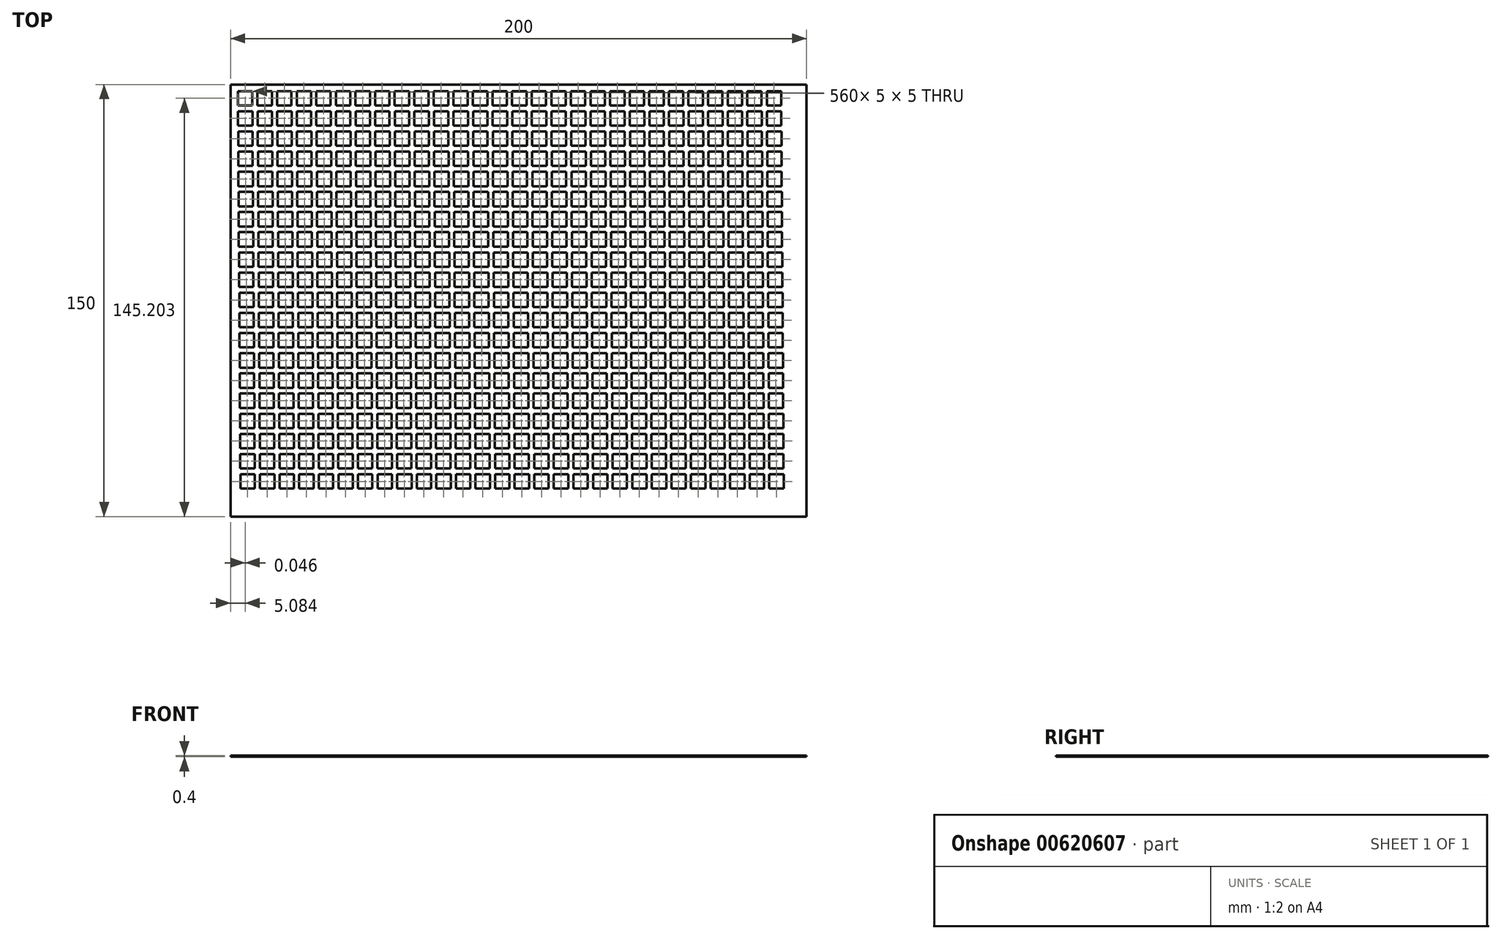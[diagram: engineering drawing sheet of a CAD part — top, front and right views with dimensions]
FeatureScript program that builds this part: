
annotation { "Feature Type Name" : "Feature", "Feature Type Description" : "" }
export const myFeature = defineFeature(function(context is Context, id is Id, definition is map)
    precondition{}
    {
        {
            var Q0;
            Q0=qCreatedBy(makeId("Top.planeOp"),FACE);
            var sketch = newSketch(context, id + "F0", { "sketchPlane" : qUnion([Q0])});
            skLineSegment(sketch, "E0.bottom", {"start": v(0, 0) * mm, "end": v(200, 0) * mm});
            skLineSegment(sketch, "E0.top", {"start": v(0, -150) * mm, "end": v(200, -150) * mm});
            skLineSegment(sketch, "E0.left", {"start": v(0, 0) * mm, "end": v(0, -150) * mm});
            skLineSegment(sketch, "E0.right", {"start": v(200, 0) * mm, "end": v(200, -150) * mm});
            skSolve(sketch);
        }
        {
            var Q0;
            Q0 = qSketchRegion(id + "F0", true);
            extrude(context, id + "F1", {"entities" : qUnion([Q0]), "depth" : 0.4 * mm, "offsetDistance" : 25 * mm});
        }
        {
            var Q0;
            Q0=makeQuery(id+"F1.opExtrude","CAP_FACE",FACE,{"disambiguationData":[OSD([sQuery(id+"F0.wireOp",EDGE,"E0.bottom"),sQuery(id+"F0.wireOp",EDGE,"E0.top"),sQuery(id+"F0.wireOp",EDGE,"E0.left"),sQuery(id+"F0.wireOp",EDGE,"E0.right")])],"isStart":false});
            var sketch = newSketch(context, id + "F2", { "sketchPlane" : qUnion([Q0])});
            skLineSegment(sketch, "E1.bottom", {"start": v(2.58, -2.3) * mm, "end": v(7.58, -2.3) * mm});
            skLineSegment(sketch, "E1.top", {"start": v(2.58, -7.3) * mm, "end": v(7.58, -7.3) * mm});
            skLineSegment(sketch, "E1.left", {"start": v(2.58, -2.3) * mm, "end": v(2.58, -7.3) * mm});
            skLineSegment(sketch, "E1.right", {"start": v(7.58, -2.3) * mm, "end": v(7.58, -7.3) * mm});
            skLineSegment(sketch, "E2.1.0.0", {"start": v(9.38, -2.3) * mm, "end": v(9.38, -7.3) * mm});
            skLineSegment(sketch, "E2.1.0.1", {"start": v(9.38, -2.3) * mm, "end": v(14.38, -2.3) * mm});
            skLineSegment(sketch, "E2.1.0.2", {"start": v(9.38, -7.3) * mm, "end": v(14.38, -7.3) * mm});
            skLineSegment(sketch, "E2.1.0.3", {"start": v(14.38, -2.3) * mm, "end": v(14.38, -7.3) * mm});
            skLineSegment(sketch, "E2.2.0.0", {"start": v(16.18, -2.3) * mm, "end": v(16.18, -7.3) * mm});
            skLineSegment(sketch, "E2.2.0.1", {"start": v(16.18, -2.3) * mm, "end": v(21.18, -2.3) * mm});
            skLineSegment(sketch, "E2.2.0.2", {"start": v(16.18, -7.3) * mm, "end": v(21.18, -7.3) * mm});
            skLineSegment(sketch, "E2.2.0.3", {"start": v(21.18, -2.3) * mm, "end": v(21.18, -7.3) * mm});
            skLineSegment(sketch, "E2.3.0.0", {"start": v(22.98, -2.3) * mm, "end": v(22.98, -7.3) * mm});
            skLineSegment(sketch, "E2.3.0.1", {"start": v(22.98, -2.3) * mm, "end": v(27.98, -2.3) * mm});
            skLineSegment(sketch, "E2.3.0.2", {"start": v(22.98, -7.3) * mm, "end": v(27.98, -7.3) * mm});
            skLineSegment(sketch, "E2.3.0.3", {"start": v(27.98, -2.3) * mm, "end": v(27.98, -7.3) * mm});
            skLineSegment(sketch, "E2.4.0.0", {"start": v(29.78, -2.3) * mm, "end": v(29.78, -7.3) * mm});
            skLineSegment(sketch, "E2.4.0.1", {"start": v(29.78, -2.3) * mm, "end": v(34.78, -2.3) * mm});
            skLineSegment(sketch, "E2.4.0.2", {"start": v(29.78, -7.3) * mm, "end": v(34.78, -7.3) * mm});
            skLineSegment(sketch, "E2.4.0.3", {"start": v(34.78, -2.3) * mm, "end": v(34.78, -7.3) * mm});
            skLineSegment(sketch, "E2.5.0.0", {"start": v(36.58, -2.3) * mm, "end": v(36.58, -7.3) * mm});
            skLineSegment(sketch, "E2.5.0.1", {"start": v(36.58, -2.3) * mm, "end": v(41.58, -2.3) * mm});
            skLineSegment(sketch, "E2.5.0.2", {"start": v(36.58, -7.3) * mm, "end": v(41.58, -7.3) * mm});
            skLineSegment(sketch, "E2.5.0.3", {"start": v(41.58, -2.3) * mm, "end": v(41.58, -7.3) * mm});
            skLineSegment(sketch, "E2.6.0.0", {"start": v(43.38, -2.3) * mm, "end": v(43.38, -7.3) * mm});
            skLineSegment(sketch, "E2.6.0.1", {"start": v(43.38, -2.3) * mm, "end": v(48.38, -2.3) * mm});
            skLineSegment(sketch, "E2.6.0.2", {"start": v(43.38, -7.3) * mm, "end": v(48.38, -7.3) * mm});
            skLineSegment(sketch, "E2.6.0.3", {"start": v(48.38, -2.3) * mm, "end": v(48.38, -7.3) * mm});
            skLineSegment(sketch, "E2.7.0.0", {"start": v(50.18, -2.3) * mm, "end": v(50.18, -7.3) * mm});
            skLineSegment(sketch, "E2.7.0.1", {"start": v(50.18, -2.3) * mm, "end": v(55.18, -2.3) * mm});
            skLineSegment(sketch, "E2.7.0.2", {"start": v(50.18, -7.3) * mm, "end": v(55.18, -7.3) * mm});
            skLineSegment(sketch, "E2.7.0.3", {"start": v(55.18, -2.3) * mm, "end": v(55.18, -7.3) * mm});
            skLineSegment(sketch, "E2.8.0.0", {"start": v(56.98, -2.3) * mm, "end": v(56.98, -7.3) * mm});
            skLineSegment(sketch, "E2.8.0.1", {"start": v(56.98, -2.3) * mm, "end": v(61.98, -2.3) * mm});
            skLineSegment(sketch, "E2.8.0.2", {"start": v(56.98, -7.3) * mm, "end": v(61.98, -7.3) * mm});
            skLineSegment(sketch, "E2.8.0.3", {"start": v(61.98, -2.3) * mm, "end": v(61.98, -7.3) * mm});
            skLineSegment(sketch, "E2.9.0.0", {"start": v(63.78, -2.3) * mm, "end": v(63.78, -7.3) * mm});
            skLineSegment(sketch, "E2.9.0.1", {"start": v(63.78, -2.3) * mm, "end": v(68.78, -2.3) * mm});
            skLineSegment(sketch, "E2.9.0.2", {"start": v(63.78, -7.3) * mm, "end": v(68.78, -7.3) * mm});
            skLineSegment(sketch, "E2.9.0.3", {"start": v(68.78, -2.3) * mm, "end": v(68.78, -7.3) * mm});
            skLineSegment(sketch, "E2.10.0.0", {"start": v(70.58, -2.3) * mm, "end": v(70.58, -7.3) * mm});
            skLineSegment(sketch, "E2.10.0.1", {"start": v(70.58, -2.3) * mm, "end": v(75.58, -2.3) * mm});
            skLineSegment(sketch, "E2.10.0.2", {"start": v(70.58, -7.3) * mm, "end": v(75.58, -7.3) * mm});
            skLineSegment(sketch, "E2.10.0.3", {"start": v(75.58, -2.3) * mm, "end": v(75.58, -7.3) * mm});
            skLineSegment(sketch, "E2.11.0.0", {"start": v(77.38, -2.3) * mm, "end": v(77.38, -7.3) * mm});
            skLineSegment(sketch, "E2.11.0.1", {"start": v(77.38, -2.3) * mm, "end": v(82.38, -2.3) * mm});
            skLineSegment(sketch, "E2.11.0.2", {"start": v(77.38, -7.3) * mm, "end": v(82.38, -7.3) * mm});
            skLineSegment(sketch, "E2.11.0.3", {"start": v(82.38, -2.3) * mm, "end": v(82.38, -7.3) * mm});
            skLineSegment(sketch, "E2.12.0.0", {"start": v(84.18, -2.3) * mm, "end": v(84.18, -7.3) * mm});
            skLineSegment(sketch, "E2.12.0.1", {"start": v(84.18, -2.3) * mm, "end": v(89.18, -2.3) * mm});
            skLineSegment(sketch, "E2.12.0.2", {"start": v(84.18, -7.3) * mm, "end": v(89.18, -7.3) * mm});
            skLineSegment(sketch, "E2.12.0.3", {"start": v(89.18, -2.3) * mm, "end": v(89.18, -7.3) * mm});
            skLineSegment(sketch, "E2.13.0.0", {"start": v(90.98, -2.3) * mm, "end": v(90.98, -7.3) * mm});
            skLineSegment(sketch, "E2.13.0.1", {"start": v(90.98, -2.3) * mm, "end": v(95.98, -2.3) * mm});
            skLineSegment(sketch, "E2.13.0.2", {"start": v(90.98, -7.3) * mm, "end": v(95.98, -7.3) * mm});
            skLineSegment(sketch, "E2.13.0.3", {"start": v(95.98, -2.3) * mm, "end": v(95.98, -7.3) * mm});
            skLineSegment(sketch, "E2.14.0.0", {"start": v(97.78, -2.3) * mm, "end": v(97.78, -7.3) * mm});
            skLineSegment(sketch, "E2.14.0.1", {"start": v(97.78, -2.3) * mm, "end": v(102.78, -2.3) * mm});
            skLineSegment(sketch, "E2.14.0.2", {"start": v(97.78, -7.3) * mm, "end": v(102.78, -7.3) * mm});
            skLineSegment(sketch, "E2.14.0.3", {"start": v(102.78, -2.3) * mm, "end": v(102.78, -7.3) * mm});
            skLineSegment(sketch, "E2.15.0.0", {"start": v(104.58, -2.3) * mm, "end": v(104.58, -7.3) * mm});
            skLineSegment(sketch, "E2.15.0.1", {"start": v(104.58, -2.3) * mm, "end": v(109.58, -2.3) * mm});
            skLineSegment(sketch, "E2.15.0.2", {"start": v(104.58, -7.3) * mm, "end": v(109.58, -7.3) * mm});
            skLineSegment(sketch, "E2.15.0.3", {"start": v(109.58, -2.3) * mm, "end": v(109.58, -7.3) * mm});
            skLineSegment(sketch, "E2.16.0.0", {"start": v(111.38, -2.3) * mm, "end": v(111.38, -7.3) * mm});
            skLineSegment(sketch, "E2.16.0.1", {"start": v(111.38, -2.3) * mm, "end": v(116.38, -2.3) * mm});
            skLineSegment(sketch, "E2.16.0.2", {"start": v(111.38, -7.3) * mm, "end": v(116.38, -7.3) * mm});
            skLineSegment(sketch, "E2.16.0.3", {"start": v(116.38, -2.3) * mm, "end": v(116.38, -7.3) * mm});
            skLineSegment(sketch, "E2.17.0.0", {"start": v(118.18, -2.3) * mm, "end": v(118.18, -7.3) * mm});
            skLineSegment(sketch, "E2.17.0.1", {"start": v(118.18, -2.3) * mm, "end": v(123.18, -2.3) * mm});
            skLineSegment(sketch, "E2.17.0.2", {"start": v(118.18, -7.3) * mm, "end": v(123.18, -7.3) * mm});
            skLineSegment(sketch, "E2.17.0.3", {"start": v(123.18, -2.3) * mm, "end": v(123.18, -7.3) * mm});
            skLineSegment(sketch, "E2.18.0.0", {"start": v(124.98, -2.3) * mm, "end": v(124.98, -7.3) * mm});
            skLineSegment(sketch, "E2.18.0.1", {"start": v(124.98, -2.3) * mm, "end": v(129.98, -2.3) * mm});
            skLineSegment(sketch, "E2.18.0.2", {"start": v(124.98, -7.3) * mm, "end": v(129.98, -7.3) * mm});
            skLineSegment(sketch, "E2.18.0.3", {"start": v(129.98, -2.3) * mm, "end": v(129.98, -7.3) * mm});
            skLineSegment(sketch, "E2.19.0.0", {"start": v(131.78, -2.3) * mm, "end": v(131.78, -7.3) * mm});
            skLineSegment(sketch, "E2.19.0.1", {"start": v(131.78, -2.3) * mm, "end": v(136.78, -2.3) * mm});
            skLineSegment(sketch, "E2.19.0.2", {"start": v(131.78, -7.3) * mm, "end": v(136.78, -7.3) * mm});
            skLineSegment(sketch, "E2.19.0.3", {"start": v(136.78, -2.3) * mm, "end": v(136.78, -7.3) * mm});
            skLineSegment(sketch, "E2.20.0.0", {"start": v(138.58, -2.3) * mm, "end": v(138.58, -7.3) * mm});
            skLineSegment(sketch, "E2.20.0.1", {"start": v(138.58, -2.3) * mm, "end": v(143.58, -2.3) * mm});
            skLineSegment(sketch, "E2.20.0.2", {"start": v(138.58, -7.3) * mm, "end": v(143.58, -7.3) * mm});
            skLineSegment(sketch, "E2.20.0.3", {"start": v(143.58, -2.3) * mm, "end": v(143.58, -7.3) * mm});
            skLineSegment(sketch, "E2.21.0.0", {"start": v(145.38, -2.3) * mm, "end": v(145.38, -7.3) * mm});
            skLineSegment(sketch, "E2.21.0.1", {"start": v(145.38, -2.3) * mm, "end": v(150.38, -2.3) * mm});
            skLineSegment(sketch, "E2.21.0.2", {"start": v(145.38, -7.3) * mm, "end": v(150.38, -7.3) * mm});
            skLineSegment(sketch, "E2.21.0.3", {"start": v(150.38, -2.3) * mm, "end": v(150.38, -7.3) * mm});
            skLineSegment(sketch, "E2.22.0.0", {"start": v(152.18, -2.3) * mm, "end": v(152.18, -7.3) * mm});
            skLineSegment(sketch, "E2.22.0.1", {"start": v(152.18, -2.3) * mm, "end": v(157.18, -2.3) * mm});
            skLineSegment(sketch, "E2.22.0.2", {"start": v(152.18, -7.3) * mm, "end": v(157.18, -7.3) * mm});
            skLineSegment(sketch, "E2.22.0.3", {"start": v(157.18, -2.3) * mm, "end": v(157.18, -7.3) * mm});
            skLineSegment(sketch, "E2.23.0.0", {"start": v(158.98, -2.3) * mm, "end": v(158.98, -7.3) * mm});
            skLineSegment(sketch, "E2.23.0.1", {"start": v(158.98, -2.3) * mm, "end": v(163.98, -2.3) * mm});
            skLineSegment(sketch, "E2.23.0.2", {"start": v(158.98, -7.3) * mm, "end": v(163.98, -7.3) * mm});
            skLineSegment(sketch, "E2.23.0.3", {"start": v(163.98, -2.3) * mm, "end": v(163.98, -7.3) * mm});
            skLineSegment(sketch, "E2.24.0.0", {"start": v(165.78, -2.3) * mm, "end": v(165.78, -7.3) * mm});
            skLineSegment(sketch, "E2.24.0.1", {"start": v(165.78, -2.3) * mm, "end": v(170.78, -2.3) * mm});
            skLineSegment(sketch, "E2.24.0.2", {"start": v(165.78, -7.3) * mm, "end": v(170.78, -7.3) * mm});
            skLineSegment(sketch, "E2.24.0.3", {"start": v(170.78, -2.3) * mm, "end": v(170.78, -7.3) * mm});
            skLineSegment(sketch, "E2.25.0.0", {"start": v(172.58, -2.3) * mm, "end": v(172.58, -7.3) * mm});
            skLineSegment(sketch, "E2.25.0.1", {"start": v(172.58, -2.3) * mm, "end": v(177.58, -2.3) * mm});
            skLineSegment(sketch, "E2.25.0.2", {"start": v(172.58, -7.3) * mm, "end": v(177.58, -7.3) * mm});
            skLineSegment(sketch, "E2.25.0.3", {"start": v(177.58, -2.3) * mm, "end": v(177.58, -7.3) * mm});
            skLineSegment(sketch, "E2.direction1", {"start": v(2.58, -7.3) * mm, "end": v(9.38, -7.3) * mm, "construction": true});
            skLineSegment(sketch, "E3.0.26.0", {"start": v(179.38, -2.3) * mm, "end": v(179.38, -7.3) * mm});
            skLineSegment(sketch, "E3.3.26.0", {"start": v(179.38, -2.3) * mm, "end": v(184.38, -2.3) * mm});
            skLineSegment(sketch, "E3.6.26.0", {"start": v(179.38, -7.3) * mm, "end": v(184.38, -7.3) * mm});
            skLineSegment(sketch, "E3.9.26.0", {"start": v(184.38, -2.3) * mm, "end": v(184.38, -7.3) * mm});
            skLineSegment(sketch, "E3.0.27.0", {"start": v(186.18, -2.3) * mm, "end": v(186.18, -7.3) * mm});
            skLineSegment(sketch, "E3.3.27.0", {"start": v(186.18, -2.3) * mm, "end": v(191.18, -2.3) * mm});
            skLineSegment(sketch, "E3.6.27.0", {"start": v(186.18, -7.3) * mm, "end": v(191.18, -7.3) * mm});
            skLineSegment(sketch, "E3.9.27.0", {"start": v(191.18, -2.3) * mm, "end": v(191.18, -7.3) * mm});
            skLineSegment(sketch, "E4.1.0.0", {"start": v(111.43, -9.3) * mm, "end": v(116.43, -9.3) * mm});
            skLineSegment(sketch, "E4.1.0.1", {"start": v(116.43, -9.3) * mm, "end": v(116.43, -14.3) * mm});
            skLineSegment(sketch, "E4.1.0.2", {"start": v(125.03, -9.3) * mm, "end": v(130.03, -9.3) * mm});
            skLineSegment(sketch, "E4.1.0.3", {"start": v(28.03, -9.3) * mm, "end": v(28.03, -14.3) * mm});
            skLineSegment(sketch, "E4.1.0.4", {"start": v(70.63, -9.3) * mm, "end": v(75.63, -9.3) * mm});
            skLineSegment(sketch, "E4.1.0.5", {"start": v(172.63, -9.3) * mm, "end": v(172.63, -14.3) * mm});
            skLineSegment(sketch, "E4.1.0.6", {"start": v(48.43, -9.3) * mm, "end": v(48.43, -14.3) * mm});
            skLineSegment(sketch, "E4.1.0.7", {"start": v(84.23, -9.3) * mm, "end": v(84.23, -14.3) * mm});
            skLineSegment(sketch, "E4.1.0.8", {"start": v(14.43, -9.3) * mm, "end": v(14.43, -14.3) * mm});
            skLineSegment(sketch, "E4.1.0.9", {"start": v(97.83, -9.3) * mm, "end": v(102.83, -9.3) * mm});
            skLineSegment(sketch, "E4.1.0.10", {"start": v(165.83, -9.3) * mm, "end": v(165.83, -14.3) * mm});
            skLineSegment(sketch, "E4.1.0.11", {"start": v(91.03, -9.3) * mm, "end": v(96.03, -9.3) * mm});
            skLineSegment(sketch, "E4.1.0.12", {"start": v(70.63, -14.3) * mm, "end": v(75.63, -14.3) * mm});
            skLineSegment(sketch, "E4.1.0.13", {"start": v(131.83, -14.3) * mm, "end": v(136.83, -14.3) * mm});
            skLineSegment(sketch, "E4.1.0.14", {"start": v(145.43, -9.3) * mm, "end": v(145.43, -14.3) * mm});
            skLineSegment(sketch, "E4.1.0.15", {"start": v(104.63, -14.3) * mm, "end": v(109.63, -14.3) * mm});
            skLineSegment(sketch, "E4.1.0.16", {"start": v(191.23, -9.3) * mm, "end": v(191.23, -14.3) * mm});
            skLineSegment(sketch, "E4.1.0.17", {"start": v(159.03, -14.3) * mm, "end": v(164.03, -14.3) * mm});
            skLineSegment(sketch, "E4.1.0.18", {"start": v(75.63, -9.3) * mm, "end": v(75.63, -14.3) * mm});
            skLineSegment(sketch, "E4.1.0.19", {"start": v(23.03, -9.3) * mm, "end": v(23.03, -14.3) * mm});
            skLineSegment(sketch, "E4.1.0.20", {"start": v(145.43, -9.3) * mm, "end": v(150.43, -9.3) * mm});
            skLineSegment(sketch, "E4.1.0.21", {"start": v(138.63, -14.3) * mm, "end": v(143.63, -14.3) * mm});
            skLineSegment(sketch, "E4.1.0.22", {"start": v(184.43, -9.3) * mm, "end": v(184.43, -14.3) * mm});
            skLineSegment(sketch, "E4.1.0.23", {"start": v(55.23, -9.3) * mm, "end": v(55.23, -14.3) * mm});
            skLineSegment(sketch, "E4.1.0.24", {"start": v(170.83, -9.3) * mm, "end": v(170.83, -14.3) * mm});
            skLineSegment(sketch, "E4.1.0.25", {"start": v(62.03, -9.3) * mm, "end": v(62.03, -14.3) * mm});
            skLineSegment(sketch, "E4.1.0.26", {"start": v(68.83, -9.3) * mm, "end": v(68.83, -14.3) * mm});
            skLineSegment(sketch, "E4.1.0.27", {"start": v(131.83, -9.3) * mm, "end": v(136.83, -9.3) * mm});
            skLineSegment(sketch, "E4.1.0.28", {"start": v(63.83, -9.3) * mm, "end": v(63.83, -14.3) * mm});
            skLineSegment(sketch, "E4.1.0.29", {"start": v(152.23, -14.3) * mm, "end": v(157.23, -14.3) * mm});
            skLineSegment(sketch, "E4.1.0.30", {"start": v(179.43, -14.3) * mm, "end": v(184.43, -14.3) * mm});
            skLineSegment(sketch, "E4.1.0.31", {"start": v(36.63, -9.3) * mm, "end": v(36.63, -14.3) * mm});
            skLineSegment(sketch, "E4.1.0.32", {"start": v(172.63, -14.3) * mm, "end": v(177.63, -14.3) * mm});
            skLineSegment(sketch, "E4.1.0.33", {"start": v(91.03, -9.3) * mm, "end": v(91.03, -14.3) * mm});
            skLineSegment(sketch, "E4.1.0.34", {"start": v(77.43, -9.3) * mm, "end": v(82.43, -9.3) * mm});
            skLineSegment(sketch, "E4.1.0.35", {"start": v(70.63, -9.3) * mm, "end": v(70.63, -14.3) * mm});
            skLineSegment(sketch, "E4.1.0.36", {"start": v(57.03, -14.3) * mm, "end": v(62.03, -14.3) * mm});
            skLineSegment(sketch, "E4.1.0.37", {"start": v(111.43, -9.3) * mm, "end": v(111.43, -14.3) * mm});
            skLineSegment(sketch, "E4.1.0.38", {"start": v(150.43, -9.3) * mm, "end": v(150.43, -14.3) * mm});
            skLineSegment(sketch, "E4.1.0.39", {"start": v(177.63, -9.3) * mm, "end": v(177.63, -14.3) * mm});
            skLineSegment(sketch, "E4.1.0.40", {"start": v(179.43, -9.3) * mm, "end": v(179.43, -14.3) * mm});
            skLineSegment(sketch, "E4.1.0.41", {"start": v(97.83, -9.3) * mm, "end": v(97.83, -14.3) * mm});
            skLineSegment(sketch, "E4.1.0.42", {"start": v(36.63, -9.3) * mm, "end": v(41.63, -9.3) * mm});
            skLineSegment(sketch, "E4.1.0.43", {"start": v(118.23, -14.3) * mm, "end": v(123.23, -14.3) * mm});
            skLineSegment(sketch, "E4.1.0.44", {"start": v(7.63, -9.3) * mm, "end": v(7.63, -14.3) * mm});
            skLineSegment(sketch, "E4.1.0.45", {"start": v(43.43, -9.3) * mm, "end": v(43.43, -14.3) * mm});
            skLineSegment(sketch, "E4.1.0.46", {"start": v(77.43, -14.3) * mm, "end": v(82.43, -14.3) * mm});
            skLineSegment(sketch, "E4.1.0.47", {"start": v(138.63, -9.3) * mm, "end": v(143.63, -9.3) * mm});
            skLineSegment(sketch, "E4.1.0.48", {"start": v(23.03, -9.3) * mm, "end": v(28.03, -9.3) * mm});
            skLineSegment(sketch, "E4.1.0.49", {"start": v(152.23, -9.3) * mm, "end": v(152.23, -14.3) * mm});
            skLineSegment(sketch, "E4.1.0.50", {"start": v(57.03, -9.3) * mm, "end": v(62.03, -9.3) * mm});
            skLineSegment(sketch, "E4.1.0.51", {"start": v(43.43, -9.3) * mm, "end": v(48.43, -9.3) * mm});
            skLineSegment(sketch, "E4.1.0.52", {"start": v(41.63, -9.3) * mm, "end": v(41.63, -14.3) * mm});
            skLineSegment(sketch, "E4.1.0.53", {"start": v(125.03, -14.3) * mm, "end": v(130.03, -14.3) * mm});
            skLineSegment(sketch, "E4.1.0.54", {"start": v(186.23, -14.3) * mm, "end": v(191.23, -14.3) * mm});
            skLineSegment(sketch, "E4.1.0.55", {"start": v(125.03, -9.3) * mm, "end": v(125.03, -14.3) * mm});
            skLineSegment(sketch, "E4.1.0.56", {"start": v(63.83, -9.3) * mm, "end": v(68.83, -9.3) * mm});
            skLineSegment(sketch, "E4.1.0.57", {"start": v(63.83, -14.3) * mm, "end": v(68.83, -14.3) * mm});
            skLineSegment(sketch, "E4.1.0.58", {"start": v(164.03, -9.3) * mm, "end": v(164.03, -14.3) * mm});
            skLineSegment(sketch, "E4.1.0.59", {"start": v(186.23, -9.3) * mm, "end": v(186.23, -14.3) * mm});
            skLineSegment(sketch, "E4.1.0.60", {"start": v(9.43, -9.3) * mm, "end": v(9.43, -14.3) * mm});
            skLineSegment(sketch, "E4.1.0.61", {"start": v(84.23, -9.3) * mm, "end": v(89.23, -9.3) * mm});
            skLineSegment(sketch, "E4.1.0.62", {"start": v(9.43, -9.3) * mm, "end": v(14.43, -9.3) * mm});
            skLineSegment(sketch, "E4.1.0.63", {"start": v(50.23, -9.3) * mm, "end": v(55.23, -9.3) * mm});
            skLineSegment(sketch, "E4.1.0.64", {"start": v(109.63, -9.3) * mm, "end": v(109.63, -14.3) * mm});
            skLineSegment(sketch, "E4.1.0.65", {"start": v(91.03, -14.3) * mm, "end": v(96.03, -14.3) * mm});
            skLineSegment(sketch, "E4.1.0.66", {"start": v(102.83, -9.3) * mm, "end": v(102.83, -14.3) * mm});
            skLineSegment(sketch, "E4.1.0.67", {"start": v(2.63, -9.3) * mm, "end": v(7.63, -9.3) * mm});
            skLineSegment(sketch, "E4.1.0.68", {"start": v(97.83, -14.3) * mm, "end": v(102.83, -14.3) * mm});
            skLineSegment(sketch, "E4.1.0.69", {"start": v(123.23, -9.3) * mm, "end": v(123.23, -14.3) * mm});
            skLineSegment(sketch, "E4.1.0.70", {"start": v(84.23, -14.3) * mm, "end": v(89.23, -14.3) * mm});
            skLineSegment(sketch, "E4.1.0.71", {"start": v(16.23, -9.3) * mm, "end": v(21.23, -9.3) * mm});
            skLineSegment(sketch, "E4.1.0.72", {"start": v(29.83, -9.3) * mm, "end": v(34.83, -9.3) * mm});
            skLineSegment(sketch, "E4.1.0.73", {"start": v(77.43, -9.3) * mm, "end": v(77.43, -14.3) * mm});
            skLineSegment(sketch, "E4.1.0.74", {"start": v(2.63, -9.3) * mm, "end": v(2.63, -14.3) * mm});
            skLineSegment(sketch, "E4.1.0.75", {"start": v(29.83, -9.3) * mm, "end": v(29.83, -14.3) * mm});
            skLineSegment(sketch, "E4.1.0.76", {"start": v(159.03, -9.3) * mm, "end": v(159.03, -14.3) * mm});
            skLineSegment(sketch, "E4.1.0.77", {"start": v(104.63, -9.3) * mm, "end": v(109.63, -9.3) * mm});
            skLineSegment(sketch, "E4.1.0.78", {"start": v(82.43, -9.3) * mm, "end": v(82.43, -14.3) * mm});
            skLineSegment(sketch, "E4.1.0.79", {"start": v(34.83, -9.3) * mm, "end": v(34.83, -14.3) * mm});
            skLineSegment(sketch, "E4.1.0.80", {"start": v(157.23, -9.3) * mm, "end": v(157.23, -14.3) * mm});
            skLineSegment(sketch, "E4.1.0.81", {"start": v(21.23, -9.3) * mm, "end": v(21.23, -14.3) * mm});
            skLineSegment(sketch, "E4.1.0.82", {"start": v(143.63, -9.3) * mm, "end": v(143.63, -14.3) * mm});
            skLineSegment(sketch, "E4.1.0.83", {"start": v(138.63, -9.3) * mm, "end": v(138.63, -14.3) * mm});
            skLineSegment(sketch, "E4.1.0.84", {"start": v(130.03, -9.3) * mm, "end": v(130.03, -14.3) * mm});
            skLineSegment(sketch, "E4.1.0.85", {"start": v(57.03, -9.3) * mm, "end": v(57.03, -14.3) * mm});
            skLineSegment(sketch, "E4.1.0.86", {"start": v(136.83, -9.3) * mm, "end": v(136.83, -14.3) * mm});
            skLineSegment(sketch, "E4.1.0.87", {"start": v(118.23, -9.3) * mm, "end": v(118.23, -14.3) * mm});
            skLineSegment(sketch, "E4.1.0.88", {"start": v(96.03, -9.3) * mm, "end": v(96.03, -14.3) * mm});
            skLineSegment(sketch, "E4.1.0.89", {"start": v(145.43, -14.3) * mm, "end": v(150.43, -14.3) * mm});
            skLineSegment(sketch, "E4.1.0.90", {"start": v(165.83, -14.3) * mm, "end": v(170.83, -14.3) * mm});
            skLineSegment(sketch, "E4.1.0.91", {"start": v(50.23, -9.3) * mm, "end": v(50.23, -14.3) * mm});
            skLineSegment(sketch, "E4.1.0.92", {"start": v(118.23, -9.3) * mm, "end": v(123.23, -9.3) * mm});
            skLineSegment(sketch, "E4.1.0.93", {"start": v(131.83, -9.3) * mm, "end": v(131.83, -14.3) * mm});
            skLineSegment(sketch, "E4.1.0.94", {"start": v(16.23, -9.3) * mm, "end": v(16.23, -14.3) * mm});
            skLineSegment(sketch, "E4.1.0.95", {"start": v(104.63, -9.3) * mm, "end": v(104.63, -14.3) * mm});
            skLineSegment(sketch, "E4.1.0.96", {"start": v(111.43, -14.3) * mm, "end": v(116.43, -14.3) * mm});
            skLineSegment(sketch, "E4.1.0.97", {"start": v(89.23, -9.3) * mm, "end": v(89.23, -14.3) * mm});
            skLineSegment(sketch, "E4.1.0.98", {"start": v(152.23, -9.3) * mm, "end": v(157.23, -9.3) * mm});
            skLineSegment(sketch, "E4.1.0.99", {"start": v(186.23, -9.3) * mm, "end": v(191.23, -9.3) * mm});
            skLineSegment(sketch, "E4.1.0.100", {"start": v(36.63, -14.3) * mm, "end": v(41.63, -14.3) * mm});
            skLineSegment(sketch, "E4.1.0.101", {"start": v(43.43, -14.3) * mm, "end": v(48.43, -14.3) * mm});
            skLineSegment(sketch, "E4.1.0.102", {"start": v(2.63, -14.3) * mm, "end": v(9.43, -14.3) * mm, "construction": true});
            skLineSegment(sketch, "E4.1.0.103", {"start": v(159.03, -9.3) * mm, "end": v(164.03, -9.3) * mm});
            skLineSegment(sketch, "E4.1.0.104", {"start": v(165.83, -9.3) * mm, "end": v(170.83, -9.3) * mm});
            skLineSegment(sketch, "E4.1.0.105", {"start": v(172.63, -9.3) * mm, "end": v(177.63, -9.3) * mm});
            skLineSegment(sketch, "E4.1.0.106", {"start": v(16.23, -14.3) * mm, "end": v(21.23, -14.3) * mm});
            skLineSegment(sketch, "E4.1.0.107", {"start": v(29.83, -14.3) * mm, "end": v(34.83, -14.3) * mm});
            skLineSegment(sketch, "E4.1.0.108", {"start": v(23.03, -14.3) * mm, "end": v(28.03, -14.3) * mm});
            skLineSegment(sketch, "E4.1.0.109", {"start": v(9.43, -14.3) * mm, "end": v(14.43, -14.3) * mm});
            skLineSegment(sketch, "E4.1.0.110", {"start": v(50.23, -14.3) * mm, "end": v(55.23, -14.3) * mm});
            skLineSegment(sketch, "E4.1.0.111", {"start": v(179.43, -9.3) * mm, "end": v(184.43, -9.3) * mm});
            skLineSegment(sketch, "E4.1.0.112", {"start": v(2.63, -14.3) * mm, "end": v(7.63, -14.3) * mm});
            skLineSegment(sketch, "E4.2.0.0", {"start": v(111.48, -16.3) * mm, "end": v(116.48, -16.3) * mm});
            skLineSegment(sketch, "E4.2.0.1", {"start": v(116.48, -16.3) * mm, "end": v(116.48, -21.3) * mm});
            skLineSegment(sketch, "E4.2.0.2", {"start": v(125.08, -16.3) * mm, "end": v(130.08, -16.3) * mm});
            skLineSegment(sketch, "E4.2.0.3", {"start": v(28.08, -16.3) * mm, "end": v(28.08, -21.3) * mm});
            skLineSegment(sketch, "E4.2.0.4", {"start": v(70.68, -16.3) * mm, "end": v(75.68, -16.3) * mm});
            skLineSegment(sketch, "E4.2.0.5", {"start": v(172.68, -16.3) * mm, "end": v(172.68, -21.3) * mm});
            skLineSegment(sketch, "E4.2.0.6", {"start": v(48.48, -16.3) * mm, "end": v(48.48, -21.3) * mm});
            skLineSegment(sketch, "E4.2.0.7", {"start": v(84.28, -16.3) * mm, "end": v(84.28, -21.3) * mm});
            skLineSegment(sketch, "E4.2.0.8", {"start": v(14.48, -16.3) * mm, "end": v(14.48, -21.3) * mm});
            skLineSegment(sketch, "E4.2.0.9", {"start": v(97.88, -16.3) * mm, "end": v(102.88, -16.3) * mm});
            skLineSegment(sketch, "E4.2.0.10", {"start": v(165.88, -16.3) * mm, "end": v(165.88, -21.3) * mm});
            skLineSegment(sketch, "E4.2.0.11", {"start": v(91.08, -16.3) * mm, "end": v(96.08, -16.3) * mm});
            skLineSegment(sketch, "E4.2.0.12", {"start": v(70.68, -21.3) * mm, "end": v(75.68, -21.3) * mm});
            skLineSegment(sketch, "E4.2.0.13", {"start": v(131.88, -21.3) * mm, "end": v(136.88, -21.3) * mm});
            skLineSegment(sketch, "E4.2.0.14", {"start": v(145.48, -16.3) * mm, "end": v(145.48, -21.3) * mm});
            skLineSegment(sketch, "E4.2.0.15", {"start": v(104.68, -21.3) * mm, "end": v(109.68, -21.3) * mm});
            skLineSegment(sketch, "E4.2.0.16", {"start": v(191.28, -16.3) * mm, "end": v(191.28, -21.3) * mm});
            skLineSegment(sketch, "E4.2.0.17", {"start": v(159.08, -21.3) * mm, "end": v(164.08, -21.3) * mm});
            skLineSegment(sketch, "E4.2.0.18", {"start": v(75.68, -16.3) * mm, "end": v(75.68, -21.3) * mm});
            skLineSegment(sketch, "E4.2.0.19", {"start": v(23.08, -16.3) * mm, "end": v(23.08, -21.3) * mm});
            skLineSegment(sketch, "E4.2.0.20", {"start": v(145.48, -16.3) * mm, "end": v(150.48, -16.3) * mm});
            skLineSegment(sketch, "E4.2.0.21", {"start": v(138.68, -21.3) * mm, "end": v(143.68, -21.3) * mm});
            skLineSegment(sketch, "E4.2.0.22", {"start": v(184.48, -16.3) * mm, "end": v(184.48, -21.3) * mm});
            skLineSegment(sketch, "E4.2.0.23", {"start": v(55.28, -16.3) * mm, "end": v(55.28, -21.3) * mm});
            skLineSegment(sketch, "E4.2.0.24", {"start": v(170.88, -16.3) * mm, "end": v(170.88, -21.3) * mm});
            skLineSegment(sketch, "E4.2.0.25", {"start": v(62.08, -16.3) * mm, "end": v(62.08, -21.3) * mm});
            skLineSegment(sketch, "E4.2.0.26", {"start": v(68.88, -16.3) * mm, "end": v(68.88, -21.3) * mm});
            skLineSegment(sketch, "E4.2.0.27", {"start": v(131.88, -16.3) * mm, "end": v(136.88, -16.3) * mm});
            skLineSegment(sketch, "E4.2.0.28", {"start": v(63.88, -16.3) * mm, "end": v(63.88, -21.3) * mm});
            skLineSegment(sketch, "E4.2.0.29", {"start": v(152.28, -21.3) * mm, "end": v(157.28, -21.3) * mm});
            skLineSegment(sketch, "E4.2.0.30", {"start": v(179.48, -21.3) * mm, "end": v(184.48, -21.3) * mm});
            skLineSegment(sketch, "E4.2.0.31", {"start": v(36.68, -16.3) * mm, "end": v(36.68, -21.3) * mm});
            skLineSegment(sketch, "E4.2.0.32", {"start": v(172.68, -21.3) * mm, "end": v(177.68, -21.3) * mm});
            skLineSegment(sketch, "E4.2.0.33", {"start": v(91.08, -16.3) * mm, "end": v(91.08, -21.3) * mm});
            skLineSegment(sketch, "E4.2.0.34", {"start": v(77.48, -16.3) * mm, "end": v(82.48, -16.3) * mm});
            skLineSegment(sketch, "E4.2.0.35", {"start": v(70.68, -16.3) * mm, "end": v(70.68, -21.3) * mm});
            skLineSegment(sketch, "E4.2.0.36", {"start": v(57.08, -21.3) * mm, "end": v(62.08, -21.3) * mm});
            skLineSegment(sketch, "E4.2.0.37", {"start": v(111.48, -16.3) * mm, "end": v(111.48, -21.3) * mm});
            skLineSegment(sketch, "E4.2.0.38", {"start": v(150.48, -16.3) * mm, "end": v(150.48, -21.3) * mm});
            skLineSegment(sketch, "E4.2.0.39", {"start": v(177.68, -16.3) * mm, "end": v(177.68, -21.3) * mm});
            skLineSegment(sketch, "E4.2.0.40", {"start": v(179.48, -16.3) * mm, "end": v(179.48, -21.3) * mm});
            skLineSegment(sketch, "E4.2.0.41", {"start": v(97.88, -16.3) * mm, "end": v(97.88, -21.3) * mm});
            skLineSegment(sketch, "E4.2.0.42", {"start": v(36.68, -16.3) * mm, "end": v(41.68, -16.3) * mm});
            skLineSegment(sketch, "E4.2.0.43", {"start": v(118.28, -21.3) * mm, "end": v(123.28, -21.3) * mm});
            skLineSegment(sketch, "E4.2.0.44", {"start": v(7.68, -16.3) * mm, "end": v(7.68, -21.3) * mm});
            skLineSegment(sketch, "E4.2.0.45", {"start": v(43.48, -16.3) * mm, "end": v(43.48, -21.3) * mm});
            skLineSegment(sketch, "E4.2.0.46", {"start": v(77.48, -21.3) * mm, "end": v(82.48, -21.3) * mm});
            skLineSegment(sketch, "E4.2.0.47", {"start": v(138.68, -16.3) * mm, "end": v(143.68, -16.3) * mm});
            skLineSegment(sketch, "E4.2.0.48", {"start": v(23.08, -16.3) * mm, "end": v(28.08, -16.3) * mm});
            skLineSegment(sketch, "E4.2.0.49", {"start": v(152.28, -16.3) * mm, "end": v(152.28, -21.3) * mm});
            skLineSegment(sketch, "E4.2.0.50", {"start": v(57.08, -16.3) * mm, "end": v(62.08, -16.3) * mm});
            skLineSegment(sketch, "E4.2.0.51", {"start": v(43.48, -16.3) * mm, "end": v(48.48, -16.3) * mm});
            skLineSegment(sketch, "E4.2.0.52", {"start": v(41.68, -16.3) * mm, "end": v(41.68, -21.3) * mm});
            skLineSegment(sketch, "E4.2.0.53", {"start": v(125.08, -21.3) * mm, "end": v(130.08, -21.3) * mm});
            skLineSegment(sketch, "E4.2.0.54", {"start": v(186.28, -21.3) * mm, "end": v(191.28, -21.3) * mm});
            skLineSegment(sketch, "E4.2.0.55", {"start": v(125.08, -16.3) * mm, "end": v(125.08, -21.3) * mm});
            skLineSegment(sketch, "E4.2.0.56", {"start": v(63.88, -16.3) * mm, "end": v(68.88, -16.3) * mm});
            skLineSegment(sketch, "E4.2.0.57", {"start": v(63.88, -21.3) * mm, "end": v(68.88, -21.3) * mm});
            skLineSegment(sketch, "E4.2.0.58", {"start": v(164.08, -16.3) * mm, "end": v(164.08, -21.3) * mm});
            skLineSegment(sketch, "E4.2.0.59", {"start": v(186.28, -16.3) * mm, "end": v(186.28, -21.3) * mm});
            skLineSegment(sketch, "E4.2.0.60", {"start": v(9.48, -16.3) * mm, "end": v(9.48, -21.3) * mm});
            skLineSegment(sketch, "E4.2.0.61", {"start": v(84.28, -16.3) * mm, "end": v(89.28, -16.3) * mm});
            skLineSegment(sketch, "E4.2.0.62", {"start": v(9.48, -16.3) * mm, "end": v(14.48, -16.3) * mm});
            skLineSegment(sketch, "E4.2.0.63", {"start": v(50.28, -16.3) * mm, "end": v(55.28, -16.3) * mm});
            skLineSegment(sketch, "E4.2.0.64", {"start": v(109.68, -16.3) * mm, "end": v(109.68, -21.3) * mm});
            skLineSegment(sketch, "E4.2.0.65", {"start": v(91.08, -21.3) * mm, "end": v(96.08, -21.3) * mm});
            skLineSegment(sketch, "E4.2.0.66", {"start": v(102.88, -16.3) * mm, "end": v(102.88, -21.3) * mm});
            skLineSegment(sketch, "E4.2.0.67", {"start": v(2.68, -16.3) * mm, "end": v(7.68, -16.3) * mm});
            skLineSegment(sketch, "E4.2.0.68", {"start": v(97.88, -21.3) * mm, "end": v(102.88, -21.3) * mm});
            skLineSegment(sketch, "E4.2.0.69", {"start": v(123.28, -16.3) * mm, "end": v(123.28, -21.3) * mm});
            skLineSegment(sketch, "E4.2.0.70", {"start": v(84.28, -21.3) * mm, "end": v(89.28, -21.3) * mm});
            skLineSegment(sketch, "E4.2.0.71", {"start": v(16.28, -16.3) * mm, "end": v(21.28, -16.3) * mm});
            skLineSegment(sketch, "E4.2.0.72", {"start": v(29.88, -16.3) * mm, "end": v(34.88, -16.3) * mm});
            skLineSegment(sketch, "E4.2.0.73", {"start": v(77.48, -16.3) * mm, "end": v(77.48, -21.3) * mm});
            skLineSegment(sketch, "E4.2.0.74", {"start": v(2.68, -16.3) * mm, "end": v(2.68, -21.3) * mm});
            skLineSegment(sketch, "E4.2.0.75", {"start": v(29.88, -16.3) * mm, "end": v(29.88, -21.3) * mm});
            skLineSegment(sketch, "E4.2.0.76", {"start": v(159.08, -16.3) * mm, "end": v(159.08, -21.3) * mm});
            skLineSegment(sketch, "E4.2.0.77", {"start": v(104.68, -16.3) * mm, "end": v(109.68, -16.3) * mm});
            skLineSegment(sketch, "E4.2.0.78", {"start": v(82.48, -16.3) * mm, "end": v(82.48, -21.3) * mm});
            skLineSegment(sketch, "E4.2.0.79", {"start": v(34.88, -16.3) * mm, "end": v(34.88, -21.3) * mm});
            skLineSegment(sketch, "E4.2.0.80", {"start": v(157.28, -16.3) * mm, "end": v(157.28, -21.3) * mm});
            skLineSegment(sketch, "E4.2.0.81", {"start": v(21.28, -16.3) * mm, "end": v(21.28, -21.3) * mm});
            skLineSegment(sketch, "E4.2.0.82", {"start": v(143.68, -16.3) * mm, "end": v(143.68, -21.3) * mm});
            skLineSegment(sketch, "E4.2.0.83", {"start": v(138.68, -16.3) * mm, "end": v(138.68, -21.3) * mm});
            skLineSegment(sketch, "E4.2.0.84", {"start": v(130.08, -16.3) * mm, "end": v(130.08, -21.3) * mm});
            skLineSegment(sketch, "E4.2.0.85", {"start": v(57.08, -16.3) * mm, "end": v(57.08, -21.3) * mm});
            skLineSegment(sketch, "E4.2.0.86", {"start": v(136.88, -16.3) * mm, "end": v(136.88, -21.3) * mm});
            skLineSegment(sketch, "E4.2.0.87", {"start": v(118.28, -16.3) * mm, "end": v(118.28, -21.3) * mm});
            skLineSegment(sketch, "E4.2.0.88", {"start": v(96.08, -16.3) * mm, "end": v(96.08, -21.3) * mm});
            skLineSegment(sketch, "E4.2.0.89", {"start": v(145.48, -21.3) * mm, "end": v(150.48, -21.3) * mm});
            skLineSegment(sketch, "E4.2.0.90", {"start": v(165.88, -21.3) * mm, "end": v(170.88, -21.3) * mm});
            skLineSegment(sketch, "E4.2.0.91", {"start": v(50.28, -16.3) * mm, "end": v(50.28, -21.3) * mm});
            skLineSegment(sketch, "E4.2.0.92", {"start": v(118.28, -16.3) * mm, "end": v(123.28, -16.3) * mm});
            skLineSegment(sketch, "E4.2.0.93", {"start": v(131.88, -16.3) * mm, "end": v(131.88, -21.3) * mm});
            skLineSegment(sketch, "E4.2.0.94", {"start": v(16.28, -16.3) * mm, "end": v(16.28, -21.3) * mm});
            skLineSegment(sketch, "E4.2.0.95", {"start": v(104.68, -16.3) * mm, "end": v(104.68, -21.3) * mm});
            skLineSegment(sketch, "E4.2.0.96", {"start": v(111.48, -21.3) * mm, "end": v(116.48, -21.3) * mm});
            skLineSegment(sketch, "E4.2.0.97", {"start": v(89.28, -16.3) * mm, "end": v(89.28, -21.3) * mm});
            skLineSegment(sketch, "E4.2.0.98", {"start": v(152.28, -16.3) * mm, "end": v(157.28, -16.3) * mm});
            skLineSegment(sketch, "E4.2.0.99", {"start": v(186.28, -16.3) * mm, "end": v(191.28, -16.3) * mm});
            skLineSegment(sketch, "E4.2.0.100", {"start": v(36.68, -21.3) * mm, "end": v(41.68, -21.3) * mm});
            skLineSegment(sketch, "E4.2.0.101", {"start": v(43.48, -21.3) * mm, "end": v(48.48, -21.3) * mm});
            skLineSegment(sketch, "E4.2.0.102", {"start": v(2.68, -21.3) * mm, "end": v(9.48, -21.3) * mm, "construction": true});
            skLineSegment(sketch, "E4.2.0.103", {"start": v(159.08, -16.3) * mm, "end": v(164.08, -16.3) * mm});
            skLineSegment(sketch, "E4.2.0.104", {"start": v(165.88, -16.3) * mm, "end": v(170.88, -16.3) * mm});
            skLineSegment(sketch, "E4.2.0.105", {"start": v(172.68, -16.3) * mm, "end": v(177.68, -16.3) * mm});
            skLineSegment(sketch, "E4.2.0.106", {"start": v(16.28, -21.3) * mm, "end": v(21.28, -21.3) * mm});
            skLineSegment(sketch, "E4.2.0.107", {"start": v(29.88, -21.3) * mm, "end": v(34.88, -21.3) * mm});
            skLineSegment(sketch, "E4.2.0.108", {"start": v(23.08, -21.3) * mm, "end": v(28.08, -21.3) * mm});
            skLineSegment(sketch, "E4.2.0.109", {"start": v(9.48, -21.3) * mm, "end": v(14.48, -21.3) * mm});
            skLineSegment(sketch, "E4.2.0.110", {"start": v(50.28, -21.3) * mm, "end": v(55.28, -21.3) * mm});
            skLineSegment(sketch, "E4.2.0.111", {"start": v(179.48, -16.3) * mm, "end": v(184.48, -16.3) * mm});
            skLineSegment(sketch, "E4.2.0.112", {"start": v(2.68, -21.3) * mm, "end": v(7.68, -21.3) * mm});
            skLineSegment(sketch, "E4.3.0.0", {"start": v(111.52, -23.3) * mm, "end": v(116.52, -23.3) * mm});
            skLineSegment(sketch, "E4.3.0.1", {"start": v(116.52, -23.3) * mm, "end": v(116.52, -28.3) * mm});
            skLineSegment(sketch, "E4.3.0.2", {"start": v(125.12, -23.3) * mm, "end": v(130.12, -23.3) * mm});
            skLineSegment(sketch, "E4.3.0.3", {"start": v(28.12, -23.3) * mm, "end": v(28.12, -28.3) * mm});
            skLineSegment(sketch, "E4.3.0.4", {"start": v(70.72, -23.3) * mm, "end": v(75.72, -23.3) * mm});
            skLineSegment(sketch, "E4.3.0.5", {"start": v(172.72, -23.3) * mm, "end": v(172.72, -28.3) * mm});
            skLineSegment(sketch, "E4.3.0.6", {"start": v(48.52, -23.3) * mm, "end": v(48.52, -28.3) * mm});
            skLineSegment(sketch, "E4.3.0.7", {"start": v(84.32, -23.3) * mm, "end": v(84.32, -28.3) * mm});
            skLineSegment(sketch, "E4.3.0.8", {"start": v(14.52, -23.3) * mm, "end": v(14.52, -28.3) * mm});
            skLineSegment(sketch, "E4.3.0.9", {"start": v(97.92, -23.3) * mm, "end": v(102.92, -23.3) * mm});
            skLineSegment(sketch, "E4.3.0.10", {"start": v(165.92, -23.3) * mm, "end": v(165.92, -28.3) * mm});
            skLineSegment(sketch, "E4.3.0.11", {"start": v(91.12, -23.3) * mm, "end": v(96.12, -23.3) * mm});
            skLineSegment(sketch, "E4.3.0.12", {"start": v(70.72, -28.3) * mm, "end": v(75.72, -28.3) * mm});
            skLineSegment(sketch, "E4.3.0.13", {"start": v(131.92, -28.3) * mm, "end": v(136.92, -28.3) * mm});
            skLineSegment(sketch, "E4.3.0.14", {"start": v(145.52, -23.3) * mm, "end": v(145.52, -28.3) * mm});
            skLineSegment(sketch, "E4.3.0.15", {"start": v(104.72, -28.3) * mm, "end": v(109.72, -28.3) * mm});
            skLineSegment(sketch, "E4.3.0.16", {"start": v(191.32, -23.3) * mm, "end": v(191.32, -28.3) * mm});
            skLineSegment(sketch, "E4.3.0.17", {"start": v(159.12, -28.3) * mm, "end": v(164.12, -28.3) * mm});
            skLineSegment(sketch, "E4.3.0.18", {"start": v(75.72, -23.3) * mm, "end": v(75.72, -28.3) * mm});
            skLineSegment(sketch, "E4.3.0.19", {"start": v(23.12, -23.3) * mm, "end": v(23.12, -28.3) * mm});
            skLineSegment(sketch, "E4.3.0.20", {"start": v(145.52, -23.3) * mm, "end": v(150.52, -23.3) * mm});
            skLineSegment(sketch, "E4.3.0.21", {"start": v(138.72, -28.3) * mm, "end": v(143.72, -28.3) * mm});
            skLineSegment(sketch, "E4.3.0.22", {"start": v(184.52, -23.3) * mm, "end": v(184.52, -28.3) * mm});
            skLineSegment(sketch, "E4.3.0.23", {"start": v(55.32, -23.3) * mm, "end": v(55.32, -28.3) * mm});
            skLineSegment(sketch, "E4.3.0.24", {"start": v(170.92, -23.3) * mm, "end": v(170.92, -28.3) * mm});
            skLineSegment(sketch, "E4.3.0.25", {"start": v(62.12, -23.3) * mm, "end": v(62.12, -28.3) * mm});
            skLineSegment(sketch, "E4.3.0.26", {"start": v(68.92, -23.3) * mm, "end": v(68.92, -28.3) * mm});
            skLineSegment(sketch, "E4.3.0.27", {"start": v(131.92, -23.3) * mm, "end": v(136.92, -23.3) * mm});
            skLineSegment(sketch, "E4.3.0.28", {"start": v(63.92, -23.3) * mm, "end": v(63.92, -28.3) * mm});
            skLineSegment(sketch, "E4.3.0.29", {"start": v(152.32, -28.3) * mm, "end": v(157.32, -28.3) * mm});
            skLineSegment(sketch, "E4.3.0.30", {"start": v(179.52, -28.3) * mm, "end": v(184.52, -28.3) * mm});
            skLineSegment(sketch, "E4.3.0.31", {"start": v(36.72, -23.3) * mm, "end": v(36.72, -28.3) * mm});
            skLineSegment(sketch, "E4.3.0.32", {"start": v(172.72, -28.3) * mm, "end": v(177.72, -28.3) * mm});
            skLineSegment(sketch, "E4.3.0.33", {"start": v(91.12, -23.3) * mm, "end": v(91.12, -28.3) * mm});
            skLineSegment(sketch, "E4.3.0.34", {"start": v(77.52, -23.3) * mm, "end": v(82.52, -23.3) * mm});
            skLineSegment(sketch, "E4.3.0.35", {"start": v(70.72, -23.3) * mm, "end": v(70.72, -28.3) * mm});
            skLineSegment(sketch, "E4.3.0.36", {"start": v(57.12, -28.3) * mm, "end": v(62.12, -28.3) * mm});
            skLineSegment(sketch, "E4.3.0.37", {"start": v(111.52, -23.3) * mm, "end": v(111.52, -28.3) * mm});
            skLineSegment(sketch, "E4.3.0.38", {"start": v(150.52, -23.3) * mm, "end": v(150.52, -28.3) * mm});
            skLineSegment(sketch, "E4.3.0.39", {"start": v(177.72, -23.3) * mm, "end": v(177.72, -28.3) * mm});
            skLineSegment(sketch, "E4.3.0.40", {"start": v(179.52, -23.3) * mm, "end": v(179.52, -28.3) * mm});
            skLineSegment(sketch, "E4.3.0.41", {"start": v(97.92, -23.3) * mm, "end": v(97.92, -28.3) * mm});
            skLineSegment(sketch, "E4.3.0.42", {"start": v(36.72, -23.3) * mm, "end": v(41.72, -23.3) * mm});
            skLineSegment(sketch, "E4.3.0.43", {"start": v(118.32, -28.3) * mm, "end": v(123.32, -28.3) * mm});
            skLineSegment(sketch, "E4.3.0.44", {"start": v(7.72, -23.3) * mm, "end": v(7.72, -28.3) * mm});
            skLineSegment(sketch, "E4.3.0.45", {"start": v(43.52, -23.3) * mm, "end": v(43.52, -28.3) * mm});
            skLineSegment(sketch, "E4.3.0.46", {"start": v(77.52, -28.3) * mm, "end": v(82.52, -28.3) * mm});
            skLineSegment(sketch, "E4.3.0.47", {"start": v(138.72, -23.3) * mm, "end": v(143.72, -23.3) * mm});
            skLineSegment(sketch, "E4.3.0.48", {"start": v(23.12, -23.3) * mm, "end": v(28.12, -23.3) * mm});
            skLineSegment(sketch, "E4.3.0.49", {"start": v(152.32, -23.3) * mm, "end": v(152.32, -28.3) * mm});
            skLineSegment(sketch, "E4.3.0.50", {"start": v(57.12, -23.3) * mm, "end": v(62.12, -23.3) * mm});
            skLineSegment(sketch, "E4.3.0.51", {"start": v(43.52, -23.3) * mm, "end": v(48.52, -23.3) * mm});
            skLineSegment(sketch, "E4.3.0.52", {"start": v(41.72, -23.3) * mm, "end": v(41.72, -28.3) * mm});
            skLineSegment(sketch, "E4.3.0.53", {"start": v(125.12, -28.3) * mm, "end": v(130.12, -28.3) * mm});
            skLineSegment(sketch, "E4.3.0.54", {"start": v(186.32, -28.3) * mm, "end": v(191.32, -28.3) * mm});
            skLineSegment(sketch, "E4.3.0.55", {"start": v(125.12, -23.3) * mm, "end": v(125.12, -28.3) * mm});
            skLineSegment(sketch, "E4.3.0.56", {"start": v(63.92, -23.3) * mm, "end": v(68.92, -23.3) * mm});
            skLineSegment(sketch, "E4.3.0.57", {"start": v(63.92, -28.3) * mm, "end": v(68.92, -28.3) * mm});
            skLineSegment(sketch, "E4.3.0.58", {"start": v(164.12, -23.3) * mm, "end": v(164.12, -28.3) * mm});
            skLineSegment(sketch, "E4.3.0.59", {"start": v(186.32, -23.3) * mm, "end": v(186.32, -28.3) * mm});
            skLineSegment(sketch, "E4.3.0.60", {"start": v(9.52, -23.3) * mm, "end": v(9.52, -28.3) * mm});
            skLineSegment(sketch, "E4.3.0.61", {"start": v(84.32, -23.3) * mm, "end": v(89.32, -23.3) * mm});
            skLineSegment(sketch, "E4.3.0.62", {"start": v(9.52, -23.3) * mm, "end": v(14.52, -23.3) * mm});
            skLineSegment(sketch, "E4.3.0.63", {"start": v(50.32, -23.3) * mm, "end": v(55.32, -23.3) * mm});
            skLineSegment(sketch, "E4.3.0.64", {"start": v(109.72, -23.3) * mm, "end": v(109.72, -28.3) * mm});
            skLineSegment(sketch, "E4.3.0.65", {"start": v(91.12, -28.3) * mm, "end": v(96.12, -28.3) * mm});
            skLineSegment(sketch, "E4.3.0.66", {"start": v(102.92, -23.3) * mm, "end": v(102.92, -28.3) * mm});
            skLineSegment(sketch, "E4.3.0.67", {"start": v(2.72, -23.3) * mm, "end": v(7.72, -23.3) * mm});
            skLineSegment(sketch, "E4.3.0.68", {"start": v(97.92, -28.3) * mm, "end": v(102.92, -28.3) * mm});
            skLineSegment(sketch, "E4.3.0.69", {"start": v(123.32, -23.3) * mm, "end": v(123.32, -28.3) * mm});
            skLineSegment(sketch, "E4.3.0.70", {"start": v(84.32, -28.3) * mm, "end": v(89.32, -28.3) * mm});
            skLineSegment(sketch, "E4.3.0.71", {"start": v(16.32, -23.3) * mm, "end": v(21.32, -23.3) * mm});
            skLineSegment(sketch, "E4.3.0.72", {"start": v(29.92, -23.3) * mm, "end": v(34.92, -23.3) * mm});
            skLineSegment(sketch, "E4.3.0.73", {"start": v(77.52, -23.3) * mm, "end": v(77.52, -28.3) * mm});
            skLineSegment(sketch, "E4.3.0.74", {"start": v(2.72, -23.3) * mm, "end": v(2.72, -28.3) * mm});
            skLineSegment(sketch, "E4.3.0.75", {"start": v(29.92, -23.3) * mm, "end": v(29.92, -28.3) * mm});
            skLineSegment(sketch, "E4.3.0.76", {"start": v(159.12, -23.3) * mm, "end": v(159.12, -28.3) * mm});
            skLineSegment(sketch, "E4.3.0.77", {"start": v(104.72, -23.3) * mm, "end": v(109.72, -23.3) * mm});
            skLineSegment(sketch, "E4.3.0.78", {"start": v(82.52, -23.3) * mm, "end": v(82.52, -28.3) * mm});
            skLineSegment(sketch, "E4.3.0.79", {"start": v(34.92, -23.3) * mm, "end": v(34.92, -28.3) * mm});
            skLineSegment(sketch, "E4.3.0.80", {"start": v(157.32, -23.3) * mm, "end": v(157.32, -28.3) * mm});
            skLineSegment(sketch, "E4.3.0.81", {"start": v(21.32, -23.3) * mm, "end": v(21.32, -28.3) * mm});
            skLineSegment(sketch, "E4.3.0.82", {"start": v(143.72, -23.3) * mm, "end": v(143.72, -28.3) * mm});
            skLineSegment(sketch, "E4.3.0.83", {"start": v(138.72, -23.3) * mm, "end": v(138.72, -28.3) * mm});
            skLineSegment(sketch, "E4.3.0.84", {"start": v(130.12, -23.3) * mm, "end": v(130.12, -28.3) * mm});
            skLineSegment(sketch, "E4.3.0.85", {"start": v(57.12, -23.3) * mm, "end": v(57.12, -28.3) * mm});
            skLineSegment(sketch, "E4.3.0.86", {"start": v(136.92, -23.3) * mm, "end": v(136.92, -28.3) * mm});
            skLineSegment(sketch, "E4.3.0.87", {"start": v(118.32, -23.3) * mm, "end": v(118.32, -28.3) * mm});
            skLineSegment(sketch, "E4.3.0.88", {"start": v(96.12, -23.3) * mm, "end": v(96.12, -28.3) * mm});
            skLineSegment(sketch, "E4.3.0.89", {"start": v(145.52, -28.3) * mm, "end": v(150.52, -28.3) * mm});
            skLineSegment(sketch, "E4.3.0.90", {"start": v(165.92, -28.3) * mm, "end": v(170.92, -28.3) * mm});
            skLineSegment(sketch, "E4.3.0.91", {"start": v(50.32, -23.3) * mm, "end": v(50.32, -28.3) * mm});
            skLineSegment(sketch, "E4.3.0.92", {"start": v(118.32, -23.3) * mm, "end": v(123.32, -23.3) * mm});
            skLineSegment(sketch, "E4.3.0.93", {"start": v(131.92, -23.3) * mm, "end": v(131.92, -28.3) * mm});
            skLineSegment(sketch, "E4.3.0.94", {"start": v(16.32, -23.3) * mm, "end": v(16.32, -28.3) * mm});
            skLineSegment(sketch, "E4.3.0.95", {"start": v(104.72, -23.3) * mm, "end": v(104.72, -28.3) * mm});
            skLineSegment(sketch, "E4.3.0.96", {"start": v(111.52, -28.3) * mm, "end": v(116.52, -28.3) * mm});
            skLineSegment(sketch, "E4.3.0.97", {"start": v(89.32, -23.3) * mm, "end": v(89.32, -28.3) * mm});
            skLineSegment(sketch, "E4.3.0.98", {"start": v(152.32, -23.3) * mm, "end": v(157.32, -23.3) * mm});
            skLineSegment(sketch, "E4.3.0.99", {"start": v(186.32, -23.3) * mm, "end": v(191.32, -23.3) * mm});
            skLineSegment(sketch, "E4.3.0.100", {"start": v(36.72, -28.3) * mm, "end": v(41.72, -28.3) * mm});
            skLineSegment(sketch, "E4.3.0.101", {"start": v(43.52, -28.3) * mm, "end": v(48.52, -28.3) * mm});
            skLineSegment(sketch, "E4.3.0.102", {"start": v(2.72, -28.3) * mm, "end": v(9.52, -28.3) * mm, "construction": true});
            skLineSegment(sketch, "E4.3.0.103", {"start": v(159.12, -23.3) * mm, "end": v(164.12, -23.3) * mm});
            skLineSegment(sketch, "E4.3.0.104", {"start": v(165.92, -23.3) * mm, "end": v(170.92, -23.3) * mm});
            skLineSegment(sketch, "E4.3.0.105", {"start": v(172.72, -23.3) * mm, "end": v(177.72, -23.3) * mm});
            skLineSegment(sketch, "E4.3.0.106", {"start": v(16.32, -28.3) * mm, "end": v(21.32, -28.3) * mm});
            skLineSegment(sketch, "E4.3.0.107", {"start": v(29.92, -28.3) * mm, "end": v(34.92, -28.3) * mm});
            skLineSegment(sketch, "E4.3.0.108", {"start": v(23.12, -28.3) * mm, "end": v(28.12, -28.3) * mm});
            skLineSegment(sketch, "E4.3.0.109", {"start": v(9.52, -28.3) * mm, "end": v(14.52, -28.3) * mm});
            skLineSegment(sketch, "E4.3.0.110", {"start": v(50.32, -28.3) * mm, "end": v(55.32, -28.3) * mm});
            skLineSegment(sketch, "E4.3.0.111", {"start": v(179.52, -23.3) * mm, "end": v(184.52, -23.3) * mm});
            skLineSegment(sketch, "E4.3.0.112", {"start": v(2.72, -28.3) * mm, "end": v(7.72, -28.3) * mm});
            skLineSegment(sketch, "E4.4.0.0", {"start": v(111.57, -30.3) * mm, "end": v(116.57, -30.3) * mm});
            skLineSegment(sketch, "E4.4.0.1", {"start": v(116.57, -30.3) * mm, "end": v(116.57, -35.3) * mm});
            skLineSegment(sketch, "E4.4.0.2", {"start": v(125.17, -30.3) * mm, "end": v(130.17, -30.3) * mm});
            skLineSegment(sketch, "E4.4.0.3", {"start": v(28.17, -30.3) * mm, "end": v(28.17, -35.3) * mm});
            skLineSegment(sketch, "E4.4.0.4", {"start": v(70.77, -30.3) * mm, "end": v(75.77, -30.3) * mm});
            skLineSegment(sketch, "E4.4.0.5", {"start": v(172.77, -30.3) * mm, "end": v(172.77, -35.3) * mm});
            skLineSegment(sketch, "E4.4.0.6", {"start": v(48.57, -30.3) * mm, "end": v(48.57, -35.3) * mm});
            skLineSegment(sketch, "E4.4.0.7", {"start": v(84.37, -30.3) * mm, "end": v(84.37, -35.3) * mm});
            skLineSegment(sketch, "E4.4.0.8", {"start": v(14.57, -30.3) * mm, "end": v(14.57, -35.3) * mm});
            skLineSegment(sketch, "E4.4.0.9", {"start": v(97.97, -30.3) * mm, "end": v(102.97, -30.3) * mm});
            skLineSegment(sketch, "E4.4.0.10", {"start": v(165.97, -30.3) * mm, "end": v(165.97, -35.3) * mm});
            skLineSegment(sketch, "E4.4.0.11", {"start": v(91.17, -30.3) * mm, "end": v(96.17, -30.3) * mm});
            skLineSegment(sketch, "E4.4.0.12", {"start": v(70.77, -35.3) * mm, "end": v(75.77, -35.3) * mm});
            skLineSegment(sketch, "E4.4.0.13", {"start": v(131.97, -35.3) * mm, "end": v(136.97, -35.3) * mm});
            skLineSegment(sketch, "E4.4.0.14", {"start": v(145.57, -30.3) * mm, "end": v(145.57, -35.3) * mm});
            skLineSegment(sketch, "E4.4.0.15", {"start": v(104.77, -35.3) * mm, "end": v(109.77, -35.3) * mm});
            skLineSegment(sketch, "E4.4.0.16", {"start": v(191.37, -30.3) * mm, "end": v(191.37, -35.3) * mm});
            skLineSegment(sketch, "E4.4.0.17", {"start": v(159.17, -35.3) * mm, "end": v(164.17, -35.3) * mm});
            skLineSegment(sketch, "E4.4.0.18", {"start": v(75.77, -30.3) * mm, "end": v(75.77, -35.3) * mm});
            skLineSegment(sketch, "E4.4.0.19", {"start": v(23.17, -30.3) * mm, "end": v(23.17, -35.3) * mm});
            skLineSegment(sketch, "E4.4.0.20", {"start": v(145.57, -30.3) * mm, "end": v(150.57, -30.3) * mm});
            skLineSegment(sketch, "E4.4.0.21", {"start": v(138.77, -35.3) * mm, "end": v(143.77, -35.3) * mm});
            skLineSegment(sketch, "E4.4.0.22", {"start": v(184.57, -30.3) * mm, "end": v(184.57, -35.3) * mm});
            skLineSegment(sketch, "E4.4.0.23", {"start": v(55.37, -30.3) * mm, "end": v(55.37, -35.3) * mm});
            skLineSegment(sketch, "E4.4.0.24", {"start": v(170.97, -30.3) * mm, "end": v(170.97, -35.3) * mm});
            skLineSegment(sketch, "E4.4.0.25", {"start": v(62.17, -30.3) * mm, "end": v(62.17, -35.3) * mm});
            skLineSegment(sketch, "E4.4.0.26", {"start": v(68.97, -30.3) * mm, "end": v(68.97, -35.3) * mm});
            skLineSegment(sketch, "E4.4.0.27", {"start": v(131.97, -30.3) * mm, "end": v(136.97, -30.3) * mm});
            skLineSegment(sketch, "E4.4.0.28", {"start": v(63.97, -30.3) * mm, "end": v(63.97, -35.3) * mm});
            skLineSegment(sketch, "E4.4.0.29", {"start": v(152.37, -35.3) * mm, "end": v(157.37, -35.3) * mm});
            skLineSegment(sketch, "E4.4.0.30", {"start": v(179.57, -35.3) * mm, "end": v(184.57, -35.3) * mm});
            skLineSegment(sketch, "E4.4.0.31", {"start": v(36.77, -30.3) * mm, "end": v(36.77, -35.3) * mm});
            skLineSegment(sketch, "E4.4.0.32", {"start": v(172.77, -35.3) * mm, "end": v(177.77, -35.3) * mm});
            skLineSegment(sketch, "E4.4.0.33", {"start": v(91.17, -30.3) * mm, "end": v(91.17, -35.3) * mm});
            skLineSegment(sketch, "E4.4.0.34", {"start": v(77.57, -30.3) * mm, "end": v(82.57, -30.3) * mm});
            skLineSegment(sketch, "E4.4.0.35", {"start": v(70.77, -30.3) * mm, "end": v(70.77, -35.3) * mm});
            skLineSegment(sketch, "E4.4.0.36", {"start": v(57.17, -35.3) * mm, "end": v(62.17, -35.3) * mm});
            skLineSegment(sketch, "E4.4.0.37", {"start": v(111.57, -30.3) * mm, "end": v(111.57, -35.3) * mm});
            skLineSegment(sketch, "E4.4.0.38", {"start": v(150.57, -30.3) * mm, "end": v(150.57, -35.3) * mm});
            skLineSegment(sketch, "E4.4.0.39", {"start": v(177.77, -30.3) * mm, "end": v(177.77, -35.3) * mm});
            skLineSegment(sketch, "E4.4.0.40", {"start": v(179.57, -30.3) * mm, "end": v(179.57, -35.3) * mm});
            skLineSegment(sketch, "E4.4.0.41", {"start": v(97.97, -30.3) * mm, "end": v(97.97, -35.3) * mm});
            skLineSegment(sketch, "E4.4.0.42", {"start": v(36.77, -30.3) * mm, "end": v(41.77, -30.3) * mm});
            skLineSegment(sketch, "E4.4.0.43", {"start": v(118.37, -35.3) * mm, "end": v(123.37, -35.3) * mm});
            skLineSegment(sketch, "E4.4.0.44", {"start": v(7.77, -30.3) * mm, "end": v(7.77, -35.3) * mm});
            skLineSegment(sketch, "E4.4.0.45", {"start": v(43.57, -30.3) * mm, "end": v(43.57, -35.3) * mm});
            skLineSegment(sketch, "E4.4.0.46", {"start": v(77.57, -35.3) * mm, "end": v(82.57, -35.3) * mm});
            skLineSegment(sketch, "E4.4.0.47", {"start": v(138.77, -30.3) * mm, "end": v(143.77, -30.3) * mm});
            skLineSegment(sketch, "E4.4.0.48", {"start": v(23.17, -30.3) * mm, "end": v(28.17, -30.3) * mm});
            skLineSegment(sketch, "E4.4.0.49", {"start": v(152.37, -30.3) * mm, "end": v(152.37, -35.3) * mm});
            skLineSegment(sketch, "E4.4.0.50", {"start": v(57.17, -30.3) * mm, "end": v(62.17, -30.3) * mm});
            skLineSegment(sketch, "E4.4.0.51", {"start": v(43.57, -30.3) * mm, "end": v(48.57, -30.3) * mm});
            skLineSegment(sketch, "E4.4.0.52", {"start": v(41.77, -30.3) * mm, "end": v(41.77, -35.3) * mm});
            skLineSegment(sketch, "E4.4.0.53", {"start": v(125.17, -35.3) * mm, "end": v(130.17, -35.3) * mm});
            skLineSegment(sketch, "E4.4.0.54", {"start": v(186.37, -35.3) * mm, "end": v(191.37, -35.3) * mm});
            skLineSegment(sketch, "E4.4.0.55", {"start": v(125.17, -30.3) * mm, "end": v(125.17, -35.3) * mm});
            skLineSegment(sketch, "E4.4.0.56", {"start": v(63.97, -30.3) * mm, "end": v(68.97, -30.3) * mm});
            skLineSegment(sketch, "E4.4.0.57", {"start": v(63.97, -35.3) * mm, "end": v(68.97, -35.3) * mm});
            skLineSegment(sketch, "E4.4.0.58", {"start": v(164.17, -30.3) * mm, "end": v(164.17, -35.3) * mm});
            skLineSegment(sketch, "E4.4.0.59", {"start": v(186.37, -30.3) * mm, "end": v(186.37, -35.3) * mm});
            skLineSegment(sketch, "E4.4.0.60", {"start": v(9.57, -30.3) * mm, "end": v(9.57, -35.3) * mm});
            skLineSegment(sketch, "E4.4.0.61", {"start": v(84.37, -30.3) * mm, "end": v(89.37, -30.3) * mm});
            skLineSegment(sketch, "E4.4.0.62", {"start": v(9.57, -30.3) * mm, "end": v(14.57, -30.3) * mm});
            skLineSegment(sketch, "E4.4.0.63", {"start": v(50.37, -30.3) * mm, "end": v(55.37, -30.3) * mm});
            skLineSegment(sketch, "E4.4.0.64", {"start": v(109.77, -30.3) * mm, "end": v(109.77, -35.3) * mm});
            skLineSegment(sketch, "E4.4.0.65", {"start": v(91.17, -35.3) * mm, "end": v(96.17, -35.3) * mm});
            skLineSegment(sketch, "E4.4.0.66", {"start": v(102.97, -30.3) * mm, "end": v(102.97, -35.3) * mm});
            skLineSegment(sketch, "E4.4.0.67", {"start": v(2.77, -30.3) * mm, "end": v(7.77, -30.3) * mm});
            skLineSegment(sketch, "E4.4.0.68", {"start": v(97.97, -35.3) * mm, "end": v(102.97, -35.3) * mm});
            skLineSegment(sketch, "E4.4.0.69", {"start": v(123.37, -30.3) * mm, "end": v(123.37, -35.3) * mm});
            skLineSegment(sketch, "E4.4.0.70", {"start": v(84.37, -35.3) * mm, "end": v(89.37, -35.3) * mm});
            skLineSegment(sketch, "E4.4.0.71", {"start": v(16.37, -30.3) * mm, "end": v(21.37, -30.3) * mm});
            skLineSegment(sketch, "E4.4.0.72", {"start": v(29.97, -30.3) * mm, "end": v(34.97, -30.3) * mm});
            skLineSegment(sketch, "E4.4.0.73", {"start": v(77.57, -30.3) * mm, "end": v(77.57, -35.3) * mm});
            skLineSegment(sketch, "E4.4.0.74", {"start": v(2.77, -30.3) * mm, "end": v(2.77, -35.3) * mm});
            skLineSegment(sketch, "E4.4.0.75", {"start": v(29.97, -30.3) * mm, "end": v(29.97, -35.3) * mm});
            skLineSegment(sketch, "E4.4.0.76", {"start": v(159.17, -30.3) * mm, "end": v(159.17, -35.3) * mm});
            skLineSegment(sketch, "E4.4.0.77", {"start": v(104.77, -30.3) * mm, "end": v(109.77, -30.3) * mm});
            skLineSegment(sketch, "E4.4.0.78", {"start": v(82.57, -30.3) * mm, "end": v(82.57, -35.3) * mm});
            skLineSegment(sketch, "E4.4.0.79", {"start": v(34.97, -30.3) * mm, "end": v(34.97, -35.3) * mm});
            skLineSegment(sketch, "E4.4.0.80", {"start": v(157.37, -30.3) * mm, "end": v(157.37, -35.3) * mm});
            skLineSegment(sketch, "E4.4.0.81", {"start": v(21.37, -30.3) * mm, "end": v(21.37, -35.3) * mm});
            skLineSegment(sketch, "E4.4.0.82", {"start": v(143.77, -30.3) * mm, "end": v(143.77, -35.3) * mm});
            skLineSegment(sketch, "E4.4.0.83", {"start": v(138.77, -30.3) * mm, "end": v(138.77, -35.3) * mm});
            skLineSegment(sketch, "E4.4.0.84", {"start": v(130.17, -30.3) * mm, "end": v(130.17, -35.3) * mm});
            skLineSegment(sketch, "E4.4.0.85", {"start": v(57.17, -30.3) * mm, "end": v(57.17, -35.3) * mm});
            skLineSegment(sketch, "E4.4.0.86", {"start": v(136.97, -30.3) * mm, "end": v(136.97, -35.3) * mm});
            skLineSegment(sketch, "E4.4.0.87", {"start": v(118.37, -30.3) * mm, "end": v(118.37, -35.3) * mm});
            skLineSegment(sketch, "E4.4.0.88", {"start": v(96.17, -30.3) * mm, "end": v(96.17, -35.3) * mm});
            skLineSegment(sketch, "E4.4.0.89", {"start": v(145.57, -35.3) * mm, "end": v(150.57, -35.3) * mm});
            skLineSegment(sketch, "E4.4.0.90", {"start": v(165.97, -35.3) * mm, "end": v(170.97, -35.3) * mm});
            skLineSegment(sketch, "E4.4.0.91", {"start": v(50.37, -30.3) * mm, "end": v(50.37, -35.3) * mm});
            skLineSegment(sketch, "E4.4.0.92", {"start": v(118.37, -30.3) * mm, "end": v(123.37, -30.3) * mm});
            skLineSegment(sketch, "E4.4.0.93", {"start": v(131.97, -30.3) * mm, "end": v(131.97, -35.3) * mm});
            skLineSegment(sketch, "E4.4.0.94", {"start": v(16.37, -30.3) * mm, "end": v(16.37, -35.3) * mm});
            skLineSegment(sketch, "E4.4.0.95", {"start": v(104.77, -30.3) * mm, "end": v(104.77, -35.3) * mm});
            skLineSegment(sketch, "E4.4.0.96", {"start": v(111.57, -35.3) * mm, "end": v(116.57, -35.3) * mm});
            skLineSegment(sketch, "E4.4.0.97", {"start": v(89.37, -30.3) * mm, "end": v(89.37, -35.3) * mm});
            skLineSegment(sketch, "E4.4.0.98", {"start": v(152.37, -30.3) * mm, "end": v(157.37, -30.3) * mm});
            skLineSegment(sketch, "E4.4.0.99", {"start": v(186.37, -30.3) * mm, "end": v(191.37, -30.3) * mm});
            skLineSegment(sketch, "E4.4.0.100", {"start": v(36.77, -35.3) * mm, "end": v(41.77, -35.3) * mm});
            skLineSegment(sketch, "E4.4.0.101", {"start": v(43.57, -35.3) * mm, "end": v(48.57, -35.3) * mm});
            skLineSegment(sketch, "E4.4.0.102", {"start": v(2.77, -35.3) * mm, "end": v(9.57, -35.3) * mm, "construction": true});
            skLineSegment(sketch, "E4.4.0.103", {"start": v(159.17, -30.3) * mm, "end": v(164.17, -30.3) * mm});
            skLineSegment(sketch, "E4.4.0.104", {"start": v(165.97, -30.3) * mm, "end": v(170.97, -30.3) * mm});
            skLineSegment(sketch, "E4.4.0.105", {"start": v(172.77, -30.3) * mm, "end": v(177.77, -30.3) * mm});
            skLineSegment(sketch, "E4.4.0.106", {"start": v(16.37, -35.3) * mm, "end": v(21.37, -35.3) * mm});
            skLineSegment(sketch, "E4.4.0.107", {"start": v(29.97, -35.3) * mm, "end": v(34.97, -35.3) * mm});
            skLineSegment(sketch, "E4.4.0.108", {"start": v(23.17, -35.3) * mm, "end": v(28.17, -35.3) * mm});
            skLineSegment(sketch, "E4.4.0.109", {"start": v(9.57, -35.3) * mm, "end": v(14.57, -35.3) * mm});
            skLineSegment(sketch, "E4.4.0.110", {"start": v(50.37, -35.3) * mm, "end": v(55.37, -35.3) * mm});
            skLineSegment(sketch, "E4.4.0.111", {"start": v(179.57, -30.3) * mm, "end": v(184.57, -30.3) * mm});
            skLineSegment(sketch, "E4.4.0.112", {"start": v(2.77, -35.3) * mm, "end": v(7.77, -35.3) * mm});
            skLineSegment(sketch, "E4.5.0.0", {"start": v(111.61, -37.3) * mm, "end": v(116.61, -37.3) * mm});
            skLineSegment(sketch, "E4.5.0.1", {"start": v(116.61, -37.3) * mm, "end": v(116.61, -42.3) * mm});
            skLineSegment(sketch, "E4.5.0.2", {"start": v(125.21, -37.3) * mm, "end": v(130.21, -37.3) * mm});
            skLineSegment(sketch, "E4.5.0.3", {"start": v(28.21, -37.3) * mm, "end": v(28.21, -42.3) * mm});
            skLineSegment(sketch, "E4.5.0.4", {"start": v(70.81, -37.3) * mm, "end": v(75.81, -37.3) * mm});
            skLineSegment(sketch, "E4.5.0.5", {"start": v(172.81, -37.3) * mm, "end": v(172.81, -42.3) * mm});
            skLineSegment(sketch, "E4.5.0.6", {"start": v(48.61, -37.3) * mm, "end": v(48.61, -42.3) * mm});
            skLineSegment(sketch, "E4.5.0.7", {"start": v(84.41, -37.3) * mm, "end": v(84.41, -42.3) * mm});
            skLineSegment(sketch, "E4.5.0.8", {"start": v(14.61, -37.3) * mm, "end": v(14.61, -42.3) * mm});
            skLineSegment(sketch, "E4.5.0.9", {"start": v(98.01, -37.3) * mm, "end": v(103.01, -37.3) * mm});
            skLineSegment(sketch, "E4.5.0.10", {"start": v(166.01, -37.3) * mm, "end": v(166.01, -42.3) * mm});
            skLineSegment(sketch, "E4.5.0.11", {"start": v(91.21, -37.3) * mm, "end": v(96.21, -37.3) * mm});
            skLineSegment(sketch, "E4.5.0.12", {"start": v(70.81, -42.3) * mm, "end": v(75.81, -42.3) * mm});
            skLineSegment(sketch, "E4.5.0.13", {"start": v(132.01, -42.3) * mm, "end": v(137.01, -42.3) * mm});
            skLineSegment(sketch, "E4.5.0.14", {"start": v(145.61, -37.3) * mm, "end": v(145.61, -42.3) * mm});
            skLineSegment(sketch, "E4.5.0.15", {"start": v(104.81, -42.3) * mm, "end": v(109.81, -42.3) * mm});
            skLineSegment(sketch, "E4.5.0.16", {"start": v(191.41, -37.3) * mm, "end": v(191.41, -42.3) * mm});
            skLineSegment(sketch, "E4.5.0.17", {"start": v(159.21, -42.3) * mm, "end": v(164.21, -42.3) * mm});
            skLineSegment(sketch, "E4.5.0.18", {"start": v(75.81, -37.3) * mm, "end": v(75.81, -42.3) * mm});
            skLineSegment(sketch, "E4.5.0.19", {"start": v(23.21, -37.3) * mm, "end": v(23.21, -42.3) * mm});
            skLineSegment(sketch, "E4.5.0.20", {"start": v(145.61, -37.3) * mm, "end": v(150.61, -37.3) * mm});
            skLineSegment(sketch, "E4.5.0.21", {"start": v(138.81, -42.3) * mm, "end": v(143.81, -42.3) * mm});
            skLineSegment(sketch, "E4.5.0.22", {"start": v(184.61, -37.3) * mm, "end": v(184.61, -42.3) * mm});
            skLineSegment(sketch, "E4.5.0.23", {"start": v(55.41, -37.3) * mm, "end": v(55.41, -42.3) * mm});
            skLineSegment(sketch, "E4.5.0.24", {"start": v(171.01, -37.3) * mm, "end": v(171.01, -42.3) * mm});
            skLineSegment(sketch, "E4.5.0.25", {"start": v(62.21, -37.3) * mm, "end": v(62.21, -42.3) * mm});
            skLineSegment(sketch, "E4.5.0.26", {"start": v(69.01, -37.3) * mm, "end": v(69.01, -42.3) * mm});
            skLineSegment(sketch, "E4.5.0.27", {"start": v(132.01, -37.3) * mm, "end": v(137.01, -37.3) * mm});
            skLineSegment(sketch, "E4.5.0.28", {"start": v(64.01, -37.3) * mm, "end": v(64.01, -42.3) * mm});
            skLineSegment(sketch, "E4.5.0.29", {"start": v(152.41, -42.3) * mm, "end": v(157.41, -42.3) * mm});
            skLineSegment(sketch, "E4.5.0.30", {"start": v(179.61, -42.3) * mm, "end": v(184.61, -42.3) * mm});
            skLineSegment(sketch, "E4.5.0.31", {"start": v(36.81, -37.3) * mm, "end": v(36.81, -42.3) * mm});
            skLineSegment(sketch, "E4.5.0.32", {"start": v(172.81, -42.3) * mm, "end": v(177.81, -42.3) * mm});
            skLineSegment(sketch, "E4.5.0.33", {"start": v(91.21, -37.3) * mm, "end": v(91.21, -42.3) * mm});
            skLineSegment(sketch, "E4.5.0.34", {"start": v(77.61, -37.3) * mm, "end": v(82.61, -37.3) * mm});
            skLineSegment(sketch, "E4.5.0.35", {"start": v(70.81, -37.3) * mm, "end": v(70.81, -42.3) * mm});
            skLineSegment(sketch, "E4.5.0.36", {"start": v(57.21, -42.3) * mm, "end": v(62.21, -42.3) * mm});
            skLineSegment(sketch, "E4.5.0.37", {"start": v(111.61, -37.3) * mm, "end": v(111.61, -42.3) * mm});
            skLineSegment(sketch, "E4.5.0.38", {"start": v(150.61, -37.3) * mm, "end": v(150.61, -42.3) * mm});
            skLineSegment(sketch, "E4.5.0.39", {"start": v(177.81, -37.3) * mm, "end": v(177.81, -42.3) * mm});
            skLineSegment(sketch, "E4.5.0.40", {"start": v(179.61, -37.3) * mm, "end": v(179.61, -42.3) * mm});
            skLineSegment(sketch, "E4.5.0.41", {"start": v(98.01, -37.3) * mm, "end": v(98.01, -42.3) * mm});
            skLineSegment(sketch, "E4.5.0.42", {"start": v(36.81, -37.3) * mm, "end": v(41.81, -37.3) * mm});
            skLineSegment(sketch, "E4.5.0.43", {"start": v(118.41, -42.3) * mm, "end": v(123.41, -42.3) * mm});
            skLineSegment(sketch, "E4.5.0.44", {"start": v(7.81, -37.3) * mm, "end": v(7.81, -42.3) * mm});
            skLineSegment(sketch, "E4.5.0.45", {"start": v(43.61, -37.3) * mm, "end": v(43.61, -42.3) * mm});
            skLineSegment(sketch, "E4.5.0.46", {"start": v(77.61, -42.3) * mm, "end": v(82.61, -42.3) * mm});
            skLineSegment(sketch, "E4.5.0.47", {"start": v(138.81, -37.3) * mm, "end": v(143.81, -37.3) * mm});
            skLineSegment(sketch, "E4.5.0.48", {"start": v(23.21, -37.3) * mm, "end": v(28.21, -37.3) * mm});
            skLineSegment(sketch, "E4.5.0.49", {"start": v(152.41, -37.3) * mm, "end": v(152.41, -42.3) * mm});
            skLineSegment(sketch, "E4.5.0.50", {"start": v(57.21, -37.3) * mm, "end": v(62.21, -37.3) * mm});
            skLineSegment(sketch, "E4.5.0.51", {"start": v(43.61, -37.3) * mm, "end": v(48.61, -37.3) * mm});
            skLineSegment(sketch, "E4.5.0.52", {"start": v(41.81, -37.3) * mm, "end": v(41.81, -42.3) * mm});
            skLineSegment(sketch, "E4.5.0.53", {"start": v(125.21, -42.3) * mm, "end": v(130.21, -42.3) * mm});
            skLineSegment(sketch, "E4.5.0.54", {"start": v(186.41, -42.3) * mm, "end": v(191.41, -42.3) * mm});
            skLineSegment(sketch, "E4.5.0.55", {"start": v(125.21, -37.3) * mm, "end": v(125.21, -42.3) * mm});
            skLineSegment(sketch, "E4.5.0.56", {"start": v(64.01, -37.3) * mm, "end": v(69.01, -37.3) * mm});
            skLineSegment(sketch, "E4.5.0.57", {"start": v(64.01, -42.3) * mm, "end": v(69.01, -42.3) * mm});
            skLineSegment(sketch, "E4.5.0.58", {"start": v(164.21, -37.3) * mm, "end": v(164.21, -42.3) * mm});
            skLineSegment(sketch, "E4.5.0.59", {"start": v(186.41, -37.3) * mm, "end": v(186.41, -42.3) * mm});
            skLineSegment(sketch, "E4.5.0.60", {"start": v(9.61, -37.3) * mm, "end": v(9.61, -42.3) * mm});
            skLineSegment(sketch, "E4.5.0.61", {"start": v(84.41, -37.3) * mm, "end": v(89.41, -37.3) * mm});
            skLineSegment(sketch, "E4.5.0.62", {"start": v(9.61, -37.3) * mm, "end": v(14.61, -37.3) * mm});
            skLineSegment(sketch, "E4.5.0.63", {"start": v(50.41, -37.3) * mm, "end": v(55.41, -37.3) * mm});
            skLineSegment(sketch, "E4.5.0.64", {"start": v(109.81, -37.3) * mm, "end": v(109.81, -42.3) * mm});
            skLineSegment(sketch, "E4.5.0.65", {"start": v(91.21, -42.3) * mm, "end": v(96.21, -42.3) * mm});
            skLineSegment(sketch, "E4.5.0.66", {"start": v(103.01, -37.3) * mm, "end": v(103.01, -42.3) * mm});
            skLineSegment(sketch, "E4.5.0.67", {"start": v(2.81, -37.3) * mm, "end": v(7.81, -37.3) * mm});
            skLineSegment(sketch, "E4.5.0.68", {"start": v(98.01, -42.3) * mm, "end": v(103.01, -42.3) * mm});
            skLineSegment(sketch, "E4.5.0.69", {"start": v(123.41, -37.3) * mm, "end": v(123.41, -42.3) * mm});
            skLineSegment(sketch, "E4.5.0.70", {"start": v(84.41, -42.3) * mm, "end": v(89.41, -42.3) * mm});
            skLineSegment(sketch, "E4.5.0.71", {"start": v(16.41, -37.3) * mm, "end": v(21.41, -37.3) * mm});
            skLineSegment(sketch, "E4.5.0.72", {"start": v(30.01, -37.3) * mm, "end": v(35.01, -37.3) * mm});
            skLineSegment(sketch, "E4.5.0.73", {"start": v(77.61, -37.3) * mm, "end": v(77.61, -42.3) * mm});
            skLineSegment(sketch, "E4.5.0.74", {"start": v(2.81, -37.3) * mm, "end": v(2.81, -42.3) * mm});
            skLineSegment(sketch, "E4.5.0.75", {"start": v(30.01, -37.3) * mm, "end": v(30.01, -42.3) * mm});
            skLineSegment(sketch, "E4.5.0.76", {"start": v(159.21, -37.3) * mm, "end": v(159.21, -42.3) * mm});
            skLineSegment(sketch, "E4.5.0.77", {"start": v(104.81, -37.3) * mm, "end": v(109.81, -37.3) * mm});
            skLineSegment(sketch, "E4.5.0.78", {"start": v(82.61, -37.3) * mm, "end": v(82.61, -42.3) * mm});
            skLineSegment(sketch, "E4.5.0.79", {"start": v(35.01, -37.3) * mm, "end": v(35.01, -42.3) * mm});
            skLineSegment(sketch, "E4.5.0.80", {"start": v(157.41, -37.3) * mm, "end": v(157.41, -42.3) * mm});
            skLineSegment(sketch, "E4.5.0.81", {"start": v(21.41, -37.3) * mm, "end": v(21.41, -42.3) * mm});
            skLineSegment(sketch, "E4.5.0.82", {"start": v(143.81, -37.3) * mm, "end": v(143.81, -42.3) * mm});
            skLineSegment(sketch, "E4.5.0.83", {"start": v(138.81, -37.3) * mm, "end": v(138.81, -42.3) * mm});
            skLineSegment(sketch, "E4.5.0.84", {"start": v(130.21, -37.3) * mm, "end": v(130.21, -42.3) * mm});
            skLineSegment(sketch, "E4.5.0.85", {"start": v(57.21, -37.3) * mm, "end": v(57.21, -42.3) * mm});
            skLineSegment(sketch, "E4.5.0.86", {"start": v(137.01, -37.3) * mm, "end": v(137.01, -42.3) * mm});
            skLineSegment(sketch, "E4.5.0.87", {"start": v(118.41, -37.3) * mm, "end": v(118.41, -42.3) * mm});
            skLineSegment(sketch, "E4.5.0.88", {"start": v(96.21, -37.3) * mm, "end": v(96.21, -42.3) * mm});
            skLineSegment(sketch, "E4.5.0.89", {"start": v(145.61, -42.3) * mm, "end": v(150.61, -42.3) * mm});
            skLineSegment(sketch, "E4.5.0.90", {"start": v(166.01, -42.3) * mm, "end": v(171.01, -42.3) * mm});
            skLineSegment(sketch, "E4.5.0.91", {"start": v(50.41, -37.3) * mm, "end": v(50.41, -42.3) * mm});
            skLineSegment(sketch, "E4.5.0.92", {"start": v(118.41, -37.3) * mm, "end": v(123.41, -37.3) * mm});
            skLineSegment(sketch, "E4.5.0.93", {"start": v(132.01, -37.3) * mm, "end": v(132.01, -42.3) * mm});
            skLineSegment(sketch, "E4.5.0.94", {"start": v(16.41, -37.3) * mm, "end": v(16.41, -42.3) * mm});
            skLineSegment(sketch, "E4.5.0.95", {"start": v(104.81, -37.3) * mm, "end": v(104.81, -42.3) * mm});
            skLineSegment(sketch, "E4.5.0.96", {"start": v(111.61, -42.3) * mm, "end": v(116.61, -42.3) * mm});
            skLineSegment(sketch, "E4.5.0.97", {"start": v(89.41, -37.3) * mm, "end": v(89.41, -42.3) * mm});
            skLineSegment(sketch, "E4.5.0.98", {"start": v(152.41, -37.3) * mm, "end": v(157.41, -37.3) * mm});
            skLineSegment(sketch, "E4.5.0.99", {"start": v(186.41, -37.3) * mm, "end": v(191.41, -37.3) * mm});
            skLineSegment(sketch, "E4.5.0.100", {"start": v(36.81, -42.3) * mm, "end": v(41.81, -42.3) * mm});
            skLineSegment(sketch, "E4.5.0.101", {"start": v(43.61, -42.3) * mm, "end": v(48.61, -42.3) * mm});
            skLineSegment(sketch, "E4.5.0.102", {"start": v(2.81, -42.3) * mm, "end": v(9.61, -42.3) * mm, "construction": true});
            skLineSegment(sketch, "E4.5.0.103", {"start": v(159.21, -37.3) * mm, "end": v(164.21, -37.3) * mm});
            skLineSegment(sketch, "E4.5.0.104", {"start": v(166.01, -37.3) * mm, "end": v(171.01, -37.3) * mm});
            skLineSegment(sketch, "E4.5.0.105", {"start": v(172.81, -37.3) * mm, "end": v(177.81, -37.3) * mm});
            skLineSegment(sketch, "E4.5.0.106", {"start": v(16.41, -42.3) * mm, "end": v(21.41, -42.3) * mm});
            skLineSegment(sketch, "E4.5.0.107", {"start": v(30.01, -42.3) * mm, "end": v(35.01, -42.3) * mm});
            skLineSegment(sketch, "E4.5.0.108", {"start": v(23.21, -42.3) * mm, "end": v(28.21, -42.3) * mm});
            skLineSegment(sketch, "E4.5.0.109", {"start": v(9.61, -42.3) * mm, "end": v(14.61, -42.3) * mm});
            skLineSegment(sketch, "E4.5.0.110", {"start": v(50.41, -42.3) * mm, "end": v(55.41, -42.3) * mm});
            skLineSegment(sketch, "E4.5.0.111", {"start": v(179.61, -37.3) * mm, "end": v(184.61, -37.3) * mm});
            skLineSegment(sketch, "E4.5.0.112", {"start": v(2.81, -42.3) * mm, "end": v(7.81, -42.3) * mm});
            skLineSegment(sketch, "E4.6.0.0", {"start": v(111.66, -44.3) * mm, "end": v(116.66, -44.3) * mm});
            skLineSegment(sketch, "E4.6.0.1", {"start": v(116.66, -44.3) * mm, "end": v(116.66, -49.3) * mm});
            skLineSegment(sketch, "E4.6.0.2", {"start": v(125.26, -44.3) * mm, "end": v(130.26, -44.3) * mm});
            skLineSegment(sketch, "E4.6.0.3", {"start": v(28.26, -44.3) * mm, "end": v(28.26, -49.3) * mm});
            skLineSegment(sketch, "E4.6.0.4", {"start": v(70.86, -44.3) * mm, "end": v(75.86, -44.3) * mm});
            skLineSegment(sketch, "E4.6.0.5", {"start": v(172.86, -44.3) * mm, "end": v(172.86, -49.3) * mm});
            skLineSegment(sketch, "E4.6.0.6", {"start": v(48.66, -44.3) * mm, "end": v(48.66, -49.3) * mm});
            skLineSegment(sketch, "E4.6.0.7", {"start": v(84.46, -44.3) * mm, "end": v(84.46, -49.3) * mm});
            skLineSegment(sketch, "E4.6.0.8", {"start": v(14.66, -44.3) * mm, "end": v(14.66, -49.3) * mm});
            skLineSegment(sketch, "E4.6.0.9", {"start": v(98.06, -44.3) * mm, "end": v(103.06, -44.3) * mm});
            skLineSegment(sketch, "E4.6.0.10", {"start": v(166.06, -44.3) * mm, "end": v(166.06, -49.3) * mm});
            skLineSegment(sketch, "E4.6.0.11", {"start": v(91.26, -44.3) * mm, "end": v(96.26, -44.3) * mm});
            skLineSegment(sketch, "E4.6.0.12", {"start": v(70.86, -49.3) * mm, "end": v(75.86, -49.3) * mm});
            skLineSegment(sketch, "E4.6.0.13", {"start": v(132.06, -49.3) * mm, "end": v(137.06, -49.3) * mm});
            skLineSegment(sketch, "E4.6.0.14", {"start": v(145.66, -44.3) * mm, "end": v(145.66, -49.3) * mm});
            skLineSegment(sketch, "E4.6.0.15", {"start": v(104.86, -49.3) * mm, "end": v(109.86, -49.3) * mm});
            skLineSegment(sketch, "E4.6.0.16", {"start": v(191.46, -44.3) * mm, "end": v(191.46, -49.3) * mm});
            skLineSegment(sketch, "E4.6.0.17", {"start": v(159.26, -49.3) * mm, "end": v(164.26, -49.3) * mm});
            skLineSegment(sketch, "E4.6.0.18", {"start": v(75.86, -44.3) * mm, "end": v(75.86, -49.3) * mm});
            skLineSegment(sketch, "E4.6.0.19", {"start": v(23.26, -44.3) * mm, "end": v(23.26, -49.3) * mm});
            skLineSegment(sketch, "E4.6.0.20", {"start": v(145.66, -44.3) * mm, "end": v(150.66, -44.3) * mm});
            skLineSegment(sketch, "E4.6.0.21", {"start": v(138.86, -49.3) * mm, "end": v(143.86, -49.3) * mm});
            skLineSegment(sketch, "E4.6.0.22", {"start": v(184.66, -44.3) * mm, "end": v(184.66, -49.3) * mm});
            skLineSegment(sketch, "E4.6.0.23", {"start": v(55.46, -44.3) * mm, "end": v(55.46, -49.3) * mm});
            skLineSegment(sketch, "E4.6.0.24", {"start": v(171.06, -44.3) * mm, "end": v(171.06, -49.3) * mm});
            skLineSegment(sketch, "E4.6.0.25", {"start": v(62.26, -44.3) * mm, "end": v(62.26, -49.3) * mm});
            skLineSegment(sketch, "E4.6.0.26", {"start": v(69.06, -44.3) * mm, "end": v(69.06, -49.3) * mm});
            skLineSegment(sketch, "E4.6.0.27", {"start": v(132.06, -44.3) * mm, "end": v(137.06, -44.3) * mm});
            skLineSegment(sketch, "E4.6.0.28", {"start": v(64.06, -44.3) * mm, "end": v(64.06, -49.3) * mm});
            skLineSegment(sketch, "E4.6.0.29", {"start": v(152.46, -49.3) * mm, "end": v(157.46, -49.3) * mm});
            skLineSegment(sketch, "E4.6.0.30", {"start": v(179.66, -49.3) * mm, "end": v(184.66, -49.3) * mm});
            skLineSegment(sketch, "E4.6.0.31", {"start": v(36.86, -44.3) * mm, "end": v(36.86, -49.3) * mm});
            skLineSegment(sketch, "E4.6.0.32", {"start": v(172.86, -49.3) * mm, "end": v(177.86, -49.3) * mm});
            skLineSegment(sketch, "E4.6.0.33", {"start": v(91.26, -44.3) * mm, "end": v(91.26, -49.3) * mm});
            skLineSegment(sketch, "E4.6.0.34", {"start": v(77.66, -44.3) * mm, "end": v(82.66, -44.3) * mm});
            skLineSegment(sketch, "E4.6.0.35", {"start": v(70.86, -44.3) * mm, "end": v(70.86, -49.3) * mm});
            skLineSegment(sketch, "E4.6.0.36", {"start": v(57.26, -49.3) * mm, "end": v(62.26, -49.3) * mm});
            skLineSegment(sketch, "E4.6.0.37", {"start": v(111.66, -44.3) * mm, "end": v(111.66, -49.3) * mm});
            skLineSegment(sketch, "E4.6.0.38", {"start": v(150.66, -44.3) * mm, "end": v(150.66, -49.3) * mm});
            skLineSegment(sketch, "E4.6.0.39", {"start": v(177.86, -44.3) * mm, "end": v(177.86, -49.3) * mm});
            skLineSegment(sketch, "E4.6.0.40", {"start": v(179.66, -44.3) * mm, "end": v(179.66, -49.3) * mm});
            skLineSegment(sketch, "E4.6.0.41", {"start": v(98.06, -44.3) * mm, "end": v(98.06, -49.3) * mm});
            skLineSegment(sketch, "E4.6.0.42", {"start": v(36.86, -44.3) * mm, "end": v(41.86, -44.3) * mm});
            skLineSegment(sketch, "E4.6.0.43", {"start": v(118.46, -49.3) * mm, "end": v(123.46, -49.3) * mm});
            skLineSegment(sketch, "E4.6.0.44", {"start": v(7.86, -44.3) * mm, "end": v(7.86, -49.3) * mm});
            skLineSegment(sketch, "E4.6.0.45", {"start": v(43.66, -44.3) * mm, "end": v(43.66, -49.3) * mm});
            skLineSegment(sketch, "E4.6.0.46", {"start": v(77.66, -49.3) * mm, "end": v(82.66, -49.3) * mm});
            skLineSegment(sketch, "E4.6.0.47", {"start": v(138.86, -44.3) * mm, "end": v(143.86, -44.3) * mm});
            skLineSegment(sketch, "E4.6.0.48", {"start": v(23.26, -44.3) * mm, "end": v(28.26, -44.3) * mm});
            skLineSegment(sketch, "E4.6.0.49", {"start": v(152.46, -44.3) * mm, "end": v(152.46, -49.3) * mm});
            skLineSegment(sketch, "E4.6.0.50", {"start": v(57.26, -44.3) * mm, "end": v(62.26, -44.3) * mm});
            skLineSegment(sketch, "E4.6.0.51", {"start": v(43.66, -44.3) * mm, "end": v(48.66, -44.3) * mm});
            skLineSegment(sketch, "E4.6.0.52", {"start": v(41.86, -44.3) * mm, "end": v(41.86, -49.3) * mm});
            skLineSegment(sketch, "E4.6.0.53", {"start": v(125.26, -49.3) * mm, "end": v(130.26, -49.3) * mm});
            skLineSegment(sketch, "E4.6.0.54", {"start": v(186.46, -49.3) * mm, "end": v(191.46, -49.3) * mm});
            skLineSegment(sketch, "E4.6.0.55", {"start": v(125.26, -44.3) * mm, "end": v(125.26, -49.3) * mm});
            skLineSegment(sketch, "E4.6.0.56", {"start": v(64.06, -44.3) * mm, "end": v(69.06, -44.3) * mm});
            skLineSegment(sketch, "E4.6.0.57", {"start": v(64.06, -49.3) * mm, "end": v(69.06, -49.3) * mm});
            skLineSegment(sketch, "E4.6.0.58", {"start": v(164.26, -44.3) * mm, "end": v(164.26, -49.3) * mm});
            skLineSegment(sketch, "E4.6.0.59", {"start": v(186.46, -44.3) * mm, "end": v(186.46, -49.3) * mm});
            skLineSegment(sketch, "E4.6.0.60", {"start": v(9.66, -44.3) * mm, "end": v(9.66, -49.3) * mm});
            skLineSegment(sketch, "E4.6.0.61", {"start": v(84.46, -44.3) * mm, "end": v(89.46, -44.3) * mm});
            skLineSegment(sketch, "E4.6.0.62", {"start": v(9.66, -44.3) * mm, "end": v(14.66, -44.3) * mm});
            skLineSegment(sketch, "E4.6.0.63", {"start": v(50.46, -44.3) * mm, "end": v(55.46, -44.3) * mm});
            skLineSegment(sketch, "E4.6.0.64", {"start": v(109.86, -44.3) * mm, "end": v(109.86, -49.3) * mm});
            skLineSegment(sketch, "E4.6.0.65", {"start": v(91.26, -49.3) * mm, "end": v(96.26, -49.3) * mm});
            skLineSegment(sketch, "E4.6.0.66", {"start": v(103.06, -44.3) * mm, "end": v(103.06, -49.3) * mm});
            skLineSegment(sketch, "E4.6.0.67", {"start": v(2.86, -44.3) * mm, "end": v(7.86, -44.3) * mm});
            skLineSegment(sketch, "E4.6.0.68", {"start": v(98.06, -49.3) * mm, "end": v(103.06, -49.3) * mm});
            skLineSegment(sketch, "E4.6.0.69", {"start": v(123.46, -44.3) * mm, "end": v(123.46, -49.3) * mm});
            skLineSegment(sketch, "E4.6.0.70", {"start": v(84.46, -49.3) * mm, "end": v(89.46, -49.3) * mm});
            skLineSegment(sketch, "E4.6.0.71", {"start": v(16.46, -44.3) * mm, "end": v(21.46, -44.3) * mm});
            skLineSegment(sketch, "E4.6.0.72", {"start": v(30.06, -44.3) * mm, "end": v(35.06, -44.3) * mm});
            skLineSegment(sketch, "E4.6.0.73", {"start": v(77.66, -44.3) * mm, "end": v(77.66, -49.3) * mm});
            skLineSegment(sketch, "E4.6.0.74", {"start": v(2.86, -44.3) * mm, "end": v(2.86, -49.3) * mm});
            skLineSegment(sketch, "E4.6.0.75", {"start": v(30.06, -44.3) * mm, "end": v(30.06, -49.3) * mm});
            skLineSegment(sketch, "E4.6.0.76", {"start": v(159.26, -44.3) * mm, "end": v(159.26, -49.3) * mm});
            skLineSegment(sketch, "E4.6.0.77", {"start": v(104.86, -44.3) * mm, "end": v(109.86, -44.3) * mm});
            skLineSegment(sketch, "E4.6.0.78", {"start": v(82.66, -44.3) * mm, "end": v(82.66, -49.3) * mm});
            skLineSegment(sketch, "E4.6.0.79", {"start": v(35.06, -44.3) * mm, "end": v(35.06, -49.3) * mm});
            skLineSegment(sketch, "E4.6.0.80", {"start": v(157.46, -44.3) * mm, "end": v(157.46, -49.3) * mm});
            skLineSegment(sketch, "E4.6.0.81", {"start": v(21.46, -44.3) * mm, "end": v(21.46, -49.3) * mm});
            skLineSegment(sketch, "E4.6.0.82", {"start": v(143.86, -44.3) * mm, "end": v(143.86, -49.3) * mm});
            skLineSegment(sketch, "E4.6.0.83", {"start": v(138.86, -44.3) * mm, "end": v(138.86, -49.3) * mm});
            skLineSegment(sketch, "E4.6.0.84", {"start": v(130.26, -44.3) * mm, "end": v(130.26, -49.3) * mm});
            skLineSegment(sketch, "E4.6.0.85", {"start": v(57.26, -44.3) * mm, "end": v(57.26, -49.3) * mm});
            skLineSegment(sketch, "E4.6.0.86", {"start": v(137.06, -44.3) * mm, "end": v(137.06, -49.3) * mm});
            skLineSegment(sketch, "E4.6.0.87", {"start": v(118.46, -44.3) * mm, "end": v(118.46, -49.3) * mm});
            skLineSegment(sketch, "E4.6.0.88", {"start": v(96.26, -44.3) * mm, "end": v(96.26, -49.3) * mm});
            skLineSegment(sketch, "E4.6.0.89", {"start": v(145.66, -49.3) * mm, "end": v(150.66, -49.3) * mm});
            skLineSegment(sketch, "E4.6.0.90", {"start": v(166.06, -49.3) * mm, "end": v(171.06, -49.3) * mm});
            skLineSegment(sketch, "E4.6.0.91", {"start": v(50.46, -44.3) * mm, "end": v(50.46, -49.3) * mm});
            skLineSegment(sketch, "E4.6.0.92", {"start": v(118.46, -44.3) * mm, "end": v(123.46, -44.3) * mm});
            skLineSegment(sketch, "E4.6.0.93", {"start": v(132.06, -44.3) * mm, "end": v(132.06, -49.3) * mm});
            skLineSegment(sketch, "E4.6.0.94", {"start": v(16.46, -44.3) * mm, "end": v(16.46, -49.3) * mm});
            skLineSegment(sketch, "E4.6.0.95", {"start": v(104.86, -44.3) * mm, "end": v(104.86, -49.3) * mm});
            skLineSegment(sketch, "E4.6.0.96", {"start": v(111.66, -49.3) * mm, "end": v(116.66, -49.3) * mm});
            skLineSegment(sketch, "E4.6.0.97", {"start": v(89.46, -44.3) * mm, "end": v(89.46, -49.3) * mm});
            skLineSegment(sketch, "E4.6.0.98", {"start": v(152.46, -44.3) * mm, "end": v(157.46, -44.3) * mm});
            skLineSegment(sketch, "E4.6.0.99", {"start": v(186.46, -44.3) * mm, "end": v(191.46, -44.3) * mm});
            skLineSegment(sketch, "E4.6.0.100", {"start": v(36.86, -49.3) * mm, "end": v(41.86, -49.3) * mm});
            skLineSegment(sketch, "E4.6.0.101", {"start": v(43.66, -49.3) * mm, "end": v(48.66, -49.3) * mm});
            skLineSegment(sketch, "E4.6.0.102", {"start": v(2.86, -49.3) * mm, "end": v(9.66, -49.3) * mm, "construction": true});
            skLineSegment(sketch, "E4.6.0.103", {"start": v(159.26, -44.3) * mm, "end": v(164.26, -44.3) * mm});
            skLineSegment(sketch, "E4.6.0.104", {"start": v(166.06, -44.3) * mm, "end": v(171.06, -44.3) * mm});
            skLineSegment(sketch, "E4.6.0.105", {"start": v(172.86, -44.3) * mm, "end": v(177.86, -44.3) * mm});
            skLineSegment(sketch, "E4.6.0.106", {"start": v(16.46, -49.3) * mm, "end": v(21.46, -49.3) * mm});
            skLineSegment(sketch, "E4.6.0.107", {"start": v(30.06, -49.3) * mm, "end": v(35.06, -49.3) * mm});
            skLineSegment(sketch, "E4.6.0.108", {"start": v(23.26, -49.3) * mm, "end": v(28.26, -49.3) * mm});
            skLineSegment(sketch, "E4.6.0.109", {"start": v(9.66, -49.3) * mm, "end": v(14.66, -49.3) * mm});
            skLineSegment(sketch, "E4.6.0.110", {"start": v(50.46, -49.3) * mm, "end": v(55.46, -49.3) * mm});
            skLineSegment(sketch, "E4.6.0.111", {"start": v(179.66, -44.3) * mm, "end": v(184.66, -44.3) * mm});
            skLineSegment(sketch, "E4.6.0.112", {"start": v(2.86, -49.3) * mm, "end": v(7.86, -49.3) * mm});
            skLineSegment(sketch, "E4.7.0.0", {"start": v(111.7, -51.3) * mm, "end": v(116.7, -51.3) * mm});
            skLineSegment(sketch, "E4.7.0.1", {"start": v(116.7, -51.3) * mm, "end": v(116.7, -56.3) * mm});
            skLineSegment(sketch, "E4.7.0.2", {"start": v(125.3, -51.3) * mm, "end": v(130.3, -51.3) * mm});
            skLineSegment(sketch, "E4.7.0.3", {"start": v(28.3, -51.3) * mm, "end": v(28.3, -56.3) * mm});
            skLineSegment(sketch, "E4.7.0.4", {"start": v(70.9, -51.3) * mm, "end": v(75.9, -51.3) * mm});
            skLineSegment(sketch, "E4.7.0.5", {"start": v(172.9, -51.3) * mm, "end": v(172.9, -56.3) * mm});
            skLineSegment(sketch, "E4.7.0.6", {"start": v(48.7, -51.3) * mm, "end": v(48.7, -56.3) * mm});
            skLineSegment(sketch, "E4.7.0.7", {"start": v(84.5, -51.3) * mm, "end": v(84.5, -56.3) * mm});
            skLineSegment(sketch, "E4.7.0.8", {"start": v(14.7, -51.3) * mm, "end": v(14.7, -56.3) * mm});
            skLineSegment(sketch, "E4.7.0.9", {"start": v(98.1, -51.3) * mm, "end": v(103.1, -51.3) * mm});
            skLineSegment(sketch, "E4.7.0.10", {"start": v(166.1, -51.3) * mm, "end": v(166.1, -56.3) * mm});
            skLineSegment(sketch, "E4.7.0.11", {"start": v(91.3, -51.3) * mm, "end": v(96.3, -51.3) * mm});
            skLineSegment(sketch, "E4.7.0.12", {"start": v(70.9, -56.3) * mm, "end": v(75.9, -56.3) * mm});
            skLineSegment(sketch, "E4.7.0.13", {"start": v(132.1, -56.3) * mm, "end": v(137.1, -56.3) * mm});
            skLineSegment(sketch, "E4.7.0.14", {"start": v(145.7, -51.3) * mm, "end": v(145.7, -56.3) * mm});
            skLineSegment(sketch, "E4.7.0.15", {"start": v(104.9, -56.3) * mm, "end": v(109.9, -56.3) * mm});
            skLineSegment(sketch, "E4.7.0.16", {"start": v(191.5, -51.3) * mm, "end": v(191.5, -56.3) * mm});
            skLineSegment(sketch, "E4.7.0.17", {"start": v(159.3, -56.3) * mm, "end": v(164.3, -56.3) * mm});
            skLineSegment(sketch, "E4.7.0.18", {"start": v(75.9, -51.3) * mm, "end": v(75.9, -56.3) * mm});
            skLineSegment(sketch, "E4.7.0.19", {"start": v(23.3, -51.3) * mm, "end": v(23.3, -56.3) * mm});
            skLineSegment(sketch, "E4.7.0.20", {"start": v(145.7, -51.3) * mm, "end": v(150.7, -51.3) * mm});
            skLineSegment(sketch, "E4.7.0.21", {"start": v(138.9, -56.3) * mm, "end": v(143.9, -56.3) * mm});
            skLineSegment(sketch, "E4.7.0.22", {"start": v(184.7, -51.3) * mm, "end": v(184.7, -56.3) * mm});
            skLineSegment(sketch, "E4.7.0.23", {"start": v(55.5, -51.3) * mm, "end": v(55.5, -56.3) * mm});
            skLineSegment(sketch, "E4.7.0.24", {"start": v(171.1, -51.3) * mm, "end": v(171.1, -56.3) * mm});
            skLineSegment(sketch, "E4.7.0.25", {"start": v(62.3, -51.3) * mm, "end": v(62.3, -56.3) * mm});
            skLineSegment(sketch, "E4.7.0.26", {"start": v(69.1, -51.3) * mm, "end": v(69.1, -56.3) * mm});
            skLineSegment(sketch, "E4.7.0.27", {"start": v(132.1, -51.3) * mm, "end": v(137.1, -51.3) * mm});
            skLineSegment(sketch, "E4.7.0.28", {"start": v(64.1, -51.3) * mm, "end": v(64.1, -56.3) * mm});
            skLineSegment(sketch, "E4.7.0.29", {"start": v(152.5, -56.3) * mm, "end": v(157.5, -56.3) * mm});
            skLineSegment(sketch, "E4.7.0.30", {"start": v(179.7, -56.3) * mm, "end": v(184.7, -56.3) * mm});
            skLineSegment(sketch, "E4.7.0.31", {"start": v(36.9, -51.3) * mm, "end": v(36.9, -56.3) * mm});
            skLineSegment(sketch, "E4.7.0.32", {"start": v(172.9, -56.3) * mm, "end": v(177.9, -56.3) * mm});
            skLineSegment(sketch, "E4.7.0.33", {"start": v(91.3, -51.3) * mm, "end": v(91.3, -56.3) * mm});
            skLineSegment(sketch, "E4.7.0.34", {"start": v(77.7, -51.3) * mm, "end": v(82.7, -51.3) * mm});
            skLineSegment(sketch, "E4.7.0.35", {"start": v(70.9, -51.3) * mm, "end": v(70.9, -56.3) * mm});
            skLineSegment(sketch, "E4.7.0.36", {"start": v(57.3, -56.3) * mm, "end": v(62.3, -56.3) * mm});
            skLineSegment(sketch, "E4.7.0.37", {"start": v(111.7, -51.3) * mm, "end": v(111.7, -56.3) * mm});
            skLineSegment(sketch, "E4.7.0.38", {"start": v(150.7, -51.3) * mm, "end": v(150.7, -56.3) * mm});
            skLineSegment(sketch, "E4.7.0.39", {"start": v(177.9, -51.3) * mm, "end": v(177.9, -56.3) * mm});
            skLineSegment(sketch, "E4.7.0.40", {"start": v(179.7, -51.3) * mm, "end": v(179.7, -56.3) * mm});
            skLineSegment(sketch, "E4.7.0.41", {"start": v(98.1, -51.3) * mm, "end": v(98.1, -56.3) * mm});
            skLineSegment(sketch, "E4.7.0.42", {"start": v(36.9, -51.3) * mm, "end": v(41.9, -51.3) * mm});
            skLineSegment(sketch, "E4.7.0.43", {"start": v(118.5, -56.3) * mm, "end": v(123.5, -56.3) * mm});
            skLineSegment(sketch, "E4.7.0.44", {"start": v(7.9, -51.3) * mm, "end": v(7.9, -56.3) * mm});
            skLineSegment(sketch, "E4.7.0.45", {"start": v(43.7, -51.3) * mm, "end": v(43.7, -56.3) * mm});
            skLineSegment(sketch, "E4.7.0.46", {"start": v(77.7, -56.3) * mm, "end": v(82.7, -56.3) * mm});
            skLineSegment(sketch, "E4.7.0.47", {"start": v(138.9, -51.3) * mm, "end": v(143.9, -51.3) * mm});
            skLineSegment(sketch, "E4.7.0.48", {"start": v(23.3, -51.3) * mm, "end": v(28.3, -51.3) * mm});
            skLineSegment(sketch, "E4.7.0.49", {"start": v(152.5, -51.3) * mm, "end": v(152.5, -56.3) * mm});
            skLineSegment(sketch, "E4.7.0.50", {"start": v(57.3, -51.3) * mm, "end": v(62.3, -51.3) * mm});
            skLineSegment(sketch, "E4.7.0.51", {"start": v(43.7, -51.3) * mm, "end": v(48.7, -51.3) * mm});
            skLineSegment(sketch, "E4.7.0.52", {"start": v(41.9, -51.3) * mm, "end": v(41.9, -56.3) * mm});
            skLineSegment(sketch, "E4.7.0.53", {"start": v(125.3, -56.3) * mm, "end": v(130.3, -56.3) * mm});
            skLineSegment(sketch, "E4.7.0.54", {"start": v(186.5, -56.3) * mm, "end": v(191.5, -56.3) * mm});
            skLineSegment(sketch, "E4.7.0.55", {"start": v(125.3, -51.3) * mm, "end": v(125.3, -56.3) * mm});
            skLineSegment(sketch, "E4.7.0.56", {"start": v(64.1, -51.3) * mm, "end": v(69.1, -51.3) * mm});
            skLineSegment(sketch, "E4.7.0.57", {"start": v(64.1, -56.3) * mm, "end": v(69.1, -56.3) * mm});
            skLineSegment(sketch, "E4.7.0.58", {"start": v(164.3, -51.3) * mm, "end": v(164.3, -56.3) * mm});
            skLineSegment(sketch, "E4.7.0.59", {"start": v(186.5, -51.3) * mm, "end": v(186.5, -56.3) * mm});
            skLineSegment(sketch, "E4.7.0.60", {"start": v(9.7, -51.3) * mm, "end": v(9.7, -56.3) * mm});
            skLineSegment(sketch, "E4.7.0.61", {"start": v(84.5, -51.3) * mm, "end": v(89.5, -51.3) * mm});
            skLineSegment(sketch, "E4.7.0.62", {"start": v(9.7, -51.3) * mm, "end": v(14.7, -51.3) * mm});
            skLineSegment(sketch, "E4.7.0.63", {"start": v(50.5, -51.3) * mm, "end": v(55.5, -51.3) * mm});
            skLineSegment(sketch, "E4.7.0.64", {"start": v(109.9, -51.3) * mm, "end": v(109.9, -56.3) * mm});
            skLineSegment(sketch, "E4.7.0.65", {"start": v(91.3, -56.3) * mm, "end": v(96.3, -56.3) * mm});
            skLineSegment(sketch, "E4.7.0.66", {"start": v(103.1, -51.3) * mm, "end": v(103.1, -56.3) * mm});
            skLineSegment(sketch, "E4.7.0.67", {"start": v(2.9, -51.3) * mm, "end": v(7.9, -51.3) * mm});
            skLineSegment(sketch, "E4.7.0.68", {"start": v(98.1, -56.3) * mm, "end": v(103.1, -56.3) * mm});
            skLineSegment(sketch, "E4.7.0.69", {"start": v(123.5, -51.3) * mm, "end": v(123.5, -56.3) * mm});
            skLineSegment(sketch, "E4.7.0.70", {"start": v(84.5, -56.3) * mm, "end": v(89.5, -56.3) * mm});
            skLineSegment(sketch, "E4.7.0.71", {"start": v(16.5, -51.3) * mm, "end": v(21.5, -51.3) * mm});
            skLineSegment(sketch, "E4.7.0.72", {"start": v(30.1, -51.3) * mm, "end": v(35.1, -51.3) * mm});
            skLineSegment(sketch, "E4.7.0.73", {"start": v(77.7, -51.3) * mm, "end": v(77.7, -56.3) * mm});
            skLineSegment(sketch, "E4.7.0.74", {"start": v(2.9, -51.3) * mm, "end": v(2.9, -56.3) * mm});
            skLineSegment(sketch, "E4.7.0.75", {"start": v(30.1, -51.3) * mm, "end": v(30.1, -56.3) * mm});
            skLineSegment(sketch, "E4.7.0.76", {"start": v(159.3, -51.3) * mm, "end": v(159.3, -56.3) * mm});
            skLineSegment(sketch, "E4.7.0.77", {"start": v(104.9, -51.3) * mm, "end": v(109.9, -51.3) * mm});
            skLineSegment(sketch, "E4.7.0.78", {"start": v(82.7, -51.3) * mm, "end": v(82.7, -56.3) * mm});
            skLineSegment(sketch, "E4.7.0.79", {"start": v(35.1, -51.3) * mm, "end": v(35.1, -56.3) * mm});
            skLineSegment(sketch, "E4.7.0.80", {"start": v(157.5, -51.3) * mm, "end": v(157.5, -56.3) * mm});
            skLineSegment(sketch, "E4.7.0.81", {"start": v(21.5, -51.3) * mm, "end": v(21.5, -56.3) * mm});
            skLineSegment(sketch, "E4.7.0.82", {"start": v(143.9, -51.3) * mm, "end": v(143.9, -56.3) * mm});
            skLineSegment(sketch, "E4.7.0.83", {"start": v(138.9, -51.3) * mm, "end": v(138.9, -56.3) * mm});
            skLineSegment(sketch, "E4.7.0.84", {"start": v(130.3, -51.3) * mm, "end": v(130.3, -56.3) * mm});
            skLineSegment(sketch, "E4.7.0.85", {"start": v(57.3, -51.3) * mm, "end": v(57.3, -56.3) * mm});
            skLineSegment(sketch, "E4.7.0.86", {"start": v(137.1, -51.3) * mm, "end": v(137.1, -56.3) * mm});
            skLineSegment(sketch, "E4.7.0.87", {"start": v(118.5, -51.3) * mm, "end": v(118.5, -56.3) * mm});
            skLineSegment(sketch, "E4.7.0.88", {"start": v(96.3, -51.3) * mm, "end": v(96.3, -56.3) * mm});
            skLineSegment(sketch, "E4.7.0.89", {"start": v(145.7, -56.3) * mm, "end": v(150.7, -56.3) * mm});
            skLineSegment(sketch, "E4.7.0.90", {"start": v(166.1, -56.3) * mm, "end": v(171.1, -56.3) * mm});
            skLineSegment(sketch, "E4.7.0.91", {"start": v(50.5, -51.3) * mm, "end": v(50.5, -56.3) * mm});
            skLineSegment(sketch, "E4.7.0.92", {"start": v(118.5, -51.3) * mm, "end": v(123.5, -51.3) * mm});
            skLineSegment(sketch, "E4.7.0.93", {"start": v(132.1, -51.3) * mm, "end": v(132.1, -56.3) * mm});
            skLineSegment(sketch, "E4.7.0.94", {"start": v(16.5, -51.3) * mm, "end": v(16.5, -56.3) * mm});
            skLineSegment(sketch, "E4.7.0.95", {"start": v(104.9, -51.3) * mm, "end": v(104.9, -56.3) * mm});
            skLineSegment(sketch, "E4.7.0.96", {"start": v(111.7, -56.3) * mm, "end": v(116.7, -56.3) * mm});
            skLineSegment(sketch, "E4.7.0.97", {"start": v(89.5, -51.3) * mm, "end": v(89.5, -56.3) * mm});
            skLineSegment(sketch, "E4.7.0.98", {"start": v(152.5, -51.3) * mm, "end": v(157.5, -51.3) * mm});
            skLineSegment(sketch, "E4.7.0.99", {"start": v(186.5, -51.3) * mm, "end": v(191.5, -51.3) * mm});
            skLineSegment(sketch, "E4.7.0.100", {"start": v(36.9, -56.3) * mm, "end": v(41.9, -56.3) * mm});
            skLineSegment(sketch, "E4.7.0.101", {"start": v(43.7, -56.3) * mm, "end": v(48.7, -56.3) * mm});
            skLineSegment(sketch, "E4.7.0.102", {"start": v(2.9, -56.3) * mm, "end": v(9.7, -56.3) * mm, "construction": true});
            skLineSegment(sketch, "E4.7.0.103", {"start": v(159.3, -51.3) * mm, "end": v(164.3, -51.3) * mm});
            skLineSegment(sketch, "E4.7.0.104", {"start": v(166.1, -51.3) * mm, "end": v(171.1, -51.3) * mm});
            skLineSegment(sketch, "E4.7.0.105", {"start": v(172.9, -51.3) * mm, "end": v(177.9, -51.3) * mm});
            skLineSegment(sketch, "E4.7.0.106", {"start": v(16.5, -56.3) * mm, "end": v(21.5, -56.3) * mm});
            skLineSegment(sketch, "E4.7.0.107", {"start": v(30.1, -56.3) * mm, "end": v(35.1, -56.3) * mm});
            skLineSegment(sketch, "E4.7.0.108", {"start": v(23.3, -56.3) * mm, "end": v(28.3, -56.3) * mm});
            skLineSegment(sketch, "E4.7.0.109", {"start": v(9.7, -56.3) * mm, "end": v(14.7, -56.3) * mm});
            skLineSegment(sketch, "E4.7.0.110", {"start": v(50.5, -56.3) * mm, "end": v(55.5, -56.3) * mm});
            skLineSegment(sketch, "E4.7.0.111", {"start": v(179.7, -51.3) * mm, "end": v(184.7, -51.3) * mm});
            skLineSegment(sketch, "E4.7.0.112", {"start": v(2.9, -56.3) * mm, "end": v(7.9, -56.3) * mm});
            skLineSegment(sketch, "E4.8.0.0", {"start": v(111.75, -58.3) * mm, "end": v(116.75, -58.3) * mm});
            skLineSegment(sketch, "E4.8.0.1", {"start": v(116.75, -58.3) * mm, "end": v(116.75, -63.3) * mm});
            skLineSegment(sketch, "E4.8.0.2", {"start": v(125.35, -58.3) * mm, "end": v(130.35, -58.3) * mm});
            skLineSegment(sketch, "E4.8.0.3", {"start": v(28.35, -58.3) * mm, "end": v(28.35, -63.3) * mm});
            skLineSegment(sketch, "E4.8.0.4", {"start": v(70.95, -58.3) * mm, "end": v(75.95, -58.3) * mm});
            skLineSegment(sketch, "E4.8.0.5", {"start": v(172.95, -58.3) * mm, "end": v(172.95, -63.3) * mm});
            skLineSegment(sketch, "E4.8.0.6", {"start": v(48.75, -58.3) * mm, "end": v(48.75, -63.3) * mm});
            skLineSegment(sketch, "E4.8.0.7", {"start": v(84.55, -58.3) * mm, "end": v(84.55, -63.3) * mm});
            skLineSegment(sketch, "E4.8.0.8", {"start": v(14.75, -58.3) * mm, "end": v(14.75, -63.3) * mm});
            skLineSegment(sketch, "E4.8.0.9", {"start": v(98.15, -58.3) * mm, "end": v(103.15, -58.3) * mm});
            skLineSegment(sketch, "E4.8.0.10", {"start": v(166.15, -58.3) * mm, "end": v(166.15, -63.3) * mm});
            skLineSegment(sketch, "E4.8.0.11", {"start": v(91.35, -58.3) * mm, "end": v(96.35, -58.3) * mm});
            skLineSegment(sketch, "E4.8.0.12", {"start": v(70.95, -63.3) * mm, "end": v(75.95, -63.3) * mm});
            skLineSegment(sketch, "E4.8.0.13", {"start": v(132.15, -63.3) * mm, "end": v(137.15, -63.3) * mm});
            skLineSegment(sketch, "E4.8.0.14", {"start": v(145.75, -58.3) * mm, "end": v(145.75, -63.3) * mm});
            skLineSegment(sketch, "E4.8.0.15", {"start": v(104.95, -63.3) * mm, "end": v(109.95, -63.3) * mm});
            skLineSegment(sketch, "E4.8.0.16", {"start": v(191.55, -58.3) * mm, "end": v(191.55, -63.3) * mm});
            skLineSegment(sketch, "E4.8.0.17", {"start": v(159.35, -63.3) * mm, "end": v(164.35, -63.3) * mm});
            skLineSegment(sketch, "E4.8.0.18", {"start": v(75.95, -58.3) * mm, "end": v(75.95, -63.3) * mm});
            skLineSegment(sketch, "E4.8.0.19", {"start": v(23.35, -58.3) * mm, "end": v(23.35, -63.3) * mm});
            skLineSegment(sketch, "E4.8.0.20", {"start": v(145.75, -58.3) * mm, "end": v(150.75, -58.3) * mm});
            skLineSegment(sketch, "E4.8.0.21", {"start": v(138.95, -63.3) * mm, "end": v(143.95, -63.3) * mm});
            skLineSegment(sketch, "E4.8.0.22", {"start": v(184.75, -58.3) * mm, "end": v(184.75, -63.3) * mm});
            skLineSegment(sketch, "E4.8.0.23", {"start": v(55.55, -58.3) * mm, "end": v(55.55, -63.3) * mm});
            skLineSegment(sketch, "E4.8.0.24", {"start": v(171.15, -58.3) * mm, "end": v(171.15, -63.3) * mm});
            skLineSegment(sketch, "E4.8.0.25", {"start": v(62.35, -58.3) * mm, "end": v(62.35, -63.3) * mm});
            skLineSegment(sketch, "E4.8.0.26", {"start": v(69.15, -58.3) * mm, "end": v(69.15, -63.3) * mm});
            skLineSegment(sketch, "E4.8.0.27", {"start": v(132.15, -58.3) * mm, "end": v(137.15, -58.3) * mm});
            skLineSegment(sketch, "E4.8.0.28", {"start": v(64.15, -58.3) * mm, "end": v(64.15, -63.3) * mm});
            skLineSegment(sketch, "E4.8.0.29", {"start": v(152.55, -63.3) * mm, "end": v(157.55, -63.3) * mm});
            skLineSegment(sketch, "E4.8.0.30", {"start": v(179.75, -63.3) * mm, "end": v(184.75, -63.3) * mm});
            skLineSegment(sketch, "E4.8.0.31", {"start": v(36.95, -58.3) * mm, "end": v(36.95, -63.3) * mm});
            skLineSegment(sketch, "E4.8.0.32", {"start": v(172.95, -63.3) * mm, "end": v(177.95, -63.3) * mm});
            skLineSegment(sketch, "E4.8.0.33", {"start": v(91.35, -58.3) * mm, "end": v(91.35, -63.3) * mm});
            skLineSegment(sketch, "E4.8.0.34", {"start": v(77.75, -58.3) * mm, "end": v(82.75, -58.3) * mm});
            skLineSegment(sketch, "E4.8.0.35", {"start": v(70.95, -58.3) * mm, "end": v(70.95, -63.3) * mm});
            skLineSegment(sketch, "E4.8.0.36", {"start": v(57.35, -63.3) * mm, "end": v(62.35, -63.3) * mm});
            skLineSegment(sketch, "E4.8.0.37", {"start": v(111.75, -58.3) * mm, "end": v(111.75, -63.3) * mm});
            skLineSegment(sketch, "E4.8.0.38", {"start": v(150.75, -58.3) * mm, "end": v(150.75, -63.3) * mm});
            skLineSegment(sketch, "E4.8.0.39", {"start": v(177.95, -58.3) * mm, "end": v(177.95, -63.3) * mm});
            skLineSegment(sketch, "E4.8.0.40", {"start": v(179.75, -58.3) * mm, "end": v(179.75, -63.3) * mm});
            skLineSegment(sketch, "E4.8.0.41", {"start": v(98.15, -58.3) * mm, "end": v(98.15, -63.3) * mm});
            skLineSegment(sketch, "E4.8.0.42", {"start": v(36.95, -58.3) * mm, "end": v(41.95, -58.3) * mm});
            skLineSegment(sketch, "E4.8.0.43", {"start": v(118.55, -63.3) * mm, "end": v(123.55, -63.3) * mm});
            skLineSegment(sketch, "E4.8.0.44", {"start": v(7.95, -58.3) * mm, "end": v(7.95, -63.3) * mm});
            skLineSegment(sketch, "E4.8.0.45", {"start": v(43.75, -58.3) * mm, "end": v(43.75, -63.3) * mm});
            skLineSegment(sketch, "E4.8.0.46", {"start": v(77.75, -63.3) * mm, "end": v(82.75, -63.3) * mm});
            skLineSegment(sketch, "E4.8.0.47", {"start": v(138.95, -58.3) * mm, "end": v(143.95, -58.3) * mm});
            skLineSegment(sketch, "E4.8.0.48", {"start": v(23.35, -58.3) * mm, "end": v(28.35, -58.3) * mm});
            skLineSegment(sketch, "E4.8.0.49", {"start": v(152.55, -58.3) * mm, "end": v(152.55, -63.3) * mm});
            skLineSegment(sketch, "E4.8.0.50", {"start": v(57.35, -58.3) * mm, "end": v(62.35, -58.3) * mm});
            skLineSegment(sketch, "E4.8.0.51", {"start": v(43.75, -58.3) * mm, "end": v(48.75, -58.3) * mm});
            skLineSegment(sketch, "E4.8.0.52", {"start": v(41.95, -58.3) * mm, "end": v(41.95, -63.3) * mm});
            skLineSegment(sketch, "E4.8.0.53", {"start": v(125.35, -63.3) * mm, "end": v(130.35, -63.3) * mm});
            skLineSegment(sketch, "E4.8.0.54", {"start": v(186.55, -63.3) * mm, "end": v(191.55, -63.3) * mm});
            skLineSegment(sketch, "E4.8.0.55", {"start": v(125.35, -58.3) * mm, "end": v(125.35, -63.3) * mm});
            skLineSegment(sketch, "E4.8.0.56", {"start": v(64.15, -58.3) * mm, "end": v(69.15, -58.3) * mm});
            skLineSegment(sketch, "E4.8.0.57", {"start": v(64.15, -63.3) * mm, "end": v(69.15, -63.3) * mm});
            skLineSegment(sketch, "E4.8.0.58", {"start": v(164.35, -58.3) * mm, "end": v(164.35, -63.3) * mm});
            skLineSegment(sketch, "E4.8.0.59", {"start": v(186.55, -58.3) * mm, "end": v(186.55, -63.3) * mm});
            skLineSegment(sketch, "E4.8.0.60", {"start": v(9.75, -58.3) * mm, "end": v(9.75, -63.3) * mm});
            skLineSegment(sketch, "E4.8.0.61", {"start": v(84.55, -58.3) * mm, "end": v(89.55, -58.3) * mm});
            skLineSegment(sketch, "E4.8.0.62", {"start": v(9.75, -58.3) * mm, "end": v(14.75, -58.3) * mm});
            skLineSegment(sketch, "E4.8.0.63", {"start": v(50.55, -58.3) * mm, "end": v(55.55, -58.3) * mm});
            skLineSegment(sketch, "E4.8.0.64", {"start": v(109.95, -58.3) * mm, "end": v(109.95, -63.3) * mm});
            skLineSegment(sketch, "E4.8.0.65", {"start": v(91.35, -63.3) * mm, "end": v(96.35, -63.3) * mm});
            skLineSegment(sketch, "E4.8.0.66", {"start": v(103.15, -58.3) * mm, "end": v(103.15, -63.3) * mm});
            skLineSegment(sketch, "E4.8.0.67", {"start": v(2.95, -58.3) * mm, "end": v(7.95, -58.3) * mm});
            skLineSegment(sketch, "E4.8.0.68", {"start": v(98.15, -63.3) * mm, "end": v(103.15, -63.3) * mm});
            skLineSegment(sketch, "E4.8.0.69", {"start": v(123.55, -58.3) * mm, "end": v(123.55, -63.3) * mm});
            skLineSegment(sketch, "E4.8.0.70", {"start": v(84.55, -63.3) * mm, "end": v(89.55, -63.3) * mm});
            skLineSegment(sketch, "E4.8.0.71", {"start": v(16.55, -58.3) * mm, "end": v(21.55, -58.3) * mm});
            skLineSegment(sketch, "E4.8.0.72", {"start": v(30.15, -58.3) * mm, "end": v(35.15, -58.3) * mm});
            skLineSegment(sketch, "E4.8.0.73", {"start": v(77.75, -58.3) * mm, "end": v(77.75, -63.3) * mm});
            skLineSegment(sketch, "E4.8.0.74", {"start": v(2.95, -58.3) * mm, "end": v(2.95, -63.3) * mm});
            skLineSegment(sketch, "E4.8.0.75", {"start": v(30.15, -58.3) * mm, "end": v(30.15, -63.3) * mm});
            skLineSegment(sketch, "E4.8.0.76", {"start": v(159.35, -58.3) * mm, "end": v(159.35, -63.3) * mm});
            skLineSegment(sketch, "E4.8.0.77", {"start": v(104.95, -58.3) * mm, "end": v(109.95, -58.3) * mm});
            skLineSegment(sketch, "E4.8.0.78", {"start": v(82.75, -58.3) * mm, "end": v(82.75, -63.3) * mm});
            skLineSegment(sketch, "E4.8.0.79", {"start": v(35.15, -58.3) * mm, "end": v(35.15, -63.3) * mm});
            skLineSegment(sketch, "E4.8.0.80", {"start": v(157.55, -58.3) * mm, "end": v(157.55, -63.3) * mm});
            skLineSegment(sketch, "E4.8.0.81", {"start": v(21.55, -58.3) * mm, "end": v(21.55, -63.3) * mm});
            skLineSegment(sketch, "E4.8.0.82", {"start": v(143.95, -58.3) * mm, "end": v(143.95, -63.3) * mm});
            skLineSegment(sketch, "E4.8.0.83", {"start": v(138.95, -58.3) * mm, "end": v(138.95, -63.3) * mm});
            skLineSegment(sketch, "E4.8.0.84", {"start": v(130.35, -58.3) * mm, "end": v(130.35, -63.3) * mm});
            skLineSegment(sketch, "E4.8.0.85", {"start": v(57.35, -58.3) * mm, "end": v(57.35, -63.3) * mm});
            skLineSegment(sketch, "E4.8.0.86", {"start": v(137.15, -58.3) * mm, "end": v(137.15, -63.3) * mm});
            skLineSegment(sketch, "E4.8.0.87", {"start": v(118.55, -58.3) * mm, "end": v(118.55, -63.3) * mm});
            skLineSegment(sketch, "E4.8.0.88", {"start": v(96.35, -58.3) * mm, "end": v(96.35, -63.3) * mm});
            skLineSegment(sketch, "E4.8.0.89", {"start": v(145.75, -63.3) * mm, "end": v(150.75, -63.3) * mm});
            skLineSegment(sketch, "E4.8.0.90", {"start": v(166.15, -63.3) * mm, "end": v(171.15, -63.3) * mm});
            skLineSegment(sketch, "E4.8.0.91", {"start": v(50.55, -58.3) * mm, "end": v(50.55, -63.3) * mm});
            skLineSegment(sketch, "E4.8.0.92", {"start": v(118.55, -58.3) * mm, "end": v(123.55, -58.3) * mm});
            skLineSegment(sketch, "E4.8.0.93", {"start": v(132.15, -58.3) * mm, "end": v(132.15, -63.3) * mm});
            skLineSegment(sketch, "E4.8.0.94", {"start": v(16.55, -58.3) * mm, "end": v(16.55, -63.3) * mm});
            skLineSegment(sketch, "E4.8.0.95", {"start": v(104.95, -58.3) * mm, "end": v(104.95, -63.3) * mm});
            skLineSegment(sketch, "E4.8.0.96", {"start": v(111.75, -63.3) * mm, "end": v(116.75, -63.3) * mm});
            skLineSegment(sketch, "E4.8.0.97", {"start": v(89.55, -58.3) * mm, "end": v(89.55, -63.3) * mm});
            skLineSegment(sketch, "E4.8.0.98", {"start": v(152.55, -58.3) * mm, "end": v(157.55, -58.3) * mm});
            skLineSegment(sketch, "E4.8.0.99", {"start": v(186.55, -58.3) * mm, "end": v(191.55, -58.3) * mm});
            skLineSegment(sketch, "E4.8.0.100", {"start": v(36.95, -63.3) * mm, "end": v(41.95, -63.3) * mm});
            skLineSegment(sketch, "E4.8.0.101", {"start": v(43.75, -63.3) * mm, "end": v(48.75, -63.3) * mm});
            skLineSegment(sketch, "E4.8.0.102", {"start": v(2.95, -63.3) * mm, "end": v(9.75, -63.3) * mm, "construction": true});
            skLineSegment(sketch, "E4.8.0.103", {"start": v(159.35, -58.3) * mm, "end": v(164.35, -58.3) * mm});
            skLineSegment(sketch, "E4.8.0.104", {"start": v(166.15, -58.3) * mm, "end": v(171.15, -58.3) * mm});
            skLineSegment(sketch, "E4.8.0.105", {"start": v(172.95, -58.3) * mm, "end": v(177.95, -58.3) * mm});
            skLineSegment(sketch, "E4.8.0.106", {"start": v(16.55, -63.3) * mm, "end": v(21.55, -63.3) * mm});
            skLineSegment(sketch, "E4.8.0.107", {"start": v(30.15, -63.3) * mm, "end": v(35.15, -63.3) * mm});
            skLineSegment(sketch, "E4.8.0.108", {"start": v(23.35, -63.3) * mm, "end": v(28.35, -63.3) * mm});
            skLineSegment(sketch, "E4.8.0.109", {"start": v(9.75, -63.3) * mm, "end": v(14.75, -63.3) * mm});
            skLineSegment(sketch, "E4.8.0.110", {"start": v(50.55, -63.3) * mm, "end": v(55.55, -63.3) * mm});
            skLineSegment(sketch, "E4.8.0.111", {"start": v(179.75, -58.3) * mm, "end": v(184.75, -58.3) * mm});
            skLineSegment(sketch, "E4.8.0.112", {"start": v(2.95, -63.3) * mm, "end": v(7.95, -63.3) * mm});
            skLineSegment(sketch, "E4.9.0.0", {"start": v(111.8, -65.3) * mm, "end": v(116.8, -65.3) * mm});
            skLineSegment(sketch, "E4.9.0.1", {"start": v(116.8, -65.3) * mm, "end": v(116.8, -70.3) * mm});
            skLineSegment(sketch, "E4.9.0.2", {"start": v(125.4, -65.3) * mm, "end": v(130.4, -65.3) * mm});
            skLineSegment(sketch, "E4.9.0.3", {"start": v(28.4, -65.3) * mm, "end": v(28.4, -70.3) * mm});
            skLineSegment(sketch, "E4.9.0.4", {"start": v(71, -65.3) * mm, "end": v(76, -65.3) * mm});
            skLineSegment(sketch, "E4.9.0.5", {"start": v(173, -65.3) * mm, "end": v(173, -70.3) * mm});
            skLineSegment(sketch, "E4.9.0.6", {"start": v(48.8, -65.3) * mm, "end": v(48.8, -70.3) * mm});
            skLineSegment(sketch, "E4.9.0.7", {"start": v(84.6, -65.3) * mm, "end": v(84.6, -70.3) * mm});
            skLineSegment(sketch, "E4.9.0.8", {"start": v(14.8, -65.3) * mm, "end": v(14.8, -70.3) * mm});
            skLineSegment(sketch, "E4.9.0.9", {"start": v(98.2, -65.3) * mm, "end": v(103.2, -65.3) * mm});
            skLineSegment(sketch, "E4.9.0.10", {"start": v(166.2, -65.3) * mm, "end": v(166.2, -70.3) * mm});
            skLineSegment(sketch, "E4.9.0.11", {"start": v(91.4, -65.3) * mm, "end": v(96.4, -65.3) * mm});
            skLineSegment(sketch, "E4.9.0.12", {"start": v(71, -70.3) * mm, "end": v(76, -70.3) * mm});
            skLineSegment(sketch, "E4.9.0.13", {"start": v(132.2, -70.3) * mm, "end": v(137.2, -70.3) * mm});
            skLineSegment(sketch, "E4.9.0.14", {"start": v(145.8, -65.3) * mm, "end": v(145.8, -70.3) * mm});
            skLineSegment(sketch, "E4.9.0.15", {"start": v(105, -70.3) * mm, "end": v(110, -70.3) * mm});
            skLineSegment(sketch, "E4.9.0.16", {"start": v(191.6, -65.3) * mm, "end": v(191.6, -70.3) * mm});
            skLineSegment(sketch, "E4.9.0.17", {"start": v(159.4, -70.3) * mm, "end": v(164.4, -70.3) * mm});
            skLineSegment(sketch, "E4.9.0.18", {"start": v(76, -65.3) * mm, "end": v(76, -70.3) * mm});
            skLineSegment(sketch, "E4.9.0.19", {"start": v(23.4, -65.3) * mm, "end": v(23.4, -70.3) * mm});
            skLineSegment(sketch, "E4.9.0.20", {"start": v(145.8, -65.3) * mm, "end": v(150.8, -65.3) * mm});
            skLineSegment(sketch, "E4.9.0.21", {"start": v(139, -70.3) * mm, "end": v(144, -70.3) * mm});
            skLineSegment(sketch, "E4.9.0.22", {"start": v(184.8, -65.3) * mm, "end": v(184.8, -70.3) * mm});
            skLineSegment(sketch, "E4.9.0.23", {"start": v(55.6, -65.3) * mm, "end": v(55.6, -70.3) * mm});
            skLineSegment(sketch, "E4.9.0.24", {"start": v(171.2, -65.3) * mm, "end": v(171.2, -70.3) * mm});
            skLineSegment(sketch, "E4.9.0.25", {"start": v(62.4, -65.3) * mm, "end": v(62.4, -70.3) * mm});
            skLineSegment(sketch, "E4.9.0.26", {"start": v(69.2, -65.3) * mm, "end": v(69.2, -70.3) * mm});
            skLineSegment(sketch, "E4.9.0.27", {"start": v(132.2, -65.3) * mm, "end": v(137.2, -65.3) * mm});
            skLineSegment(sketch, "E4.9.0.28", {"start": v(64.2, -65.3) * mm, "end": v(64.2, -70.3) * mm});
            skLineSegment(sketch, "E4.9.0.29", {"start": v(152.6, -70.3) * mm, "end": v(157.6, -70.3) * mm});
            skLineSegment(sketch, "E4.9.0.30", {"start": v(179.8, -70.3) * mm, "end": v(184.8, -70.3) * mm});
            skLineSegment(sketch, "E4.9.0.31", {"start": v(37, -65.3) * mm, "end": v(37, -70.3) * mm});
            skLineSegment(sketch, "E4.9.0.32", {"start": v(173, -70.3) * mm, "end": v(178, -70.3) * mm});
            skLineSegment(sketch, "E4.9.0.33", {"start": v(91.4, -65.3) * mm, "end": v(91.4, -70.3) * mm});
            skLineSegment(sketch, "E4.9.0.34", {"start": v(77.8, -65.3) * mm, "end": v(82.8, -65.3) * mm});
            skLineSegment(sketch, "E4.9.0.35", {"start": v(71, -65.3) * mm, "end": v(71, -70.3) * mm});
            skLineSegment(sketch, "E4.9.0.36", {"start": v(57.4, -70.3) * mm, "end": v(62.4, -70.3) * mm});
            skLineSegment(sketch, "E4.9.0.37", {"start": v(111.8, -65.3) * mm, "end": v(111.8, -70.3) * mm});
            skLineSegment(sketch, "E4.9.0.38", {"start": v(150.8, -65.3) * mm, "end": v(150.8, -70.3) * mm});
            skLineSegment(sketch, "E4.9.0.39", {"start": v(178, -65.3) * mm, "end": v(178, -70.3) * mm});
            skLineSegment(sketch, "E4.9.0.40", {"start": v(179.8, -65.3) * mm, "end": v(179.8, -70.3) * mm});
            skLineSegment(sketch, "E4.9.0.41", {"start": v(98.2, -65.3) * mm, "end": v(98.2, -70.3) * mm});
            skLineSegment(sketch, "E4.9.0.42", {"start": v(37, -65.3) * mm, "end": v(42, -65.3) * mm});
            skLineSegment(sketch, "E4.9.0.43", {"start": v(118.6, -70.3) * mm, "end": v(123.6, -70.3) * mm});
            skLineSegment(sketch, "E4.9.0.44", {"start": v(8, -65.3) * mm, "end": v(8, -70.3) * mm});
            skLineSegment(sketch, "E4.9.0.45", {"start": v(43.8, -65.3) * mm, "end": v(43.8, -70.3) * mm});
            skLineSegment(sketch, "E4.9.0.46", {"start": v(77.8, -70.3) * mm, "end": v(82.8, -70.3) * mm});
            skLineSegment(sketch, "E4.9.0.47", {"start": v(139, -65.3) * mm, "end": v(144, -65.3) * mm});
            skLineSegment(sketch, "E4.9.0.48", {"start": v(23.4, -65.3) * mm, "end": v(28.4, -65.3) * mm});
            skLineSegment(sketch, "E4.9.0.49", {"start": v(152.6, -65.3) * mm, "end": v(152.6, -70.3) * mm});
            skLineSegment(sketch, "E4.9.0.50", {"start": v(57.4, -65.3) * mm, "end": v(62.4, -65.3) * mm});
            skLineSegment(sketch, "E4.9.0.51", {"start": v(43.8, -65.3) * mm, "end": v(48.8, -65.3) * mm});
            skLineSegment(sketch, "E4.9.0.52", {"start": v(42, -65.3) * mm, "end": v(42, -70.3) * mm});
            skLineSegment(sketch, "E4.9.0.53", {"start": v(125.4, -70.3) * mm, "end": v(130.4, -70.3) * mm});
            skLineSegment(sketch, "E4.9.0.54", {"start": v(186.6, -70.3) * mm, "end": v(191.6, -70.3) * mm});
            skLineSegment(sketch, "E4.9.0.55", {"start": v(125.4, -65.3) * mm, "end": v(125.4, -70.3) * mm});
            skLineSegment(sketch, "E4.9.0.56", {"start": v(64.2, -65.3) * mm, "end": v(69.2, -65.3) * mm});
            skLineSegment(sketch, "E4.9.0.57", {"start": v(64.2, -70.3) * mm, "end": v(69.2, -70.3) * mm});
            skLineSegment(sketch, "E4.9.0.58", {"start": v(164.4, -65.3) * mm, "end": v(164.4, -70.3) * mm});
            skLineSegment(sketch, "E4.9.0.59", {"start": v(186.6, -65.3) * mm, "end": v(186.6, -70.3) * mm});
            skLineSegment(sketch, "E4.9.0.60", {"start": v(9.8, -65.3) * mm, "end": v(9.8, -70.3) * mm});
            skLineSegment(sketch, "E4.9.0.61", {"start": v(84.6, -65.3) * mm, "end": v(89.6, -65.3) * mm});
            skLineSegment(sketch, "E4.9.0.62", {"start": v(9.8, -65.3) * mm, "end": v(14.8, -65.3) * mm});
            skLineSegment(sketch, "E4.9.0.63", {"start": v(50.6, -65.3) * mm, "end": v(55.6, -65.3) * mm});
            skLineSegment(sketch, "E4.9.0.64", {"start": v(110, -65.3) * mm, "end": v(110, -70.3) * mm});
            skLineSegment(sketch, "E4.9.0.65", {"start": v(91.4, -70.3) * mm, "end": v(96.4, -70.3) * mm});
            skLineSegment(sketch, "E4.9.0.66", {"start": v(103.2, -65.3) * mm, "end": v(103.2, -70.3) * mm});
            skLineSegment(sketch, "E4.9.0.67", {"start": v(3, -65.3) * mm, "end": v(8, -65.3) * mm});
            skLineSegment(sketch, "E4.9.0.68", {"start": v(98.2, -70.3) * mm, "end": v(103.2, -70.3) * mm});
            skLineSegment(sketch, "E4.9.0.69", {"start": v(123.6, -65.3) * mm, "end": v(123.6, -70.3) * mm});
            skLineSegment(sketch, "E4.9.0.70", {"start": v(84.6, -70.3) * mm, "end": v(89.6, -70.3) * mm});
            skLineSegment(sketch, "E4.9.0.71", {"start": v(16.6, -65.3) * mm, "end": v(21.6, -65.3) * mm});
            skLineSegment(sketch, "E4.9.0.72", {"start": v(30.2, -65.3) * mm, "end": v(35.2, -65.3) * mm});
            skLineSegment(sketch, "E4.9.0.73", {"start": v(77.8, -65.3) * mm, "end": v(77.8, -70.3) * mm});
            skLineSegment(sketch, "E4.9.0.74", {"start": v(3, -65.3) * mm, "end": v(3, -70.3) * mm});
            skLineSegment(sketch, "E4.9.0.75", {"start": v(30.2, -65.3) * mm, "end": v(30.2, -70.3) * mm});
            skLineSegment(sketch, "E4.9.0.76", {"start": v(159.4, -65.3) * mm, "end": v(159.4, -70.3) * mm});
            skLineSegment(sketch, "E4.9.0.77", {"start": v(105, -65.3) * mm, "end": v(110, -65.3) * mm});
            skLineSegment(sketch, "E4.9.0.78", {"start": v(82.8, -65.3) * mm, "end": v(82.8, -70.3) * mm});
            skLineSegment(sketch, "E4.9.0.79", {"start": v(35.2, -65.3) * mm, "end": v(35.2, -70.3) * mm});
            skLineSegment(sketch, "E4.9.0.80", {"start": v(157.6, -65.3) * mm, "end": v(157.6, -70.3) * mm});
            skLineSegment(sketch, "E4.9.0.81", {"start": v(21.6, -65.3) * mm, "end": v(21.6, -70.3) * mm});
            skLineSegment(sketch, "E4.9.0.82", {"start": v(144, -65.3) * mm, "end": v(144, -70.3) * mm});
            skLineSegment(sketch, "E4.9.0.83", {"start": v(139, -65.3) * mm, "end": v(139, -70.3) * mm});
            skLineSegment(sketch, "E4.9.0.84", {"start": v(130.4, -65.3) * mm, "end": v(130.4, -70.3) * mm});
            skLineSegment(sketch, "E4.9.0.85", {"start": v(57.4, -65.3) * mm, "end": v(57.4, -70.3) * mm});
            skLineSegment(sketch, "E4.9.0.86", {"start": v(137.2, -65.3) * mm, "end": v(137.2, -70.3) * mm});
            skLineSegment(sketch, "E4.9.0.87", {"start": v(118.6, -65.3) * mm, "end": v(118.6, -70.3) * mm});
            skLineSegment(sketch, "E4.9.0.88", {"start": v(96.4, -65.3) * mm, "end": v(96.4, -70.3) * mm});
            skLineSegment(sketch, "E4.9.0.89", {"start": v(145.8, -70.3) * mm, "end": v(150.8, -70.3) * mm});
            skLineSegment(sketch, "E4.9.0.90", {"start": v(166.2, -70.3) * mm, "end": v(171.2, -70.3) * mm});
            skLineSegment(sketch, "E4.9.0.91", {"start": v(50.6, -65.3) * mm, "end": v(50.6, -70.3) * mm});
            skLineSegment(sketch, "E4.9.0.92", {"start": v(118.6, -65.3) * mm, "end": v(123.6, -65.3) * mm});
            skLineSegment(sketch, "E4.9.0.93", {"start": v(132.2, -65.3) * mm, "end": v(132.2, -70.3) * mm});
            skLineSegment(sketch, "E4.9.0.94", {"start": v(16.6, -65.3) * mm, "end": v(16.6, -70.3) * mm});
            skLineSegment(sketch, "E4.9.0.95", {"start": v(105, -65.3) * mm, "end": v(105, -70.3) * mm});
            skLineSegment(sketch, "E4.9.0.96", {"start": v(111.8, -70.3) * mm, "end": v(116.8, -70.3) * mm});
            skLineSegment(sketch, "E4.9.0.97", {"start": v(89.6, -65.3) * mm, "end": v(89.6, -70.3) * mm});
            skLineSegment(sketch, "E4.9.0.98", {"start": v(152.6, -65.3) * mm, "end": v(157.6, -65.3) * mm});
            skLineSegment(sketch, "E4.9.0.99", {"start": v(186.6, -65.3) * mm, "end": v(191.6, -65.3) * mm});
            skLineSegment(sketch, "E4.9.0.100", {"start": v(37, -70.3) * mm, "end": v(42, -70.3) * mm});
            skLineSegment(sketch, "E4.9.0.101", {"start": v(43.8, -70.3) * mm, "end": v(48.8, -70.3) * mm});
            skLineSegment(sketch, "E4.9.0.102", {"start": v(3, -70.3) * mm, "end": v(9.8, -70.3) * mm, "construction": true});
            skLineSegment(sketch, "E4.9.0.103", {"start": v(159.4, -65.3) * mm, "end": v(164.4, -65.3) * mm});
            skLineSegment(sketch, "E4.9.0.104", {"start": v(166.2, -65.3) * mm, "end": v(171.2, -65.3) * mm});
            skLineSegment(sketch, "E4.9.0.105", {"start": v(173, -65.3) * mm, "end": v(178, -65.3) * mm});
            skLineSegment(sketch, "E4.9.0.106", {"start": v(16.6, -70.3) * mm, "end": v(21.6, -70.3) * mm});
            skLineSegment(sketch, "E4.9.0.107", {"start": v(30.2, -70.3) * mm, "end": v(35.2, -70.3) * mm});
            skLineSegment(sketch, "E4.9.0.108", {"start": v(23.4, -70.3) * mm, "end": v(28.4, -70.3) * mm});
            skLineSegment(sketch, "E4.9.0.109", {"start": v(9.8, -70.3) * mm, "end": v(14.8, -70.3) * mm});
            skLineSegment(sketch, "E4.9.0.110", {"start": v(50.6, -70.3) * mm, "end": v(55.6, -70.3) * mm});
            skLineSegment(sketch, "E4.9.0.111", {"start": v(179.8, -65.3) * mm, "end": v(184.8, -65.3) * mm});
            skLineSegment(sketch, "E4.9.0.112", {"start": v(3, -70.3) * mm, "end": v(8, -70.3) * mm});
            skLineSegment(sketch, "E4.10.0.0", {"start": v(111.84, -72.3) * mm, "end": v(116.84, -72.3) * mm});
            skLineSegment(sketch, "E4.10.0.1", {"start": v(116.84, -72.3) * mm, "end": v(116.84, -77.3) * mm});
            skLineSegment(sketch, "E4.10.0.2", {"start": v(125.44, -72.3) * mm, "end": v(130.44, -72.3) * mm});
            skLineSegment(sketch, "E4.10.0.3", {"start": v(28.44, -72.3) * mm, "end": v(28.44, -77.3) * mm});
            skLineSegment(sketch, "E4.10.0.4", {"start": v(71.04, -72.3) * mm, "end": v(76.04, -72.3) * mm});
            skLineSegment(sketch, "E4.10.0.5", {"start": v(173.04, -72.3) * mm, "end": v(173.04, -77.3) * mm});
            skLineSegment(sketch, "E4.10.0.6", {"start": v(48.84, -72.3) * mm, "end": v(48.84, -77.3) * mm});
            skLineSegment(sketch, "E4.10.0.7", {"start": v(84.64, -72.3) * mm, "end": v(84.64, -77.3) * mm});
            skLineSegment(sketch, "E4.10.0.8", {"start": v(14.84, -72.3) * mm, "end": v(14.84, -77.3) * mm});
            skLineSegment(sketch, "E4.10.0.9", {"start": v(98.24, -72.3) * mm, "end": v(103.24, -72.3) * mm});
            skLineSegment(sketch, "E4.10.0.10", {"start": v(166.24, -72.3) * mm, "end": v(166.24, -77.3) * mm});
            skLineSegment(sketch, "E4.10.0.11", {"start": v(91.44, -72.3) * mm, "end": v(96.44, -72.3) * mm});
            skLineSegment(sketch, "E4.10.0.12", {"start": v(71.04, -77.3) * mm, "end": v(76.04, -77.3) * mm});
            skLineSegment(sketch, "E4.10.0.13", {"start": v(132.24, -77.3) * mm, "end": v(137.24, -77.3) * mm});
            skLineSegment(sketch, "E4.10.0.14", {"start": v(145.84, -72.3) * mm, "end": v(145.84, -77.3) * mm});
            skLineSegment(sketch, "E4.10.0.15", {"start": v(105.04, -77.3) * mm, "end": v(110.04, -77.3) * mm});
            skLineSegment(sketch, "E4.10.0.16", {"start": v(191.64, -72.3) * mm, "end": v(191.64, -77.3) * mm});
            skLineSegment(sketch, "E4.10.0.17", {"start": v(159.44, -77.3) * mm, "end": v(164.44, -77.3) * mm});
            skLineSegment(sketch, "E4.10.0.18", {"start": v(76.04, -72.3) * mm, "end": v(76.04, -77.3) * mm});
            skLineSegment(sketch, "E4.10.0.19", {"start": v(23.44, -72.3) * mm, "end": v(23.44, -77.3) * mm});
            skLineSegment(sketch, "E4.10.0.20", {"start": v(145.84, -72.3) * mm, "end": v(150.84, -72.3) * mm});
            skLineSegment(sketch, "E4.10.0.21", {"start": v(139.04, -77.3) * mm, "end": v(144.04, -77.3) * mm});
            skLineSegment(sketch, "E4.10.0.22", {"start": v(184.84, -72.3) * mm, "end": v(184.84, -77.3) * mm});
            skLineSegment(sketch, "E4.10.0.23", {"start": v(55.64, -72.3) * mm, "end": v(55.64, -77.3) * mm});
            skLineSegment(sketch, "E4.10.0.24", {"start": v(171.24, -72.3) * mm, "end": v(171.24, -77.3) * mm});
            skLineSegment(sketch, "E4.10.0.25", {"start": v(62.44, -72.3) * mm, "end": v(62.44, -77.3) * mm});
            skLineSegment(sketch, "E4.10.0.26", {"start": v(69.24, -72.3) * mm, "end": v(69.24, -77.3) * mm});
            skLineSegment(sketch, "E4.10.0.27", {"start": v(132.24, -72.3) * mm, "end": v(137.24, -72.3) * mm});
            skLineSegment(sketch, "E4.10.0.28", {"start": v(64.24, -72.3) * mm, "end": v(64.24, -77.3) * mm});
            skLineSegment(sketch, "E4.10.0.29", {"start": v(152.64, -77.3) * mm, "end": v(157.64, -77.3) * mm});
            skLineSegment(sketch, "E4.10.0.30", {"start": v(179.84, -77.3) * mm, "end": v(184.84, -77.3) * mm});
            skLineSegment(sketch, "E4.10.0.31", {"start": v(37.04, -72.3) * mm, "end": v(37.04, -77.3) * mm});
            skLineSegment(sketch, "E4.10.0.32", {"start": v(173.04, -77.3) * mm, "end": v(178.04, -77.3) * mm});
            skLineSegment(sketch, "E4.10.0.33", {"start": v(91.44, -72.3) * mm, "end": v(91.44, -77.3) * mm});
            skLineSegment(sketch, "E4.10.0.34", {"start": v(77.84, -72.3) * mm, "end": v(82.84, -72.3) * mm});
            skLineSegment(sketch, "E4.10.0.35", {"start": v(71.04, -72.3) * mm, "end": v(71.04, -77.3) * mm});
            skLineSegment(sketch, "E4.10.0.36", {"start": v(57.44, -77.3) * mm, "end": v(62.44, -77.3) * mm});
            skLineSegment(sketch, "E4.10.0.37", {"start": v(111.84, -72.3) * mm, "end": v(111.84, -77.3) * mm});
            skLineSegment(sketch, "E4.10.0.38", {"start": v(150.84, -72.3) * mm, "end": v(150.84, -77.3) * mm});
            skLineSegment(sketch, "E4.10.0.39", {"start": v(178.04, -72.3) * mm, "end": v(178.04, -77.3) * mm});
            skLineSegment(sketch, "E4.10.0.40", {"start": v(179.84, -72.3) * mm, "end": v(179.84, -77.3) * mm});
            skLineSegment(sketch, "E4.10.0.41", {"start": v(98.24, -72.3) * mm, "end": v(98.24, -77.3) * mm});
            skLineSegment(sketch, "E4.10.0.42", {"start": v(37.04, -72.3) * mm, "end": v(42.04, -72.3) * mm});
            skLineSegment(sketch, "E4.10.0.43", {"start": v(118.64, -77.3) * mm, "end": v(123.64, -77.3) * mm});
            skLineSegment(sketch, "E4.10.0.44", {"start": v(8.04, -72.3) * mm, "end": v(8.04, -77.3) * mm});
            skLineSegment(sketch, "E4.10.0.45", {"start": v(43.84, -72.3) * mm, "end": v(43.84, -77.3) * mm});
            skLineSegment(sketch, "E4.10.0.46", {"start": v(77.84, -77.3) * mm, "end": v(82.84, -77.3) * mm});
            skLineSegment(sketch, "E4.10.0.47", {"start": v(139.04, -72.3) * mm, "end": v(144.04, -72.3) * mm});
            skLineSegment(sketch, "E4.10.0.48", {"start": v(23.44, -72.3) * mm, "end": v(28.44, -72.3) * mm});
            skLineSegment(sketch, "E4.10.0.49", {"start": v(152.64, -72.3) * mm, "end": v(152.64, -77.3) * mm});
            skLineSegment(sketch, "E4.10.0.50", {"start": v(57.44, -72.3) * mm, "end": v(62.44, -72.3) * mm});
            skLineSegment(sketch, "E4.10.0.51", {"start": v(43.84, -72.3) * mm, "end": v(48.84, -72.3) * mm});
            skLineSegment(sketch, "E4.10.0.52", {"start": v(42.04, -72.3) * mm, "end": v(42.04, -77.3) * mm});
            skLineSegment(sketch, "E4.10.0.53", {"start": v(125.44, -77.3) * mm, "end": v(130.44, -77.3) * mm});
            skLineSegment(sketch, "E4.10.0.54", {"start": v(186.64, -77.3) * mm, "end": v(191.64, -77.3) * mm});
            skLineSegment(sketch, "E4.10.0.55", {"start": v(125.44, -72.3) * mm, "end": v(125.44, -77.3) * mm});
            skLineSegment(sketch, "E4.10.0.56", {"start": v(64.24, -72.3) * mm, "end": v(69.24, -72.3) * mm});
            skLineSegment(sketch, "E4.10.0.57", {"start": v(64.24, -77.3) * mm, "end": v(69.24, -77.3) * mm});
            skLineSegment(sketch, "E4.10.0.58", {"start": v(164.44, -72.3) * mm, "end": v(164.44, -77.3) * mm});
            skLineSegment(sketch, "E4.10.0.59", {"start": v(186.64, -72.3) * mm, "end": v(186.64, -77.3) * mm});
            skLineSegment(sketch, "E4.10.0.60", {"start": v(9.84, -72.3) * mm, "end": v(9.84, -77.3) * mm});
            skLineSegment(sketch, "E4.10.0.61", {"start": v(84.64, -72.3) * mm, "end": v(89.64, -72.3) * mm});
            skLineSegment(sketch, "E4.10.0.62", {"start": v(9.84, -72.3) * mm, "end": v(14.84, -72.3) * mm});
            skLineSegment(sketch, "E4.10.0.63", {"start": v(50.64, -72.3) * mm, "end": v(55.64, -72.3) * mm});
            skLineSegment(sketch, "E4.10.0.64", {"start": v(110.04, -72.3) * mm, "end": v(110.04, -77.3) * mm});
            skLineSegment(sketch, "E4.10.0.65", {"start": v(91.44, -77.3) * mm, "end": v(96.44, -77.3) * mm});
            skLineSegment(sketch, "E4.10.0.66", {"start": v(103.24, -72.3) * mm, "end": v(103.24, -77.3) * mm});
            skLineSegment(sketch, "E4.10.0.67", {"start": v(3.04, -72.3) * mm, "end": v(8.04, -72.3) * mm});
            skLineSegment(sketch, "E4.10.0.68", {"start": v(98.24, -77.3) * mm, "end": v(103.24, -77.3) * mm});
            skLineSegment(sketch, "E4.10.0.69", {"start": v(123.64, -72.3) * mm, "end": v(123.64, -77.3) * mm});
            skLineSegment(sketch, "E4.10.0.70", {"start": v(84.64, -77.3) * mm, "end": v(89.64, -77.3) * mm});
            skLineSegment(sketch, "E4.10.0.71", {"start": v(16.64, -72.3) * mm, "end": v(21.64, -72.3) * mm});
            skLineSegment(sketch, "E4.10.0.72", {"start": v(30.24, -72.3) * mm, "end": v(35.24, -72.3) * mm});
            skLineSegment(sketch, "E4.10.0.73", {"start": v(77.84, -72.3) * mm, "end": v(77.84, -77.3) * mm});
            skLineSegment(sketch, "E4.10.0.74", {"start": v(3.04, -72.3) * mm, "end": v(3.04, -77.3) * mm});
            skLineSegment(sketch, "E4.10.0.75", {"start": v(30.24, -72.3) * mm, "end": v(30.24, -77.3) * mm});
            skLineSegment(sketch, "E4.10.0.76", {"start": v(159.44, -72.3) * mm, "end": v(159.44, -77.3) * mm});
            skLineSegment(sketch, "E4.10.0.77", {"start": v(105.04, -72.3) * mm, "end": v(110.04, -72.3) * mm});
            skLineSegment(sketch, "E4.10.0.78", {"start": v(82.84, -72.3) * mm, "end": v(82.84, -77.3) * mm});
            skLineSegment(sketch, "E4.10.0.79", {"start": v(35.24, -72.3) * mm, "end": v(35.24, -77.3) * mm});
            skLineSegment(sketch, "E4.10.0.80", {"start": v(157.64, -72.3) * mm, "end": v(157.64, -77.3) * mm});
            skLineSegment(sketch, "E4.10.0.81", {"start": v(21.64, -72.3) * mm, "end": v(21.64, -77.3) * mm});
            skLineSegment(sketch, "E4.10.0.82", {"start": v(144.04, -72.3) * mm, "end": v(144.04, -77.3) * mm});
            skLineSegment(sketch, "E4.10.0.83", {"start": v(139.04, -72.3) * mm, "end": v(139.04, -77.3) * mm});
            skLineSegment(sketch, "E4.10.0.84", {"start": v(130.44, -72.3) * mm, "end": v(130.44, -77.3) * mm});
            skLineSegment(sketch, "E4.10.0.85", {"start": v(57.44, -72.3) * mm, "end": v(57.44, -77.3) * mm});
            skLineSegment(sketch, "E4.10.0.86", {"start": v(137.24, -72.3) * mm, "end": v(137.24, -77.3) * mm});
            skLineSegment(sketch, "E4.10.0.87", {"start": v(118.64, -72.3) * mm, "end": v(118.64, -77.3) * mm});
            skLineSegment(sketch, "E4.10.0.88", {"start": v(96.44, -72.3) * mm, "end": v(96.44, -77.3) * mm});
            skLineSegment(sketch, "E4.10.0.89", {"start": v(145.84, -77.3) * mm, "end": v(150.84, -77.3) * mm});
            skLineSegment(sketch, "E4.10.0.90", {"start": v(166.24, -77.3) * mm, "end": v(171.24, -77.3) * mm});
            skLineSegment(sketch, "E4.10.0.91", {"start": v(50.64, -72.3) * mm, "end": v(50.64, -77.3) * mm});
            skLineSegment(sketch, "E4.10.0.92", {"start": v(118.64, -72.3) * mm, "end": v(123.64, -72.3) * mm});
            skLineSegment(sketch, "E4.10.0.93", {"start": v(132.24, -72.3) * mm, "end": v(132.24, -77.3) * mm});
            skLineSegment(sketch, "E4.10.0.94", {"start": v(16.64, -72.3) * mm, "end": v(16.64, -77.3) * mm});
            skLineSegment(sketch, "E4.10.0.95", {"start": v(105.04, -72.3) * mm, "end": v(105.04, -77.3) * mm});
            skLineSegment(sketch, "E4.10.0.96", {"start": v(111.84, -77.3) * mm, "end": v(116.84, -77.3) * mm});
            skLineSegment(sketch, "E4.10.0.97", {"start": v(89.64, -72.3) * mm, "end": v(89.64, -77.3) * mm});
            skLineSegment(sketch, "E4.10.0.98", {"start": v(152.64, -72.3) * mm, "end": v(157.64, -72.3) * mm});
            skLineSegment(sketch, "E4.10.0.99", {"start": v(186.64, -72.3) * mm, "end": v(191.64, -72.3) * mm});
            skLineSegment(sketch, "E4.10.0.100", {"start": v(37.04, -77.3) * mm, "end": v(42.04, -77.3) * mm});
            skLineSegment(sketch, "E4.10.0.101", {"start": v(43.84, -77.3) * mm, "end": v(48.84, -77.3) * mm});
            skLineSegment(sketch, "E4.10.0.102", {"start": v(3.04, -77.3) * mm, "end": v(9.84, -77.3) * mm, "construction": true});
            skLineSegment(sketch, "E4.10.0.103", {"start": v(159.44, -72.3) * mm, "end": v(164.44, -72.3) * mm});
            skLineSegment(sketch, "E4.10.0.104", {"start": v(166.24, -72.3) * mm, "end": v(171.24, -72.3) * mm});
            skLineSegment(sketch, "E4.10.0.105", {"start": v(173.04, -72.3) * mm, "end": v(178.04, -72.3) * mm});
            skLineSegment(sketch, "E4.10.0.106", {"start": v(16.64, -77.3) * mm, "end": v(21.64, -77.3) * mm});
            skLineSegment(sketch, "E4.10.0.107", {"start": v(30.24, -77.3) * mm, "end": v(35.24, -77.3) * mm});
            skLineSegment(sketch, "E4.10.0.108", {"start": v(23.44, -77.3) * mm, "end": v(28.44, -77.3) * mm});
            skLineSegment(sketch, "E4.10.0.109", {"start": v(9.84, -77.3) * mm, "end": v(14.84, -77.3) * mm});
            skLineSegment(sketch, "E4.10.0.110", {"start": v(50.64, -77.3) * mm, "end": v(55.64, -77.3) * mm});
            skLineSegment(sketch, "E4.10.0.111", {"start": v(179.84, -72.3) * mm, "end": v(184.84, -72.3) * mm});
            skLineSegment(sketch, "E4.10.0.112", {"start": v(3.04, -77.3) * mm, "end": v(8.04, -77.3) * mm});
            skLineSegment(sketch, "E4.11.0.0", {"start": v(111.89, -79.3) * mm, "end": v(116.89, -79.3) * mm});
            skLineSegment(sketch, "E4.11.0.1", {"start": v(116.89, -79.3) * mm, "end": v(116.89, -84.3) * mm});
            skLineSegment(sketch, "E4.11.0.2", {"start": v(125.49, -79.3) * mm, "end": v(130.49, -79.3) * mm});
            skLineSegment(sketch, "E4.11.0.3", {"start": v(28.49, -79.3) * mm, "end": v(28.49, -84.3) * mm});
            skLineSegment(sketch, "E4.11.0.4", {"start": v(71.09, -79.3) * mm, "end": v(76.09, -79.3) * mm});
            skLineSegment(sketch, "E4.11.0.5", {"start": v(173.09, -79.3) * mm, "end": v(173.09, -84.3) * mm});
            skLineSegment(sketch, "E4.11.0.6", {"start": v(48.89, -79.3) * mm, "end": v(48.89, -84.3) * mm});
            skLineSegment(sketch, "E4.11.0.7", {"start": v(84.69, -79.3) * mm, "end": v(84.69, -84.3) * mm});
            skLineSegment(sketch, "E4.11.0.8", {"start": v(14.89, -79.3) * mm, "end": v(14.89, -84.3) * mm});
            skLineSegment(sketch, "E4.11.0.9", {"start": v(98.29, -79.3) * mm, "end": v(103.29, -79.3) * mm});
            skLineSegment(sketch, "E4.11.0.10", {"start": v(166.29, -79.3) * mm, "end": v(166.29, -84.3) * mm});
            skLineSegment(sketch, "E4.11.0.11", {"start": v(91.49, -79.3) * mm, "end": v(96.49, -79.3) * mm});
            skLineSegment(sketch, "E4.11.0.12", {"start": v(71.09, -84.3) * mm, "end": v(76.09, -84.3) * mm});
            skLineSegment(sketch, "E4.11.0.13", {"start": v(132.29, -84.3) * mm, "end": v(137.29, -84.3) * mm});
            skLineSegment(sketch, "E4.11.0.14", {"start": v(145.89, -79.3) * mm, "end": v(145.89, -84.3) * mm});
            skLineSegment(sketch, "E4.11.0.15", {"start": v(105.09, -84.3) * mm, "end": v(110.09, -84.3) * mm});
            skLineSegment(sketch, "E4.11.0.16", {"start": v(191.69, -79.3) * mm, "end": v(191.69, -84.3) * mm});
            skLineSegment(sketch, "E4.11.0.17", {"start": v(159.49, -84.3) * mm, "end": v(164.49, -84.3) * mm});
            skLineSegment(sketch, "E4.11.0.18", {"start": v(76.09, -79.3) * mm, "end": v(76.09, -84.3) * mm});
            skLineSegment(sketch, "E4.11.0.19", {"start": v(23.49, -79.3) * mm, "end": v(23.49, -84.3) * mm});
            skLineSegment(sketch, "E4.11.0.20", {"start": v(145.89, -79.3) * mm, "end": v(150.89, -79.3) * mm});
            skLineSegment(sketch, "E4.11.0.21", {"start": v(139.09, -84.3) * mm, "end": v(144.09, -84.3) * mm});
            skLineSegment(sketch, "E4.11.0.22", {"start": v(184.89, -79.3) * mm, "end": v(184.89, -84.3) * mm});
            skLineSegment(sketch, "E4.11.0.23", {"start": v(55.69, -79.3) * mm, "end": v(55.69, -84.3) * mm});
            skLineSegment(sketch, "E4.11.0.24", {"start": v(171.29, -79.3) * mm, "end": v(171.29, -84.3) * mm});
            skLineSegment(sketch, "E4.11.0.25", {"start": v(62.49, -79.3) * mm, "end": v(62.49, -84.3) * mm});
            skLineSegment(sketch, "E4.11.0.26", {"start": v(69.29, -79.3) * mm, "end": v(69.29, -84.3) * mm});
            skLineSegment(sketch, "E4.11.0.27", {"start": v(132.29, -79.3) * mm, "end": v(137.29, -79.3) * mm});
            skLineSegment(sketch, "E4.11.0.28", {"start": v(64.29, -79.3) * mm, "end": v(64.29, -84.3) * mm});
            skLineSegment(sketch, "E4.11.0.29", {"start": v(152.69, -84.3) * mm, "end": v(157.69, -84.3) * mm});
            skLineSegment(sketch, "E4.11.0.30", {"start": v(179.89, -84.3) * mm, "end": v(184.89, -84.3) * mm});
            skLineSegment(sketch, "E4.11.0.31", {"start": v(37.09, -79.3) * mm, "end": v(37.09, -84.3) * mm});
            skLineSegment(sketch, "E4.11.0.32", {"start": v(173.09, -84.3) * mm, "end": v(178.09, -84.3) * mm});
            skLineSegment(sketch, "E4.11.0.33", {"start": v(91.49, -79.3) * mm, "end": v(91.49, -84.3) * mm});
            skLineSegment(sketch, "E4.11.0.34", {"start": v(77.89, -79.3) * mm, "end": v(82.89, -79.3) * mm});
            skLineSegment(sketch, "E4.11.0.35", {"start": v(71.09, -79.3) * mm, "end": v(71.09, -84.3) * mm});
            skLineSegment(sketch, "E4.11.0.36", {"start": v(57.49, -84.3) * mm, "end": v(62.49, -84.3) * mm});
            skLineSegment(sketch, "E4.11.0.37", {"start": v(111.89, -79.3) * mm, "end": v(111.89, -84.3) * mm});
            skLineSegment(sketch, "E4.11.0.38", {"start": v(150.89, -79.3) * mm, "end": v(150.89, -84.3) * mm});
            skLineSegment(sketch, "E4.11.0.39", {"start": v(178.09, -79.3) * mm, "end": v(178.09, -84.3) * mm});
            skLineSegment(sketch, "E4.11.0.40", {"start": v(179.89, -79.3) * mm, "end": v(179.89, -84.3) * mm});
            skLineSegment(sketch, "E4.11.0.41", {"start": v(98.29, -79.3) * mm, "end": v(98.29, -84.3) * mm});
            skLineSegment(sketch, "E4.11.0.42", {"start": v(37.09, -79.3) * mm, "end": v(42.09, -79.3) * mm});
            skLineSegment(sketch, "E4.11.0.43", {"start": v(118.69, -84.3) * mm, "end": v(123.69, -84.3) * mm});
            skLineSegment(sketch, "E4.11.0.44", {"start": v(8.09, -79.3) * mm, "end": v(8.09, -84.3) * mm});
            skLineSegment(sketch, "E4.11.0.45", {"start": v(43.89, -79.3) * mm, "end": v(43.89, -84.3) * mm});
            skLineSegment(sketch, "E4.11.0.46", {"start": v(77.89, -84.3) * mm, "end": v(82.89, -84.3) * mm});
            skLineSegment(sketch, "E4.11.0.47", {"start": v(139.09, -79.3) * mm, "end": v(144.09, -79.3) * mm});
            skLineSegment(sketch, "E4.11.0.48", {"start": v(23.49, -79.3) * mm, "end": v(28.49, -79.3) * mm});
            skLineSegment(sketch, "E4.11.0.49", {"start": v(152.69, -79.3) * mm, "end": v(152.69, -84.3) * mm});
            skLineSegment(sketch, "E4.11.0.50", {"start": v(57.49, -79.3) * mm, "end": v(62.49, -79.3) * mm});
            skLineSegment(sketch, "E4.11.0.51", {"start": v(43.89, -79.3) * mm, "end": v(48.89, -79.3) * mm});
            skLineSegment(sketch, "E4.11.0.52", {"start": v(42.09, -79.3) * mm, "end": v(42.09, -84.3) * mm});
            skLineSegment(sketch, "E4.11.0.53", {"start": v(125.49, -84.3) * mm, "end": v(130.49, -84.3) * mm});
            skLineSegment(sketch, "E4.11.0.54", {"start": v(186.69, -84.3) * mm, "end": v(191.69, -84.3) * mm});
            skLineSegment(sketch, "E4.11.0.55", {"start": v(125.49, -79.3) * mm, "end": v(125.49, -84.3) * mm});
            skLineSegment(sketch, "E4.11.0.56", {"start": v(64.29, -79.3) * mm, "end": v(69.29, -79.3) * mm});
            skLineSegment(sketch, "E4.11.0.57", {"start": v(64.29, -84.3) * mm, "end": v(69.29, -84.3) * mm});
            skLineSegment(sketch, "E4.11.0.58", {"start": v(164.49, -79.3) * mm, "end": v(164.49, -84.3) * mm});
            skLineSegment(sketch, "E4.11.0.59", {"start": v(186.69, -79.3) * mm, "end": v(186.69, -84.3) * mm});
            skLineSegment(sketch, "E4.11.0.60", {"start": v(9.89, -79.3) * mm, "end": v(9.89, -84.3) * mm});
            skLineSegment(sketch, "E4.11.0.61", {"start": v(84.69, -79.3) * mm, "end": v(89.69, -79.3) * mm});
            skLineSegment(sketch, "E4.11.0.62", {"start": v(9.89, -79.3) * mm, "end": v(14.89, -79.3) * mm});
            skLineSegment(sketch, "E4.11.0.63", {"start": v(50.69, -79.3) * mm, "end": v(55.69, -79.3) * mm});
            skLineSegment(sketch, "E4.11.0.64", {"start": v(110.09, -79.3) * mm, "end": v(110.09, -84.3) * mm});
            skLineSegment(sketch, "E4.11.0.65", {"start": v(91.49, -84.3) * mm, "end": v(96.49, -84.3) * mm});
            skLineSegment(sketch, "E4.11.0.66", {"start": v(103.29, -79.3) * mm, "end": v(103.29, -84.3) * mm});
            skLineSegment(sketch, "E4.11.0.67", {"start": v(3.09, -79.3) * mm, "end": v(8.09, -79.3) * mm});
            skLineSegment(sketch, "E4.11.0.68", {"start": v(98.29, -84.3) * mm, "end": v(103.29, -84.3) * mm});
            skLineSegment(sketch, "E4.11.0.69", {"start": v(123.69, -79.3) * mm, "end": v(123.69, -84.3) * mm});
            skLineSegment(sketch, "E4.11.0.70", {"start": v(84.69, -84.3) * mm, "end": v(89.69, -84.3) * mm});
            skLineSegment(sketch, "E4.11.0.71", {"start": v(16.69, -79.3) * mm, "end": v(21.69, -79.3) * mm});
            skLineSegment(sketch, "E4.11.0.72", {"start": v(30.29, -79.3) * mm, "end": v(35.29, -79.3) * mm});
            skLineSegment(sketch, "E4.11.0.73", {"start": v(77.89, -79.3) * mm, "end": v(77.89, -84.3) * mm});
            skLineSegment(sketch, "E4.11.0.74", {"start": v(3.09, -79.3) * mm, "end": v(3.09, -84.3) * mm});
            skLineSegment(sketch, "E4.11.0.75", {"start": v(30.29, -79.3) * mm, "end": v(30.29, -84.3) * mm});
            skLineSegment(sketch, "E4.11.0.76", {"start": v(159.49, -79.3) * mm, "end": v(159.49, -84.3) * mm});
            skLineSegment(sketch, "E4.11.0.77", {"start": v(105.09, -79.3) * mm, "end": v(110.09, -79.3) * mm});
            skLineSegment(sketch, "E4.11.0.78", {"start": v(82.89, -79.3) * mm, "end": v(82.89, -84.3) * mm});
            skLineSegment(sketch, "E4.11.0.79", {"start": v(35.29, -79.3) * mm, "end": v(35.29, -84.3) * mm});
            skLineSegment(sketch, "E4.11.0.80", {"start": v(157.69, -79.3) * mm, "end": v(157.69, -84.3) * mm});
            skLineSegment(sketch, "E4.11.0.81", {"start": v(21.69, -79.3) * mm, "end": v(21.69, -84.3) * mm});
            skLineSegment(sketch, "E4.11.0.82", {"start": v(144.09, -79.3) * mm, "end": v(144.09, -84.3) * mm});
            skLineSegment(sketch, "E4.11.0.83", {"start": v(139.09, -79.3) * mm, "end": v(139.09, -84.3) * mm});
            skLineSegment(sketch, "E4.11.0.84", {"start": v(130.49, -79.3) * mm, "end": v(130.49, -84.3) * mm});
            skLineSegment(sketch, "E4.11.0.85", {"start": v(57.49, -79.3) * mm, "end": v(57.49, -84.3) * mm});
            skLineSegment(sketch, "E4.11.0.86", {"start": v(137.29, -79.3) * mm, "end": v(137.29, -84.3) * mm});
            skLineSegment(sketch, "E4.11.0.87", {"start": v(118.69, -79.3) * mm, "end": v(118.69, -84.3) * mm});
            skLineSegment(sketch, "E4.11.0.88", {"start": v(96.49, -79.3) * mm, "end": v(96.49, -84.3) * mm});
            skLineSegment(sketch, "E4.11.0.89", {"start": v(145.89, -84.3) * mm, "end": v(150.89, -84.3) * mm});
            skLineSegment(sketch, "E4.11.0.90", {"start": v(166.29, -84.3) * mm, "end": v(171.29, -84.3) * mm});
            skLineSegment(sketch, "E4.11.0.91", {"start": v(50.69, -79.3) * mm, "end": v(50.69, -84.3) * mm});
            skLineSegment(sketch, "E4.11.0.92", {"start": v(118.69, -79.3) * mm, "end": v(123.69, -79.3) * mm});
            skLineSegment(sketch, "E4.11.0.93", {"start": v(132.29, -79.3) * mm, "end": v(132.29, -84.3) * mm});
            skLineSegment(sketch, "E4.11.0.94", {"start": v(16.69, -79.3) * mm, "end": v(16.69, -84.3) * mm});
            skLineSegment(sketch, "E4.11.0.95", {"start": v(105.09, -79.3) * mm, "end": v(105.09, -84.3) * mm});
            skLineSegment(sketch, "E4.11.0.96", {"start": v(111.89, -84.3) * mm, "end": v(116.89, -84.3) * mm});
            skLineSegment(sketch, "E4.11.0.97", {"start": v(89.69, -79.3) * mm, "end": v(89.69, -84.3) * mm});
            skLineSegment(sketch, "E4.11.0.98", {"start": v(152.69, -79.3) * mm, "end": v(157.69, -79.3) * mm});
            skLineSegment(sketch, "E4.11.0.99", {"start": v(186.69, -79.3) * mm, "end": v(191.69, -79.3) * mm});
            skLineSegment(sketch, "E4.11.0.100", {"start": v(37.09, -84.3) * mm, "end": v(42.09, -84.3) * mm});
            skLineSegment(sketch, "E4.11.0.101", {"start": v(43.89, -84.3) * mm, "end": v(48.89, -84.3) * mm});
            skLineSegment(sketch, "E4.11.0.102", {"start": v(3.09, -84.3) * mm, "end": v(9.89, -84.3) * mm, "construction": true});
            skLineSegment(sketch, "E4.11.0.103", {"start": v(159.49, -79.3) * mm, "end": v(164.49, -79.3) * mm});
            skLineSegment(sketch, "E4.11.0.104", {"start": v(166.29, -79.3) * mm, "end": v(171.29, -79.3) * mm});
            skLineSegment(sketch, "E4.11.0.105", {"start": v(173.09, -79.3) * mm, "end": v(178.09, -79.3) * mm});
            skLineSegment(sketch, "E4.11.0.106", {"start": v(16.69, -84.3) * mm, "end": v(21.69, -84.3) * mm});
            skLineSegment(sketch, "E4.11.0.107", {"start": v(30.29, -84.3) * mm, "end": v(35.29, -84.3) * mm});
            skLineSegment(sketch, "E4.11.0.108", {"start": v(23.49, -84.3) * mm, "end": v(28.49, -84.3) * mm});
            skLineSegment(sketch, "E4.11.0.109", {"start": v(9.89, -84.3) * mm, "end": v(14.89, -84.3) * mm});
            skLineSegment(sketch, "E4.11.0.110", {"start": v(50.69, -84.3) * mm, "end": v(55.69, -84.3) * mm});
            skLineSegment(sketch, "E4.11.0.111", {"start": v(179.89, -79.3) * mm, "end": v(184.89, -79.3) * mm});
            skLineSegment(sketch, "E4.11.0.112", {"start": v(3.09, -84.3) * mm, "end": v(8.09, -84.3) * mm});
            skLineSegment(sketch, "E4.12.0.0", {"start": v(111.94, -86.3) * mm, "end": v(116.94, -86.3) * mm});
            skLineSegment(sketch, "E4.12.0.1", {"start": v(116.94, -86.3) * mm, "end": v(116.94, -91.3) * mm});
            skLineSegment(sketch, "E4.12.0.2", {"start": v(125.54, -86.3) * mm, "end": v(130.54, -86.3) * mm});
            skLineSegment(sketch, "E4.12.0.3", {"start": v(28.54, -86.3) * mm, "end": v(28.54, -91.3) * mm});
            skLineSegment(sketch, "E4.12.0.4", {"start": v(71.14, -86.3) * mm, "end": v(76.14, -86.3) * mm});
            skLineSegment(sketch, "E4.12.0.5", {"start": v(173.14, -86.3) * mm, "end": v(173.14, -91.3) * mm});
            skLineSegment(sketch, "E4.12.0.6", {"start": v(48.94, -86.3) * mm, "end": v(48.94, -91.3) * mm});
            skLineSegment(sketch, "E4.12.0.7", {"start": v(84.74, -86.3) * mm, "end": v(84.74, -91.3) * mm});
            skLineSegment(sketch, "E4.12.0.8", {"start": v(14.94, -86.3) * mm, "end": v(14.94, -91.3) * mm});
            skLineSegment(sketch, "E4.12.0.9", {"start": v(98.34, -86.3) * mm, "end": v(103.34, -86.3) * mm});
            skLineSegment(sketch, "E4.12.0.10", {"start": v(166.34, -86.3) * mm, "end": v(166.34, -91.3) * mm});
            skLineSegment(sketch, "E4.12.0.11", {"start": v(91.54, -86.3) * mm, "end": v(96.54, -86.3) * mm});
            skLineSegment(sketch, "E4.12.0.12", {"start": v(71.14, -91.3) * mm, "end": v(76.14, -91.3) * mm});
            skLineSegment(sketch, "E4.12.0.13", {"start": v(132.34, -91.3) * mm, "end": v(137.34, -91.3) * mm});
            skLineSegment(sketch, "E4.12.0.14", {"start": v(145.94, -86.3) * mm, "end": v(145.94, -91.3) * mm});
            skLineSegment(sketch, "E4.12.0.15", {"start": v(105.14, -91.3) * mm, "end": v(110.14, -91.3) * mm});
            skLineSegment(sketch, "E4.12.0.16", {"start": v(191.74, -86.3) * mm, "end": v(191.74, -91.3) * mm});
            skLineSegment(sketch, "E4.12.0.17", {"start": v(159.54, -91.3) * mm, "end": v(164.54, -91.3) * mm});
            skLineSegment(sketch, "E4.12.0.18", {"start": v(76.14, -86.3) * mm, "end": v(76.14, -91.3) * mm});
            skLineSegment(sketch, "E4.12.0.19", {"start": v(23.54, -86.3) * mm, "end": v(23.54, -91.3) * mm});
            skLineSegment(sketch, "E4.12.0.20", {"start": v(145.94, -86.3) * mm, "end": v(150.94, -86.3) * mm});
            skLineSegment(sketch, "E4.12.0.21", {"start": v(139.14, -91.3) * mm, "end": v(144.14, -91.3) * mm});
            skLineSegment(sketch, "E4.12.0.22", {"start": v(184.94, -86.3) * mm, "end": v(184.94, -91.3) * mm});
            skLineSegment(sketch, "E4.12.0.23", {"start": v(55.74, -86.3) * mm, "end": v(55.74, -91.3) * mm});
            skLineSegment(sketch, "E4.12.0.24", {"start": v(171.34, -86.3) * mm, "end": v(171.34, -91.3) * mm});
            skLineSegment(sketch, "E4.12.0.25", {"start": v(62.54, -86.3) * mm, "end": v(62.54, -91.3) * mm});
            skLineSegment(sketch, "E4.12.0.26", {"start": v(69.34, -86.3) * mm, "end": v(69.34, -91.3) * mm});
            skLineSegment(sketch, "E4.12.0.27", {"start": v(132.34, -86.3) * mm, "end": v(137.34, -86.3) * mm});
            skLineSegment(sketch, "E4.12.0.28", {"start": v(64.34, -86.3) * mm, "end": v(64.34, -91.3) * mm});
            skLineSegment(sketch, "E4.12.0.29", {"start": v(152.74, -91.3) * mm, "end": v(157.74, -91.3) * mm});
            skLineSegment(sketch, "E4.12.0.30", {"start": v(179.94, -91.3) * mm, "end": v(184.94, -91.3) * mm});
            skLineSegment(sketch, "E4.12.0.31", {"start": v(37.14, -86.3) * mm, "end": v(37.14, -91.3) * mm});
            skLineSegment(sketch, "E4.12.0.32", {"start": v(173.14, -91.3) * mm, "end": v(178.14, -91.3) * mm});
            skLineSegment(sketch, "E4.12.0.33", {"start": v(91.54, -86.3) * mm, "end": v(91.54, -91.3) * mm});
            skLineSegment(sketch, "E4.12.0.34", {"start": v(77.94, -86.3) * mm, "end": v(82.94, -86.3) * mm});
            skLineSegment(sketch, "E4.12.0.35", {"start": v(71.14, -86.3) * mm, "end": v(71.14, -91.3) * mm});
            skLineSegment(sketch, "E4.12.0.36", {"start": v(57.54, -91.3) * mm, "end": v(62.54, -91.3) * mm});
            skLineSegment(sketch, "E4.12.0.37", {"start": v(111.94, -86.3) * mm, "end": v(111.94, -91.3) * mm});
            skLineSegment(sketch, "E4.12.0.38", {"start": v(150.94, -86.3) * mm, "end": v(150.94, -91.3) * mm});
            skLineSegment(sketch, "E4.12.0.39", {"start": v(178.14, -86.3) * mm, "end": v(178.14, -91.3) * mm});
            skLineSegment(sketch, "E4.12.0.40", {"start": v(179.94, -86.3) * mm, "end": v(179.94, -91.3) * mm});
            skLineSegment(sketch, "E4.12.0.41", {"start": v(98.34, -86.3) * mm, "end": v(98.34, -91.3) * mm});
            skLineSegment(sketch, "E4.12.0.42", {"start": v(37.14, -86.3) * mm, "end": v(42.14, -86.3) * mm});
            skLineSegment(sketch, "E4.12.0.43", {"start": v(118.74, -91.3) * mm, "end": v(123.74, -91.3) * mm});
            skLineSegment(sketch, "E4.12.0.44", {"start": v(8.14, -86.3) * mm, "end": v(8.14, -91.3) * mm});
            skLineSegment(sketch, "E4.12.0.45", {"start": v(43.94, -86.3) * mm, "end": v(43.94, -91.3) * mm});
            skLineSegment(sketch, "E4.12.0.46", {"start": v(77.94, -91.3) * mm, "end": v(82.94, -91.3) * mm});
            skLineSegment(sketch, "E4.12.0.47", {"start": v(139.14, -86.3) * mm, "end": v(144.14, -86.3) * mm});
            skLineSegment(sketch, "E4.12.0.48", {"start": v(23.54, -86.3) * mm, "end": v(28.54, -86.3) * mm});
            skLineSegment(sketch, "E4.12.0.49", {"start": v(152.74, -86.3) * mm, "end": v(152.74, -91.3) * mm});
            skLineSegment(sketch, "E4.12.0.50", {"start": v(57.54, -86.3) * mm, "end": v(62.54, -86.3) * mm});
            skLineSegment(sketch, "E4.12.0.51", {"start": v(43.94, -86.3) * mm, "end": v(48.94, -86.3) * mm});
            skLineSegment(sketch, "E4.12.0.52", {"start": v(42.14, -86.3) * mm, "end": v(42.14, -91.3) * mm});
            skLineSegment(sketch, "E4.12.0.53", {"start": v(125.54, -91.3) * mm, "end": v(130.54, -91.3) * mm});
            skLineSegment(sketch, "E4.12.0.54", {"start": v(186.74, -91.3) * mm, "end": v(191.74, -91.3) * mm});
            skLineSegment(sketch, "E4.12.0.55", {"start": v(125.54, -86.3) * mm, "end": v(125.54, -91.3) * mm});
            skLineSegment(sketch, "E4.12.0.56", {"start": v(64.34, -86.3) * mm, "end": v(69.34, -86.3) * mm});
            skLineSegment(sketch, "E4.12.0.57", {"start": v(64.34, -91.3) * mm, "end": v(69.34, -91.3) * mm});
            skLineSegment(sketch, "E4.12.0.58", {"start": v(164.54, -86.3) * mm, "end": v(164.54, -91.3) * mm});
            skLineSegment(sketch, "E4.12.0.59", {"start": v(186.74, -86.3) * mm, "end": v(186.74, -91.3) * mm});
            skLineSegment(sketch, "E4.12.0.60", {"start": v(9.94, -86.3) * mm, "end": v(9.94, -91.3) * mm});
            skLineSegment(sketch, "E4.12.0.61", {"start": v(84.74, -86.3) * mm, "end": v(89.74, -86.3) * mm});
            skLineSegment(sketch, "E4.12.0.62", {"start": v(9.94, -86.3) * mm, "end": v(14.94, -86.3) * mm});
            skLineSegment(sketch, "E4.12.0.63", {"start": v(50.74, -86.3) * mm, "end": v(55.74, -86.3) * mm});
            skLineSegment(sketch, "E4.12.0.64", {"start": v(110.14, -86.3) * mm, "end": v(110.14, -91.3) * mm});
            skLineSegment(sketch, "E4.12.0.65", {"start": v(91.54, -91.3) * mm, "end": v(96.54, -91.3) * mm});
            skLineSegment(sketch, "E4.12.0.66", {"start": v(103.34, -86.3) * mm, "end": v(103.34, -91.3) * mm});
            skLineSegment(sketch, "E4.12.0.67", {"start": v(3.14, -86.3) * mm, "end": v(8.14, -86.3) * mm});
            skLineSegment(sketch, "E4.12.0.68", {"start": v(98.34, -91.3) * mm, "end": v(103.34, -91.3) * mm});
            skLineSegment(sketch, "E4.12.0.69", {"start": v(123.74, -86.3) * mm, "end": v(123.74, -91.3) * mm});
            skLineSegment(sketch, "E4.12.0.70", {"start": v(84.74, -91.3) * mm, "end": v(89.74, -91.3) * mm});
            skLineSegment(sketch, "E4.12.0.71", {"start": v(16.74, -86.3) * mm, "end": v(21.74, -86.3) * mm});
            skLineSegment(sketch, "E4.12.0.72", {"start": v(30.34, -86.3) * mm, "end": v(35.34, -86.3) * mm});
            skLineSegment(sketch, "E4.12.0.73", {"start": v(77.94, -86.3) * mm, "end": v(77.94, -91.3) * mm});
            skLineSegment(sketch, "E4.12.0.74", {"start": v(3.14, -86.3) * mm, "end": v(3.14, -91.3) * mm});
            skLineSegment(sketch, "E4.12.0.75", {"start": v(30.34, -86.3) * mm, "end": v(30.34, -91.3) * mm});
            skLineSegment(sketch, "E4.12.0.76", {"start": v(159.54, -86.3) * mm, "end": v(159.54, -91.3) * mm});
            skLineSegment(sketch, "E4.12.0.77", {"start": v(105.14, -86.3) * mm, "end": v(110.14, -86.3) * mm});
            skLineSegment(sketch, "E4.12.0.78", {"start": v(82.94, -86.3) * mm, "end": v(82.94, -91.3) * mm});
            skLineSegment(sketch, "E4.12.0.79", {"start": v(35.34, -86.3) * mm, "end": v(35.34, -91.3) * mm});
            skLineSegment(sketch, "E4.12.0.80", {"start": v(157.74, -86.3) * mm, "end": v(157.74, -91.3) * mm});
            skLineSegment(sketch, "E4.12.0.81", {"start": v(21.74, -86.3) * mm, "end": v(21.74, -91.3) * mm});
            skLineSegment(sketch, "E4.12.0.82", {"start": v(144.14, -86.3) * mm, "end": v(144.14, -91.3) * mm});
            skLineSegment(sketch, "E4.12.0.83", {"start": v(139.14, -86.3) * mm, "end": v(139.14, -91.3) * mm});
            skLineSegment(sketch, "E4.12.0.84", {"start": v(130.54, -86.3) * mm, "end": v(130.54, -91.3) * mm});
            skLineSegment(sketch, "E4.12.0.85", {"start": v(57.54, -86.3) * mm, "end": v(57.54, -91.3) * mm});
            skLineSegment(sketch, "E4.12.0.86", {"start": v(137.34, -86.3) * mm, "end": v(137.34, -91.3) * mm});
            skLineSegment(sketch, "E4.12.0.87", {"start": v(118.74, -86.3) * mm, "end": v(118.74, -91.3) * mm});
            skLineSegment(sketch, "E4.12.0.88", {"start": v(96.54, -86.3) * mm, "end": v(96.54, -91.3) * mm});
            skLineSegment(sketch, "E4.12.0.89", {"start": v(145.94, -91.3) * mm, "end": v(150.94, -91.3) * mm});
            skLineSegment(sketch, "E4.12.0.90", {"start": v(166.34, -91.3) * mm, "end": v(171.34, -91.3) * mm});
            skLineSegment(sketch, "E4.12.0.91", {"start": v(50.74, -86.3) * mm, "end": v(50.74, -91.3) * mm});
            skLineSegment(sketch, "E4.12.0.92", {"start": v(118.74, -86.3) * mm, "end": v(123.74, -86.3) * mm});
            skLineSegment(sketch, "E4.12.0.93", {"start": v(132.34, -86.3) * mm, "end": v(132.34, -91.3) * mm});
            skLineSegment(sketch, "E4.12.0.94", {"start": v(16.74, -86.3) * mm, "end": v(16.74, -91.3) * mm});
            skLineSegment(sketch, "E4.12.0.95", {"start": v(105.14, -86.3) * mm, "end": v(105.14, -91.3) * mm});
            skLineSegment(sketch, "E4.12.0.96", {"start": v(111.94, -91.3) * mm, "end": v(116.94, -91.3) * mm});
            skLineSegment(sketch, "E4.12.0.97", {"start": v(89.74, -86.3) * mm, "end": v(89.74, -91.3) * mm});
            skLineSegment(sketch, "E4.12.0.98", {"start": v(152.74, -86.3) * mm, "end": v(157.74, -86.3) * mm});
            skLineSegment(sketch, "E4.12.0.99", {"start": v(186.74, -86.3) * mm, "end": v(191.74, -86.3) * mm});
            skLineSegment(sketch, "E4.12.0.100", {"start": v(37.14, -91.3) * mm, "end": v(42.14, -91.3) * mm});
            skLineSegment(sketch, "E4.12.0.101", {"start": v(43.94, -91.3) * mm, "end": v(48.94, -91.3) * mm});
            skLineSegment(sketch, "E4.12.0.102", {"start": v(3.14, -91.3) * mm, "end": v(9.94, -91.3) * mm, "construction": true});
            skLineSegment(sketch, "E4.12.0.103", {"start": v(159.54, -86.3) * mm, "end": v(164.54, -86.3) * mm});
            skLineSegment(sketch, "E4.12.0.104", {"start": v(166.34, -86.3) * mm, "end": v(171.34, -86.3) * mm});
            skLineSegment(sketch, "E4.12.0.105", {"start": v(173.14, -86.3) * mm, "end": v(178.14, -86.3) * mm});
            skLineSegment(sketch, "E4.12.0.106", {"start": v(16.74, -91.3) * mm, "end": v(21.74, -91.3) * mm});
            skLineSegment(sketch, "E4.12.0.107", {"start": v(30.34, -91.3) * mm, "end": v(35.34, -91.3) * mm});
            skLineSegment(sketch, "E4.12.0.108", {"start": v(23.54, -91.3) * mm, "end": v(28.54, -91.3) * mm});
            skLineSegment(sketch, "E4.12.0.109", {"start": v(9.94, -91.3) * mm, "end": v(14.94, -91.3) * mm});
            skLineSegment(sketch, "E4.12.0.110", {"start": v(50.74, -91.3) * mm, "end": v(55.74, -91.3) * mm});
            skLineSegment(sketch, "E4.12.0.111", {"start": v(179.94, -86.3) * mm, "end": v(184.94, -86.3) * mm});
            skLineSegment(sketch, "E4.12.0.112", {"start": v(3.14, -91.3) * mm, "end": v(8.14, -91.3) * mm});
            skLineSegment(sketch, "E4.13.0.0", {"start": v(111.98, -93.3) * mm, "end": v(116.98, -93.3) * mm});
            skLineSegment(sketch, "E4.13.0.1", {"start": v(116.98, -93.3) * mm, "end": v(116.98, -98.3) * mm});
            skLineSegment(sketch, "E4.13.0.2", {"start": v(125.58, -93.3) * mm, "end": v(130.58, -93.3) * mm});
            skLineSegment(sketch, "E4.13.0.3", {"start": v(28.58, -93.3) * mm, "end": v(28.58, -98.3) * mm});
            skLineSegment(sketch, "E4.13.0.4", {"start": v(71.18, -93.3) * mm, "end": v(76.18, -93.3) * mm});
            skLineSegment(sketch, "E4.13.0.5", {"start": v(173.18, -93.3) * mm, "end": v(173.18, -98.3) * mm});
            skLineSegment(sketch, "E4.13.0.6", {"start": v(48.98, -93.3) * mm, "end": v(48.98, -98.3) * mm});
            skLineSegment(sketch, "E4.13.0.7", {"start": v(84.78, -93.3) * mm, "end": v(84.78, -98.3) * mm});
            skLineSegment(sketch, "E4.13.0.8", {"start": v(14.98, -93.3) * mm, "end": v(14.98, -98.3) * mm});
            skLineSegment(sketch, "E4.13.0.9", {"start": v(98.38, -93.3) * mm, "end": v(103.38, -93.3) * mm});
            skLineSegment(sketch, "E4.13.0.10", {"start": v(166.38, -93.3) * mm, "end": v(166.38, -98.3) * mm});
            skLineSegment(sketch, "E4.13.0.11", {"start": v(91.58, -93.3) * mm, "end": v(96.58, -93.3) * mm});
            skLineSegment(sketch, "E4.13.0.12", {"start": v(71.18, -98.3) * mm, "end": v(76.18, -98.3) * mm});
            skLineSegment(sketch, "E4.13.0.13", {"start": v(132.38, -98.3) * mm, "end": v(137.38, -98.3) * mm});
            skLineSegment(sketch, "E4.13.0.14", {"start": v(145.98, -93.3) * mm, "end": v(145.98, -98.3) * mm});
            skLineSegment(sketch, "E4.13.0.15", {"start": v(105.18, -98.3) * mm, "end": v(110.18, -98.3) * mm});
            skLineSegment(sketch, "E4.13.0.16", {"start": v(191.78, -93.3) * mm, "end": v(191.78, -98.3) * mm});
            skLineSegment(sketch, "E4.13.0.17", {"start": v(159.58, -98.3) * mm, "end": v(164.58, -98.3) * mm});
            skLineSegment(sketch, "E4.13.0.18", {"start": v(76.18, -93.3) * mm, "end": v(76.18, -98.3) * mm});
            skLineSegment(sketch, "E4.13.0.19", {"start": v(23.58, -93.3) * mm, "end": v(23.58, -98.3) * mm});
            skLineSegment(sketch, "E4.13.0.20", {"start": v(145.98, -93.3) * mm, "end": v(150.98, -93.3) * mm});
            skLineSegment(sketch, "E4.13.0.21", {"start": v(139.18, -98.3) * mm, "end": v(144.18, -98.3) * mm});
            skLineSegment(sketch, "E4.13.0.22", {"start": v(184.98, -93.3) * mm, "end": v(184.98, -98.3) * mm});
            skLineSegment(sketch, "E4.13.0.23", {"start": v(55.78, -93.3) * mm, "end": v(55.78, -98.3) * mm});
            skLineSegment(sketch, "E4.13.0.24", {"start": v(171.38, -93.3) * mm, "end": v(171.38, -98.3) * mm});
            skLineSegment(sketch, "E4.13.0.25", {"start": v(62.58, -93.3) * mm, "end": v(62.58, -98.3) * mm});
            skLineSegment(sketch, "E4.13.0.26", {"start": v(69.38, -93.3) * mm, "end": v(69.38, -98.3) * mm});
            skLineSegment(sketch, "E4.13.0.27", {"start": v(132.38, -93.3) * mm, "end": v(137.38, -93.3) * mm});
            skLineSegment(sketch, "E4.13.0.28", {"start": v(64.38, -93.3) * mm, "end": v(64.38, -98.3) * mm});
            skLineSegment(sketch, "E4.13.0.29", {"start": v(152.78, -98.3) * mm, "end": v(157.78, -98.3) * mm});
            skLineSegment(sketch, "E4.13.0.30", {"start": v(179.98, -98.3) * mm, "end": v(184.98, -98.3) * mm});
            skLineSegment(sketch, "E4.13.0.31", {"start": v(37.18, -93.3) * mm, "end": v(37.18, -98.3) * mm});
            skLineSegment(sketch, "E4.13.0.32", {"start": v(173.18, -98.3) * mm, "end": v(178.18, -98.3) * mm});
            skLineSegment(sketch, "E4.13.0.33", {"start": v(91.58, -93.3) * mm, "end": v(91.58, -98.3) * mm});
            skLineSegment(sketch, "E4.13.0.34", {"start": v(77.98, -93.3) * mm, "end": v(82.98, -93.3) * mm});
            skLineSegment(sketch, "E4.13.0.35", {"start": v(71.18, -93.3) * mm, "end": v(71.18, -98.3) * mm});
            skLineSegment(sketch, "E4.13.0.36", {"start": v(57.58, -98.3) * mm, "end": v(62.58, -98.3) * mm});
            skLineSegment(sketch, "E4.13.0.37", {"start": v(111.98, -93.3) * mm, "end": v(111.98, -98.3) * mm});
            skLineSegment(sketch, "E4.13.0.38", {"start": v(150.98, -93.3) * mm, "end": v(150.98, -98.3) * mm});
            skLineSegment(sketch, "E4.13.0.39", {"start": v(178.18, -93.3) * mm, "end": v(178.18, -98.3) * mm});
            skLineSegment(sketch, "E4.13.0.40", {"start": v(179.98, -93.3) * mm, "end": v(179.98, -98.3) * mm});
            skLineSegment(sketch, "E4.13.0.41", {"start": v(98.38, -93.3) * mm, "end": v(98.38, -98.3) * mm});
            skLineSegment(sketch, "E4.13.0.42", {"start": v(37.18, -93.3) * mm, "end": v(42.18, -93.3) * mm});
            skLineSegment(sketch, "E4.13.0.43", {"start": v(118.78, -98.3) * mm, "end": v(123.78, -98.3) * mm});
            skLineSegment(sketch, "E4.13.0.44", {"start": v(8.18, -93.3) * mm, "end": v(8.18, -98.3) * mm});
            skLineSegment(sketch, "E4.13.0.45", {"start": v(43.98, -93.3) * mm, "end": v(43.98, -98.3) * mm});
            skLineSegment(sketch, "E4.13.0.46", {"start": v(77.98, -98.3) * mm, "end": v(82.98, -98.3) * mm});
            skLineSegment(sketch, "E4.13.0.47", {"start": v(139.18, -93.3) * mm, "end": v(144.18, -93.3) * mm});
            skLineSegment(sketch, "E4.13.0.48", {"start": v(23.58, -93.3) * mm, "end": v(28.58, -93.3) * mm});
            skLineSegment(sketch, "E4.13.0.49", {"start": v(152.78, -93.3) * mm, "end": v(152.78, -98.3) * mm});
            skLineSegment(sketch, "E4.13.0.50", {"start": v(57.58, -93.3) * mm, "end": v(62.58, -93.3) * mm});
            skLineSegment(sketch, "E4.13.0.51", {"start": v(43.98, -93.3) * mm, "end": v(48.98, -93.3) * mm});
            skLineSegment(sketch, "E4.13.0.52", {"start": v(42.18, -93.3) * mm, "end": v(42.18, -98.3) * mm});
            skLineSegment(sketch, "E4.13.0.53", {"start": v(125.58, -98.3) * mm, "end": v(130.58, -98.3) * mm});
            skLineSegment(sketch, "E4.13.0.54", {"start": v(186.78, -98.3) * mm, "end": v(191.78, -98.3) * mm});
            skLineSegment(sketch, "E4.13.0.55", {"start": v(125.58, -93.3) * mm, "end": v(125.58, -98.3) * mm});
            skLineSegment(sketch, "E4.13.0.56", {"start": v(64.38, -93.3) * mm, "end": v(69.38, -93.3) * mm});
            skLineSegment(sketch, "E4.13.0.57", {"start": v(64.38, -98.3) * mm, "end": v(69.38, -98.3) * mm});
            skLineSegment(sketch, "E4.13.0.58", {"start": v(164.58, -93.3) * mm, "end": v(164.58, -98.3) * mm});
            skLineSegment(sketch, "E4.13.0.59", {"start": v(186.78, -93.3) * mm, "end": v(186.78, -98.3) * mm});
            skLineSegment(sketch, "E4.13.0.60", {"start": v(9.98, -93.3) * mm, "end": v(9.98, -98.3) * mm});
            skLineSegment(sketch, "E4.13.0.61", {"start": v(84.78, -93.3) * mm, "end": v(89.78, -93.3) * mm});
            skLineSegment(sketch, "E4.13.0.62", {"start": v(9.98, -93.3) * mm, "end": v(14.98, -93.3) * mm});
            skLineSegment(sketch, "E4.13.0.63", {"start": v(50.78, -93.3) * mm, "end": v(55.78, -93.3) * mm});
            skLineSegment(sketch, "E4.13.0.64", {"start": v(110.18, -93.3) * mm, "end": v(110.18, -98.3) * mm});
            skLineSegment(sketch, "E4.13.0.65", {"start": v(91.58, -98.3) * mm, "end": v(96.58, -98.3) * mm});
            skLineSegment(sketch, "E4.13.0.66", {"start": v(103.38, -93.3) * mm, "end": v(103.38, -98.3) * mm});
            skLineSegment(sketch, "E4.13.0.67", {"start": v(3.18, -93.3) * mm, "end": v(8.18, -93.3) * mm});
            skLineSegment(sketch, "E4.13.0.68", {"start": v(98.38, -98.3) * mm, "end": v(103.38, -98.3) * mm});
            skLineSegment(sketch, "E4.13.0.69", {"start": v(123.78, -93.3) * mm, "end": v(123.78, -98.3) * mm});
            skLineSegment(sketch, "E4.13.0.70", {"start": v(84.78, -98.3) * mm, "end": v(89.78, -98.3) * mm});
            skLineSegment(sketch, "E4.13.0.71", {"start": v(16.78, -93.3) * mm, "end": v(21.78, -93.3) * mm});
            skLineSegment(sketch, "E4.13.0.72", {"start": v(30.38, -93.3) * mm, "end": v(35.38, -93.3) * mm});
            skLineSegment(sketch, "E4.13.0.73", {"start": v(77.98, -93.3) * mm, "end": v(77.98, -98.3) * mm});
            skLineSegment(sketch, "E4.13.0.74", {"start": v(3.18, -93.3) * mm, "end": v(3.18, -98.3) * mm});
            skLineSegment(sketch, "E4.13.0.75", {"start": v(30.38, -93.3) * mm, "end": v(30.38, -98.3) * mm});
            skLineSegment(sketch, "E4.13.0.76", {"start": v(159.58, -93.3) * mm, "end": v(159.58, -98.3) * mm});
            skLineSegment(sketch, "E4.13.0.77", {"start": v(105.18, -93.3) * mm, "end": v(110.18, -93.3) * mm});
            skLineSegment(sketch, "E4.13.0.78", {"start": v(82.98, -93.3) * mm, "end": v(82.98, -98.3) * mm});
            skLineSegment(sketch, "E4.13.0.79", {"start": v(35.38, -93.3) * mm, "end": v(35.38, -98.3) * mm});
            skLineSegment(sketch, "E4.13.0.80", {"start": v(157.78, -93.3) * mm, "end": v(157.78, -98.3) * mm});
            skLineSegment(sketch, "E4.13.0.81", {"start": v(21.78, -93.3) * mm, "end": v(21.78, -98.3) * mm});
            skLineSegment(sketch, "E4.13.0.82", {"start": v(144.18, -93.3) * mm, "end": v(144.18, -98.3) * mm});
            skLineSegment(sketch, "E4.13.0.83", {"start": v(139.18, -93.3) * mm, "end": v(139.18, -98.3) * mm});
            skLineSegment(sketch, "E4.13.0.84", {"start": v(130.58, -93.3) * mm, "end": v(130.58, -98.3) * mm});
            skLineSegment(sketch, "E4.13.0.85", {"start": v(57.58, -93.3) * mm, "end": v(57.58, -98.3) * mm});
            skLineSegment(sketch, "E4.13.0.86", {"start": v(137.38, -93.3) * mm, "end": v(137.38, -98.3) * mm});
            skLineSegment(sketch, "E4.13.0.87", {"start": v(118.78, -93.3) * mm, "end": v(118.78, -98.3) * mm});
            skLineSegment(sketch, "E4.13.0.88", {"start": v(96.58, -93.3) * mm, "end": v(96.58, -98.3) * mm});
            skLineSegment(sketch, "E4.13.0.89", {"start": v(145.98, -98.3) * mm, "end": v(150.98, -98.3) * mm});
            skLineSegment(sketch, "E4.13.0.90", {"start": v(166.38, -98.3) * mm, "end": v(171.38, -98.3) * mm});
            skLineSegment(sketch, "E4.13.0.91", {"start": v(50.78, -93.3) * mm, "end": v(50.78, -98.3) * mm});
            skLineSegment(sketch, "E4.13.0.92", {"start": v(118.78, -93.3) * mm, "end": v(123.78, -93.3) * mm});
            skLineSegment(sketch, "E4.13.0.93", {"start": v(132.38, -93.3) * mm, "end": v(132.38, -98.3) * mm});
            skLineSegment(sketch, "E4.13.0.94", {"start": v(16.78, -93.3) * mm, "end": v(16.78, -98.3) * mm});
            skLineSegment(sketch, "E4.13.0.95", {"start": v(105.18, -93.3) * mm, "end": v(105.18, -98.3) * mm});
            skLineSegment(sketch, "E4.13.0.96", {"start": v(111.98, -98.3) * mm, "end": v(116.98, -98.3) * mm});
            skLineSegment(sketch, "E4.13.0.97", {"start": v(89.78, -93.3) * mm, "end": v(89.78, -98.3) * mm});
            skLineSegment(sketch, "E4.13.0.98", {"start": v(152.78, -93.3) * mm, "end": v(157.78, -93.3) * mm});
            skLineSegment(sketch, "E4.13.0.99", {"start": v(186.78, -93.3) * mm, "end": v(191.78, -93.3) * mm});
            skLineSegment(sketch, "E4.13.0.100", {"start": v(37.18, -98.3) * mm, "end": v(42.18, -98.3) * mm});
            skLineSegment(sketch, "E4.13.0.101", {"start": v(43.98, -98.3) * mm, "end": v(48.98, -98.3) * mm});
            skLineSegment(sketch, "E4.13.0.102", {"start": v(3.18, -98.3) * mm, "end": v(9.98, -98.3) * mm, "construction": true});
            skLineSegment(sketch, "E4.13.0.103", {"start": v(159.58, -93.3) * mm, "end": v(164.58, -93.3) * mm});
            skLineSegment(sketch, "E4.13.0.104", {"start": v(166.38, -93.3) * mm, "end": v(171.38, -93.3) * mm});
            skLineSegment(sketch, "E4.13.0.105", {"start": v(173.18, -93.3) * mm, "end": v(178.18, -93.3) * mm});
            skLineSegment(sketch, "E4.13.0.106", {"start": v(16.78, -98.3) * mm, "end": v(21.78, -98.3) * mm});
            skLineSegment(sketch, "E4.13.0.107", {"start": v(30.38, -98.3) * mm, "end": v(35.38, -98.3) * mm});
            skLineSegment(sketch, "E4.13.0.108", {"start": v(23.58, -98.3) * mm, "end": v(28.58, -98.3) * mm});
            skLineSegment(sketch, "E4.13.0.109", {"start": v(9.98, -98.3) * mm, "end": v(14.98, -98.3) * mm});
            skLineSegment(sketch, "E4.13.0.110", {"start": v(50.78, -98.3) * mm, "end": v(55.78, -98.3) * mm});
            skLineSegment(sketch, "E4.13.0.111", {"start": v(179.98, -93.3) * mm, "end": v(184.98, -93.3) * mm});
            skLineSegment(sketch, "E4.13.0.112", {"start": v(3.18, -98.3) * mm, "end": v(8.18, -98.3) * mm});
            skLineSegment(sketch, "E4.14.0.0", {"start": v(112.03, -100.3) * mm, "end": v(117.03, -100.3) * mm});
            skLineSegment(sketch, "E4.14.0.1", {"start": v(117.03, -100.3) * mm, "end": v(117.03, -105.3) * mm});
            skLineSegment(sketch, "E4.14.0.2", {"start": v(125.63, -100.3) * mm, "end": v(130.63, -100.3) * mm});
            skLineSegment(sketch, "E4.14.0.3", {"start": v(28.63, -100.3) * mm, "end": v(28.63, -105.3) * mm});
            skLineSegment(sketch, "E4.14.0.4", {"start": v(71.23, -100.3) * mm, "end": v(76.23, -100.3) * mm});
            skLineSegment(sketch, "E4.14.0.5", {"start": v(173.23, -100.3) * mm, "end": v(173.23, -105.3) * mm});
            skLineSegment(sketch, "E4.14.0.6", {"start": v(49.03, -100.3) * mm, "end": v(49.03, -105.3) * mm});
            skLineSegment(sketch, "E4.14.0.7", {"start": v(84.83, -100.3) * mm, "end": v(84.83, -105.3) * mm});
            skLineSegment(sketch, "E4.14.0.8", {"start": v(15.03, -100.3) * mm, "end": v(15.03, -105.3) * mm});
            skLineSegment(sketch, "E4.14.0.9", {"start": v(98.43, -100.3) * mm, "end": v(103.43, -100.3) * mm});
            skLineSegment(sketch, "E4.14.0.10", {"start": v(166.43, -100.3) * mm, "end": v(166.43, -105.3) * mm});
            skLineSegment(sketch, "E4.14.0.11", {"start": v(91.63, -100.3) * mm, "end": v(96.63, -100.3) * mm});
            skLineSegment(sketch, "E4.14.0.12", {"start": v(71.23, -105.3) * mm, "end": v(76.23, -105.3) * mm});
            skLineSegment(sketch, "E4.14.0.13", {"start": v(132.43, -105.3) * mm, "end": v(137.43, -105.3) * mm});
            skLineSegment(sketch, "E4.14.0.14", {"start": v(146.03, -100.3) * mm, "end": v(146.03, -105.3) * mm});
            skLineSegment(sketch, "E4.14.0.15", {"start": v(105.23, -105.3) * mm, "end": v(110.23, -105.3) * mm});
            skLineSegment(sketch, "E4.14.0.16", {"start": v(191.83, -100.3) * mm, "end": v(191.83, -105.3) * mm});
            skLineSegment(sketch, "E4.14.0.17", {"start": v(159.63, -105.3) * mm, "end": v(164.63, -105.3) * mm});
            skLineSegment(sketch, "E4.14.0.18", {"start": v(76.23, -100.3) * mm, "end": v(76.23, -105.3) * mm});
            skLineSegment(sketch, "E4.14.0.19", {"start": v(23.63, -100.3) * mm, "end": v(23.63, -105.3) * mm});
            skLineSegment(sketch, "E4.14.0.20", {"start": v(146.03, -100.3) * mm, "end": v(151.03, -100.3) * mm});
            skLineSegment(sketch, "E4.14.0.21", {"start": v(139.23, -105.3) * mm, "end": v(144.23, -105.3) * mm});
            skLineSegment(sketch, "E4.14.0.22", {"start": v(185.03, -100.3) * mm, "end": v(185.03, -105.3) * mm});
            skLineSegment(sketch, "E4.14.0.23", {"start": v(55.83, -100.3) * mm, "end": v(55.83, -105.3) * mm});
            skLineSegment(sketch, "E4.14.0.24", {"start": v(171.43, -100.3) * mm, "end": v(171.43, -105.3) * mm});
            skLineSegment(sketch, "E4.14.0.25", {"start": v(62.63, -100.3) * mm, "end": v(62.63, -105.3) * mm});
            skLineSegment(sketch, "E4.14.0.26", {"start": v(69.43, -100.3) * mm, "end": v(69.43, -105.3) * mm});
            skLineSegment(sketch, "E4.14.0.27", {"start": v(132.43, -100.3) * mm, "end": v(137.43, -100.3) * mm});
            skLineSegment(sketch, "E4.14.0.28", {"start": v(64.43, -100.3) * mm, "end": v(64.43, -105.3) * mm});
            skLineSegment(sketch, "E4.14.0.29", {"start": v(152.83, -105.3) * mm, "end": v(157.83, -105.3) * mm});
            skLineSegment(sketch, "E4.14.0.30", {"start": v(180.03, -105.3) * mm, "end": v(185.03, -105.3) * mm});
            skLineSegment(sketch, "E4.14.0.31", {"start": v(37.23, -100.3) * mm, "end": v(37.23, -105.3) * mm});
            skLineSegment(sketch, "E4.14.0.32", {"start": v(173.23, -105.3) * mm, "end": v(178.23, -105.3) * mm});
            skLineSegment(sketch, "E4.14.0.33", {"start": v(91.63, -100.3) * mm, "end": v(91.63, -105.3) * mm});
            skLineSegment(sketch, "E4.14.0.34", {"start": v(78.03, -100.3) * mm, "end": v(83.03, -100.3) * mm});
            skLineSegment(sketch, "E4.14.0.35", {"start": v(71.23, -100.3) * mm, "end": v(71.23, -105.3) * mm});
            skLineSegment(sketch, "E4.14.0.36", {"start": v(57.63, -105.3) * mm, "end": v(62.63, -105.3) * mm});
            skLineSegment(sketch, "E4.14.0.37", {"start": v(112.03, -100.3) * mm, "end": v(112.03, -105.3) * mm});
            skLineSegment(sketch, "E4.14.0.38", {"start": v(151.03, -100.3) * mm, "end": v(151.03, -105.3) * mm});
            skLineSegment(sketch, "E4.14.0.39", {"start": v(178.23, -100.3) * mm, "end": v(178.23, -105.3) * mm});
            skLineSegment(sketch, "E4.14.0.40", {"start": v(180.03, -100.3) * mm, "end": v(180.03, -105.3) * mm});
            skLineSegment(sketch, "E4.14.0.41", {"start": v(98.43, -100.3) * mm, "end": v(98.43, -105.3) * mm});
            skLineSegment(sketch, "E4.14.0.42", {"start": v(37.23, -100.3) * mm, "end": v(42.23, -100.3) * mm});
            skLineSegment(sketch, "E4.14.0.43", {"start": v(118.83, -105.3) * mm, "end": v(123.83, -105.3) * mm});
            skLineSegment(sketch, "E4.14.0.44", {"start": v(8.23, -100.3) * mm, "end": v(8.23, -105.3) * mm});
            skLineSegment(sketch, "E4.14.0.45", {"start": v(44.03, -100.3) * mm, "end": v(44.03, -105.3) * mm});
            skLineSegment(sketch, "E4.14.0.46", {"start": v(78.03, -105.3) * mm, "end": v(83.03, -105.3) * mm});
            skLineSegment(sketch, "E4.14.0.47", {"start": v(139.23, -100.3) * mm, "end": v(144.23, -100.3) * mm});
            skLineSegment(sketch, "E4.14.0.48", {"start": v(23.63, -100.3) * mm, "end": v(28.63, -100.3) * mm});
            skLineSegment(sketch, "E4.14.0.49", {"start": v(152.83, -100.3) * mm, "end": v(152.83, -105.3) * mm});
            skLineSegment(sketch, "E4.14.0.50", {"start": v(57.63, -100.3) * mm, "end": v(62.63, -100.3) * mm});
            skLineSegment(sketch, "E4.14.0.51", {"start": v(44.03, -100.3) * mm, "end": v(49.03, -100.3) * mm});
            skLineSegment(sketch, "E4.14.0.52", {"start": v(42.23, -100.3) * mm, "end": v(42.23, -105.3) * mm});
            skLineSegment(sketch, "E4.14.0.53", {"start": v(125.63, -105.3) * mm, "end": v(130.63, -105.3) * mm});
            skLineSegment(sketch, "E4.14.0.54", {"start": v(186.83, -105.3) * mm, "end": v(191.83, -105.3) * mm});
            skLineSegment(sketch, "E4.14.0.55", {"start": v(125.63, -100.3) * mm, "end": v(125.63, -105.3) * mm});
            skLineSegment(sketch, "E4.14.0.56", {"start": v(64.43, -100.3) * mm, "end": v(69.43, -100.3) * mm});
            skLineSegment(sketch, "E4.14.0.57", {"start": v(64.43, -105.3) * mm, "end": v(69.43, -105.3) * mm});
            skLineSegment(sketch, "E4.14.0.58", {"start": v(164.63, -100.3) * mm, "end": v(164.63, -105.3) * mm});
            skLineSegment(sketch, "E4.14.0.59", {"start": v(186.83, -100.3) * mm, "end": v(186.83, -105.3) * mm});
            skLineSegment(sketch, "E4.14.0.60", {"start": v(10.03, -100.3) * mm, "end": v(10.03, -105.3) * mm});
            skLineSegment(sketch, "E4.14.0.61", {"start": v(84.83, -100.3) * mm, "end": v(89.83, -100.3) * mm});
            skLineSegment(sketch, "E4.14.0.62", {"start": v(10.03, -100.3) * mm, "end": v(15.03, -100.3) * mm});
            skLineSegment(sketch, "E4.14.0.63", {"start": v(50.83, -100.3) * mm, "end": v(55.83, -100.3) * mm});
            skLineSegment(sketch, "E4.14.0.64", {"start": v(110.23, -100.3) * mm, "end": v(110.23, -105.3) * mm});
            skLineSegment(sketch, "E4.14.0.65", {"start": v(91.63, -105.3) * mm, "end": v(96.63, -105.3) * mm});
            skLineSegment(sketch, "E4.14.0.66", {"start": v(103.43, -100.3) * mm, "end": v(103.43, -105.3) * mm});
            skLineSegment(sketch, "E4.14.0.67", {"start": v(3.23, -100.3) * mm, "end": v(8.23, -100.3) * mm});
            skLineSegment(sketch, "E4.14.0.68", {"start": v(98.43, -105.3) * mm, "end": v(103.43, -105.3) * mm});
            skLineSegment(sketch, "E4.14.0.69", {"start": v(123.83, -100.3) * mm, "end": v(123.83, -105.3) * mm});
            skLineSegment(sketch, "E4.14.0.70", {"start": v(84.83, -105.3) * mm, "end": v(89.83, -105.3) * mm});
            skLineSegment(sketch, "E4.14.0.71", {"start": v(16.83, -100.3) * mm, "end": v(21.83, -100.3) * mm});
            skLineSegment(sketch, "E4.14.0.72", {"start": v(30.43, -100.3) * mm, "end": v(35.43, -100.3) * mm});
            skLineSegment(sketch, "E4.14.0.73", {"start": v(78.03, -100.3) * mm, "end": v(78.03, -105.3) * mm});
            skLineSegment(sketch, "E4.14.0.74", {"start": v(3.23, -100.3) * mm, "end": v(3.23, -105.3) * mm});
            skLineSegment(sketch, "E4.14.0.75", {"start": v(30.43, -100.3) * mm, "end": v(30.43, -105.3) * mm});
            skLineSegment(sketch, "E4.14.0.76", {"start": v(159.63, -100.3) * mm, "end": v(159.63, -105.3) * mm});
            skLineSegment(sketch, "E4.14.0.77", {"start": v(105.23, -100.3) * mm, "end": v(110.23, -100.3) * mm});
            skLineSegment(sketch, "E4.14.0.78", {"start": v(83.03, -100.3) * mm, "end": v(83.03, -105.3) * mm});
            skLineSegment(sketch, "E4.14.0.79", {"start": v(35.43, -100.3) * mm, "end": v(35.43, -105.3) * mm});
            skLineSegment(sketch, "E4.14.0.80", {"start": v(157.83, -100.3) * mm, "end": v(157.83, -105.3) * mm});
            skLineSegment(sketch, "E4.14.0.81", {"start": v(21.83, -100.3) * mm, "end": v(21.83, -105.3) * mm});
            skLineSegment(sketch, "E4.14.0.82", {"start": v(144.23, -100.3) * mm, "end": v(144.23, -105.3) * mm});
            skLineSegment(sketch, "E4.14.0.83", {"start": v(139.23, -100.3) * mm, "end": v(139.23, -105.3) * mm});
            skLineSegment(sketch, "E4.14.0.84", {"start": v(130.63, -100.3) * mm, "end": v(130.63, -105.3) * mm});
            skLineSegment(sketch, "E4.14.0.85", {"start": v(57.63, -100.3) * mm, "end": v(57.63, -105.3) * mm});
            skLineSegment(sketch, "E4.14.0.86", {"start": v(137.43, -100.3) * mm, "end": v(137.43, -105.3) * mm});
            skLineSegment(sketch, "E4.14.0.87", {"start": v(118.83, -100.3) * mm, "end": v(118.83, -105.3) * mm});
            skLineSegment(sketch, "E4.14.0.88", {"start": v(96.63, -100.3) * mm, "end": v(96.63, -105.3) * mm});
            skLineSegment(sketch, "E4.14.0.89", {"start": v(146.03, -105.3) * mm, "end": v(151.03, -105.3) * mm});
            skLineSegment(sketch, "E4.14.0.90", {"start": v(166.43, -105.3) * mm, "end": v(171.43, -105.3) * mm});
            skLineSegment(sketch, "E4.14.0.91", {"start": v(50.83, -100.3) * mm, "end": v(50.83, -105.3) * mm});
            skLineSegment(sketch, "E4.14.0.92", {"start": v(118.83, -100.3) * mm, "end": v(123.83, -100.3) * mm});
            skLineSegment(sketch, "E4.14.0.93", {"start": v(132.43, -100.3) * mm, "end": v(132.43, -105.3) * mm});
            skLineSegment(sketch, "E4.14.0.94", {"start": v(16.83, -100.3) * mm, "end": v(16.83, -105.3) * mm});
            skLineSegment(sketch, "E4.14.0.95", {"start": v(105.23, -100.3) * mm, "end": v(105.23, -105.3) * mm});
            skLineSegment(sketch, "E4.14.0.96", {"start": v(112.03, -105.3) * mm, "end": v(117.03, -105.3) * mm});
            skLineSegment(sketch, "E4.14.0.97", {"start": v(89.83, -100.3) * mm, "end": v(89.83, -105.3) * mm});
            skLineSegment(sketch, "E4.14.0.98", {"start": v(152.83, -100.3) * mm, "end": v(157.83, -100.3) * mm});
            skLineSegment(sketch, "E4.14.0.99", {"start": v(186.83, -100.3) * mm, "end": v(191.83, -100.3) * mm});
            skLineSegment(sketch, "E4.14.0.100", {"start": v(37.23, -105.3) * mm, "end": v(42.23, -105.3) * mm});
            skLineSegment(sketch, "E4.14.0.101", {"start": v(44.03, -105.3) * mm, "end": v(49.03, -105.3) * mm});
            skLineSegment(sketch, "E4.14.0.102", {"start": v(3.23, -105.3) * mm, "end": v(10.03, -105.3) * mm, "construction": true});
            skLineSegment(sketch, "E4.14.0.103", {"start": v(159.63, -100.3) * mm, "end": v(164.63, -100.3) * mm});
            skLineSegment(sketch, "E4.14.0.104", {"start": v(166.43, -100.3) * mm, "end": v(171.43, -100.3) * mm});
            skLineSegment(sketch, "E4.14.0.105", {"start": v(173.23, -100.3) * mm, "end": v(178.23, -100.3) * mm});
            skLineSegment(sketch, "E4.14.0.106", {"start": v(16.83, -105.3) * mm, "end": v(21.83, -105.3) * mm});
            skLineSegment(sketch, "E4.14.0.107", {"start": v(30.43, -105.3) * mm, "end": v(35.43, -105.3) * mm});
            skLineSegment(sketch, "E4.14.0.108", {"start": v(23.63, -105.3) * mm, "end": v(28.63, -105.3) * mm});
            skLineSegment(sketch, "E4.14.0.109", {"start": v(10.03, -105.3) * mm, "end": v(15.03, -105.3) * mm});
            skLineSegment(sketch, "E4.14.0.110", {"start": v(50.83, -105.3) * mm, "end": v(55.83, -105.3) * mm});
            skLineSegment(sketch, "E4.14.0.111", {"start": v(180.03, -100.3) * mm, "end": v(185.03, -100.3) * mm});
            skLineSegment(sketch, "E4.14.0.112", {"start": v(3.23, -105.3) * mm, "end": v(8.23, -105.3) * mm});
            skLineSegment(sketch, "E4.15.0.0", {"start": v(112.07, -107.3) * mm, "end": v(117.07, -107.3) * mm});
            skLineSegment(sketch, "E4.15.0.1", {"start": v(117.07, -107.3) * mm, "end": v(117.07, -112.3) * mm});
            skLineSegment(sketch, "E4.15.0.2", {"start": v(125.67, -107.3) * mm, "end": v(130.67, -107.3) * mm});
            skLineSegment(sketch, "E4.15.0.3", {"start": v(28.67, -107.3) * mm, "end": v(28.67, -112.3) * mm});
            skLineSegment(sketch, "E4.15.0.4", {"start": v(71.27, -107.3) * mm, "end": v(76.27, -107.3) * mm});
            skLineSegment(sketch, "E4.15.0.5", {"start": v(173.27, -107.3) * mm, "end": v(173.27, -112.3) * mm});
            skLineSegment(sketch, "E4.15.0.6", {"start": v(49.07, -107.3) * mm, "end": v(49.07, -112.3) * mm});
            skLineSegment(sketch, "E4.15.0.7", {"start": v(84.87, -107.3) * mm, "end": v(84.87, -112.3) * mm});
            skLineSegment(sketch, "E4.15.0.8", {"start": v(15.07, -107.3) * mm, "end": v(15.07, -112.3) * mm});
            skLineSegment(sketch, "E4.15.0.9", {"start": v(98.47, -107.3) * mm, "end": v(103.47, -107.3) * mm});
            skLineSegment(sketch, "E4.15.0.10", {"start": v(166.47, -107.3) * mm, "end": v(166.47, -112.3) * mm});
            skLineSegment(sketch, "E4.15.0.11", {"start": v(91.67, -107.3) * mm, "end": v(96.67, -107.3) * mm});
            skLineSegment(sketch, "E4.15.0.12", {"start": v(71.27, -112.3) * mm, "end": v(76.27, -112.3) * mm});
            skLineSegment(sketch, "E4.15.0.13", {"start": v(132.47, -112.3) * mm, "end": v(137.47, -112.3) * mm});
            skLineSegment(sketch, "E4.15.0.14", {"start": v(146.07, -107.3) * mm, "end": v(146.07, -112.3) * mm});
            skLineSegment(sketch, "E4.15.0.15", {"start": v(105.27, -112.3) * mm, "end": v(110.27, -112.3) * mm});
            skLineSegment(sketch, "E4.15.0.16", {"start": v(191.87, -107.3) * mm, "end": v(191.87, -112.3) * mm});
            skLineSegment(sketch, "E4.15.0.17", {"start": v(159.67, -112.3) * mm, "end": v(164.67, -112.3) * mm});
            skLineSegment(sketch, "E4.15.0.18", {"start": v(76.27, -107.3) * mm, "end": v(76.27, -112.3) * mm});
            skLineSegment(sketch, "E4.15.0.19", {"start": v(23.67, -107.3) * mm, "end": v(23.67, -112.3) * mm});
            skLineSegment(sketch, "E4.15.0.20", {"start": v(146.07, -107.3) * mm, "end": v(151.07, -107.3) * mm});
            skLineSegment(sketch, "E4.15.0.21", {"start": v(139.27, -112.3) * mm, "end": v(144.27, -112.3) * mm});
            skLineSegment(sketch, "E4.15.0.22", {"start": v(185.07, -107.3) * mm, "end": v(185.07, -112.3) * mm});
            skLineSegment(sketch, "E4.15.0.23", {"start": v(55.87, -107.3) * mm, "end": v(55.87, -112.3) * mm});
            skLineSegment(sketch, "E4.15.0.24", {"start": v(171.47, -107.3) * mm, "end": v(171.47, -112.3) * mm});
            skLineSegment(sketch, "E4.15.0.25", {"start": v(62.67, -107.3) * mm, "end": v(62.67, -112.3) * mm});
            skLineSegment(sketch, "E4.15.0.26", {"start": v(69.47, -107.3) * mm, "end": v(69.47, -112.3) * mm});
            skLineSegment(sketch, "E4.15.0.27", {"start": v(132.47, -107.3) * mm, "end": v(137.47, -107.3) * mm});
            skLineSegment(sketch, "E4.15.0.28", {"start": v(64.47, -107.3) * mm, "end": v(64.47, -112.3) * mm});
            skLineSegment(sketch, "E4.15.0.29", {"start": v(152.87, -112.3) * mm, "end": v(157.87, -112.3) * mm});
            skLineSegment(sketch, "E4.15.0.30", {"start": v(180.07, -112.3) * mm, "end": v(185.07, -112.3) * mm});
            skLineSegment(sketch, "E4.15.0.31", {"start": v(37.27, -107.3) * mm, "end": v(37.27, -112.3) * mm});
            skLineSegment(sketch, "E4.15.0.32", {"start": v(173.27, -112.3) * mm, "end": v(178.27, -112.3) * mm});
            skLineSegment(sketch, "E4.15.0.33", {"start": v(91.67, -107.3) * mm, "end": v(91.67, -112.3) * mm});
            skLineSegment(sketch, "E4.15.0.34", {"start": v(78.07, -107.3) * mm, "end": v(83.07, -107.3) * mm});
            skLineSegment(sketch, "E4.15.0.35", {"start": v(71.27, -107.3) * mm, "end": v(71.27, -112.3) * mm});
            skLineSegment(sketch, "E4.15.0.36", {"start": v(57.67, -112.3) * mm, "end": v(62.67, -112.3) * mm});
            skLineSegment(sketch, "E4.15.0.37", {"start": v(112.07, -107.3) * mm, "end": v(112.07, -112.3) * mm});
            skLineSegment(sketch, "E4.15.0.38", {"start": v(151.07, -107.3) * mm, "end": v(151.07, -112.3) * mm});
            skLineSegment(sketch, "E4.15.0.39", {"start": v(178.27, -107.3) * mm, "end": v(178.27, -112.3) * mm});
            skLineSegment(sketch, "E4.15.0.40", {"start": v(180.07, -107.3) * mm, "end": v(180.07, -112.3) * mm});
            skLineSegment(sketch, "E4.15.0.41", {"start": v(98.47, -107.3) * mm, "end": v(98.47, -112.3) * mm});
            skLineSegment(sketch, "E4.15.0.42", {"start": v(37.27, -107.3) * mm, "end": v(42.27, -107.3) * mm});
            skLineSegment(sketch, "E4.15.0.43", {"start": v(118.87, -112.3) * mm, "end": v(123.87, -112.3) * mm});
            skLineSegment(sketch, "E4.15.0.44", {"start": v(8.27, -107.3) * mm, "end": v(8.27, -112.3) * mm});
            skLineSegment(sketch, "E4.15.0.45", {"start": v(44.07, -107.3) * mm, "end": v(44.07, -112.3) * mm});
            skLineSegment(sketch, "E4.15.0.46", {"start": v(78.07, -112.3) * mm, "end": v(83.07, -112.3) * mm});
            skLineSegment(sketch, "E4.15.0.47", {"start": v(139.27, -107.3) * mm, "end": v(144.27, -107.3) * mm});
            skLineSegment(sketch, "E4.15.0.48", {"start": v(23.67, -107.3) * mm, "end": v(28.67, -107.3) * mm});
            skLineSegment(sketch, "E4.15.0.49", {"start": v(152.87, -107.3) * mm, "end": v(152.87, -112.3) * mm});
            skLineSegment(sketch, "E4.15.0.50", {"start": v(57.67, -107.3) * mm, "end": v(62.67, -107.3) * mm});
            skLineSegment(sketch, "E4.15.0.51", {"start": v(44.07, -107.3) * mm, "end": v(49.07, -107.3) * mm});
            skLineSegment(sketch, "E4.15.0.52", {"start": v(42.27, -107.3) * mm, "end": v(42.27, -112.3) * mm});
            skLineSegment(sketch, "E4.15.0.53", {"start": v(125.67, -112.3) * mm, "end": v(130.67, -112.3) * mm});
            skLineSegment(sketch, "E4.15.0.54", {"start": v(186.87, -112.3) * mm, "end": v(191.87, -112.3) * mm});
            skLineSegment(sketch, "E4.15.0.55", {"start": v(125.67, -107.3) * mm, "end": v(125.67, -112.3) * mm});
            skLineSegment(sketch, "E4.15.0.56", {"start": v(64.47, -107.3) * mm, "end": v(69.47, -107.3) * mm});
            skLineSegment(sketch, "E4.15.0.57", {"start": v(64.47, -112.3) * mm, "end": v(69.47, -112.3) * mm});
            skLineSegment(sketch, "E4.15.0.58", {"start": v(164.67, -107.3) * mm, "end": v(164.67, -112.3) * mm});
            skLineSegment(sketch, "E4.15.0.59", {"start": v(186.87, -107.3) * mm, "end": v(186.87, -112.3) * mm});
            skLineSegment(sketch, "E4.15.0.60", {"start": v(10.07, -107.3) * mm, "end": v(10.07, -112.3) * mm});
            skLineSegment(sketch, "E4.15.0.61", {"start": v(84.87, -107.3) * mm, "end": v(89.87, -107.3) * mm});
            skLineSegment(sketch, "E4.15.0.62", {"start": v(10.07, -107.3) * mm, "end": v(15.07, -107.3) * mm});
            skLineSegment(sketch, "E4.15.0.63", {"start": v(50.87, -107.3) * mm, "end": v(55.87, -107.3) * mm});
            skLineSegment(sketch, "E4.15.0.64", {"start": v(110.27, -107.3) * mm, "end": v(110.27, -112.3) * mm});
            skLineSegment(sketch, "E4.15.0.65", {"start": v(91.67, -112.3) * mm, "end": v(96.67, -112.3) * mm});
            skLineSegment(sketch, "E4.15.0.66", {"start": v(103.47, -107.3) * mm, "end": v(103.47, -112.3) * mm});
            skLineSegment(sketch, "E4.15.0.67", {"start": v(3.27, -107.3) * mm, "end": v(8.27, -107.3) * mm});
            skLineSegment(sketch, "E4.15.0.68", {"start": v(98.47, -112.3) * mm, "end": v(103.47, -112.3) * mm});
            skLineSegment(sketch, "E4.15.0.69", {"start": v(123.87, -107.3) * mm, "end": v(123.87, -112.3) * mm});
            skLineSegment(sketch, "E4.15.0.70", {"start": v(84.87, -112.3) * mm, "end": v(89.87, -112.3) * mm});
            skLineSegment(sketch, "E4.15.0.71", {"start": v(16.87, -107.3) * mm, "end": v(21.87, -107.3) * mm});
            skLineSegment(sketch, "E4.15.0.72", {"start": v(30.47, -107.3) * mm, "end": v(35.47, -107.3) * mm});
            skLineSegment(sketch, "E4.15.0.73", {"start": v(78.07, -107.3) * mm, "end": v(78.07, -112.3) * mm});
            skLineSegment(sketch, "E4.15.0.74", {"start": v(3.27, -107.3) * mm, "end": v(3.27, -112.3) * mm});
            skLineSegment(sketch, "E4.15.0.75", {"start": v(30.47, -107.3) * mm, "end": v(30.47, -112.3) * mm});
            skLineSegment(sketch, "E4.15.0.76", {"start": v(159.67, -107.3) * mm, "end": v(159.67, -112.3) * mm});
            skLineSegment(sketch, "E4.15.0.77", {"start": v(105.27, -107.3) * mm, "end": v(110.27, -107.3) * mm});
            skLineSegment(sketch, "E4.15.0.78", {"start": v(83.07, -107.3) * mm, "end": v(83.07, -112.3) * mm});
            skLineSegment(sketch, "E4.15.0.79", {"start": v(35.47, -107.3) * mm, "end": v(35.47, -112.3) * mm});
            skLineSegment(sketch, "E4.15.0.80", {"start": v(157.87, -107.3) * mm, "end": v(157.87, -112.3) * mm});
            skLineSegment(sketch, "E4.15.0.81", {"start": v(21.87, -107.3) * mm, "end": v(21.87, -112.3) * mm});
            skLineSegment(sketch, "E4.15.0.82", {"start": v(144.27, -107.3) * mm, "end": v(144.27, -112.3) * mm});
            skLineSegment(sketch, "E4.15.0.83", {"start": v(139.27, -107.3) * mm, "end": v(139.27, -112.3) * mm});
            skLineSegment(sketch, "E4.15.0.84", {"start": v(130.67, -107.3) * mm, "end": v(130.67, -112.3) * mm});
            skLineSegment(sketch, "E4.15.0.85", {"start": v(57.67, -107.3) * mm, "end": v(57.67, -112.3) * mm});
            skLineSegment(sketch, "E4.15.0.86", {"start": v(137.47, -107.3) * mm, "end": v(137.47, -112.3) * mm});
            skLineSegment(sketch, "E4.15.0.87", {"start": v(118.87, -107.3) * mm, "end": v(118.87, -112.3) * mm});
            skLineSegment(sketch, "E4.15.0.88", {"start": v(96.67, -107.3) * mm, "end": v(96.67, -112.3) * mm});
            skLineSegment(sketch, "E4.15.0.89", {"start": v(146.07, -112.3) * mm, "end": v(151.07, -112.3) * mm});
            skLineSegment(sketch, "E4.15.0.90", {"start": v(166.47, -112.3) * mm, "end": v(171.47, -112.3) * mm});
            skLineSegment(sketch, "E4.15.0.91", {"start": v(50.87, -107.3) * mm, "end": v(50.87, -112.3) * mm});
            skLineSegment(sketch, "E4.15.0.92", {"start": v(118.87, -107.3) * mm, "end": v(123.87, -107.3) * mm});
            skLineSegment(sketch, "E4.15.0.93", {"start": v(132.47, -107.3) * mm, "end": v(132.47, -112.3) * mm});
            skLineSegment(sketch, "E4.15.0.94", {"start": v(16.87, -107.3) * mm, "end": v(16.87, -112.3) * mm});
            skLineSegment(sketch, "E4.15.0.95", {"start": v(105.27, -107.3) * mm, "end": v(105.27, -112.3) * mm});
            skLineSegment(sketch, "E4.15.0.96", {"start": v(112.07, -112.3) * mm, "end": v(117.07, -112.3) * mm});
            skLineSegment(sketch, "E4.15.0.97", {"start": v(89.87, -107.3) * mm, "end": v(89.87, -112.3) * mm});
            skLineSegment(sketch, "E4.15.0.98", {"start": v(152.87, -107.3) * mm, "end": v(157.87, -107.3) * mm});
            skLineSegment(sketch, "E4.15.0.99", {"start": v(186.87, -107.3) * mm, "end": v(191.87, -107.3) * mm});
            skLineSegment(sketch, "E4.15.0.100", {"start": v(37.27, -112.3) * mm, "end": v(42.27, -112.3) * mm});
            skLineSegment(sketch, "E4.15.0.101", {"start": v(44.07, -112.3) * mm, "end": v(49.07, -112.3) * mm});
            skLineSegment(sketch, "E4.15.0.102", {"start": v(3.27, -112.3) * mm, "end": v(10.07, -112.3) * mm, "construction": true});
            skLineSegment(sketch, "E4.15.0.103", {"start": v(159.67, -107.3) * mm, "end": v(164.67, -107.3) * mm});
            skLineSegment(sketch, "E4.15.0.104", {"start": v(166.47, -107.3) * mm, "end": v(171.47, -107.3) * mm});
            skLineSegment(sketch, "E4.15.0.105", {"start": v(173.27, -107.3) * mm, "end": v(178.27, -107.3) * mm});
            skLineSegment(sketch, "E4.15.0.106", {"start": v(16.87, -112.3) * mm, "end": v(21.87, -112.3) * mm});
            skLineSegment(sketch, "E4.15.0.107", {"start": v(30.47, -112.3) * mm, "end": v(35.47, -112.3) * mm});
            skLineSegment(sketch, "E4.15.0.108", {"start": v(23.67, -112.3) * mm, "end": v(28.67, -112.3) * mm});
            skLineSegment(sketch, "E4.15.0.109", {"start": v(10.07, -112.3) * mm, "end": v(15.07, -112.3) * mm});
            skLineSegment(sketch, "E4.15.0.110", {"start": v(50.87, -112.3) * mm, "end": v(55.87, -112.3) * mm});
            skLineSegment(sketch, "E4.15.0.111", {"start": v(180.07, -107.3) * mm, "end": v(185.07, -107.3) * mm});
            skLineSegment(sketch, "E4.15.0.112", {"start": v(3.27, -112.3) * mm, "end": v(8.27, -112.3) * mm});
            skLineSegment(sketch, "E4.16.0.0", {"start": v(112.12, -114.3) * mm, "end": v(117.12, -114.3) * mm});
            skLineSegment(sketch, "E4.16.0.1", {"start": v(117.12, -114.3) * mm, "end": v(117.12, -119.3) * mm});
            skLineSegment(sketch, "E4.16.0.2", {"start": v(125.72, -114.3) * mm, "end": v(130.72, -114.3) * mm});
            skLineSegment(sketch, "E4.16.0.3", {"start": v(28.72, -114.3) * mm, "end": v(28.72, -119.3) * mm});
            skLineSegment(sketch, "E4.16.0.4", {"start": v(71.32, -114.3) * mm, "end": v(76.32, -114.3) * mm});
            skLineSegment(sketch, "E4.16.0.5", {"start": v(173.32, -114.3) * mm, "end": v(173.32, -119.3) * mm});
            skLineSegment(sketch, "E4.16.0.6", {"start": v(49.12, -114.3) * mm, "end": v(49.12, -119.3) * mm});
            skLineSegment(sketch, "E4.16.0.7", {"start": v(84.92, -114.3) * mm, "end": v(84.92, -119.3) * mm});
            skLineSegment(sketch, "E4.16.0.8", {"start": v(15.12, -114.3) * mm, "end": v(15.12, -119.3) * mm});
            skLineSegment(sketch, "E4.16.0.9", {"start": v(98.52, -114.3) * mm, "end": v(103.52, -114.3) * mm});
            skLineSegment(sketch, "E4.16.0.10", {"start": v(166.52, -114.3) * mm, "end": v(166.52, -119.3) * mm});
            skLineSegment(sketch, "E4.16.0.11", {"start": v(91.72, -114.3) * mm, "end": v(96.72, -114.3) * mm});
            skLineSegment(sketch, "E4.16.0.12", {"start": v(71.32, -119.3) * mm, "end": v(76.32, -119.3) * mm});
            skLineSegment(sketch, "E4.16.0.13", {"start": v(132.52, -119.3) * mm, "end": v(137.52, -119.3) * mm});
            skLineSegment(sketch, "E4.16.0.14", {"start": v(146.12, -114.3) * mm, "end": v(146.12, -119.3) * mm});
            skLineSegment(sketch, "E4.16.0.15", {"start": v(105.32, -119.3) * mm, "end": v(110.32, -119.3) * mm});
            skLineSegment(sketch, "E4.16.0.16", {"start": v(191.92, -114.3) * mm, "end": v(191.92, -119.3) * mm});
            skLineSegment(sketch, "E4.16.0.17", {"start": v(159.72, -119.3) * mm, "end": v(164.72, -119.3) * mm});
            skLineSegment(sketch, "E4.16.0.18", {"start": v(76.32, -114.3) * mm, "end": v(76.32, -119.3) * mm});
            skLineSegment(sketch, "E4.16.0.19", {"start": v(23.72, -114.3) * mm, "end": v(23.72, -119.3) * mm});
            skLineSegment(sketch, "E4.16.0.20", {"start": v(146.12, -114.3) * mm, "end": v(151.12, -114.3) * mm});
            skLineSegment(sketch, "E4.16.0.21", {"start": v(139.32, -119.3) * mm, "end": v(144.32, -119.3) * mm});
            skLineSegment(sketch, "E4.16.0.22", {"start": v(185.12, -114.3) * mm, "end": v(185.12, -119.3) * mm});
            skLineSegment(sketch, "E4.16.0.23", {"start": v(55.92, -114.3) * mm, "end": v(55.92, -119.3) * mm});
            skLineSegment(sketch, "E4.16.0.24", {"start": v(171.52, -114.3) * mm, "end": v(171.52, -119.3) * mm});
            skLineSegment(sketch, "E4.16.0.25", {"start": v(62.72, -114.3) * mm, "end": v(62.72, -119.3) * mm});
            skLineSegment(sketch, "E4.16.0.26", {"start": v(69.52, -114.3) * mm, "end": v(69.52, -119.3) * mm});
            skLineSegment(sketch, "E4.16.0.27", {"start": v(132.52, -114.3) * mm, "end": v(137.52, -114.3) * mm});
            skLineSegment(sketch, "E4.16.0.28", {"start": v(64.52, -114.3) * mm, "end": v(64.52, -119.3) * mm});
            skLineSegment(sketch, "E4.16.0.29", {"start": v(152.92, -119.3) * mm, "end": v(157.92, -119.3) * mm});
            skLineSegment(sketch, "E4.16.0.30", {"start": v(180.12, -119.3) * mm, "end": v(185.12, -119.3) * mm});
            skLineSegment(sketch, "E4.16.0.31", {"start": v(37.32, -114.3) * mm, "end": v(37.32, -119.3) * mm});
            skLineSegment(sketch, "E4.16.0.32", {"start": v(173.32, -119.3) * mm, "end": v(178.32, -119.3) * mm});
            skLineSegment(sketch, "E4.16.0.33", {"start": v(91.72, -114.3) * mm, "end": v(91.72, -119.3) * mm});
            skLineSegment(sketch, "E4.16.0.34", {"start": v(78.12, -114.3) * mm, "end": v(83.12, -114.3) * mm});
            skLineSegment(sketch, "E4.16.0.35", {"start": v(71.32, -114.3) * mm, "end": v(71.32, -119.3) * mm});
            skLineSegment(sketch, "E4.16.0.36", {"start": v(57.72, -119.3) * mm, "end": v(62.72, -119.3) * mm});
            skLineSegment(sketch, "E4.16.0.37", {"start": v(112.12, -114.3) * mm, "end": v(112.12, -119.3) * mm});
            skLineSegment(sketch, "E4.16.0.38", {"start": v(151.12, -114.3) * mm, "end": v(151.12, -119.3) * mm});
            skLineSegment(sketch, "E4.16.0.39", {"start": v(178.32, -114.3) * mm, "end": v(178.32, -119.3) * mm});
            skLineSegment(sketch, "E4.16.0.40", {"start": v(180.12, -114.3) * mm, "end": v(180.12, -119.3) * mm});
            skLineSegment(sketch, "E4.16.0.41", {"start": v(98.52, -114.3) * mm, "end": v(98.52, -119.3) * mm});
            skLineSegment(sketch, "E4.16.0.42", {"start": v(37.32, -114.3) * mm, "end": v(42.32, -114.3) * mm});
            skLineSegment(sketch, "E4.16.0.43", {"start": v(118.92, -119.3) * mm, "end": v(123.92, -119.3) * mm});
            skLineSegment(sketch, "E4.16.0.44", {"start": v(8.32, -114.3) * mm, "end": v(8.32, -119.3) * mm});
            skLineSegment(sketch, "E4.16.0.45", {"start": v(44.12, -114.3) * mm, "end": v(44.12, -119.3) * mm});
            skLineSegment(sketch, "E4.16.0.46", {"start": v(78.12, -119.3) * mm, "end": v(83.12, -119.3) * mm});
            skLineSegment(sketch, "E4.16.0.47", {"start": v(139.32, -114.3) * mm, "end": v(144.32, -114.3) * mm});
            skLineSegment(sketch, "E4.16.0.48", {"start": v(23.72, -114.3) * mm, "end": v(28.72, -114.3) * mm});
            skLineSegment(sketch, "E4.16.0.49", {"start": v(152.92, -114.3) * mm, "end": v(152.92, -119.3) * mm});
            skLineSegment(sketch, "E4.16.0.50", {"start": v(57.72, -114.3) * mm, "end": v(62.72, -114.3) * mm});
            skLineSegment(sketch, "E4.16.0.51", {"start": v(44.12, -114.3) * mm, "end": v(49.12, -114.3) * mm});
            skLineSegment(sketch, "E4.16.0.52", {"start": v(42.32, -114.3) * mm, "end": v(42.32, -119.3) * mm});
            skLineSegment(sketch, "E4.16.0.53", {"start": v(125.72, -119.3) * mm, "end": v(130.72, -119.3) * mm});
            skLineSegment(sketch, "E4.16.0.54", {"start": v(186.92, -119.3) * mm, "end": v(191.92, -119.3) * mm});
            skLineSegment(sketch, "E4.16.0.55", {"start": v(125.72, -114.3) * mm, "end": v(125.72, -119.3) * mm});
            skLineSegment(sketch, "E4.16.0.56", {"start": v(64.52, -114.3) * mm, "end": v(69.52, -114.3) * mm});
            skLineSegment(sketch, "E4.16.0.57", {"start": v(64.52, -119.3) * mm, "end": v(69.52, -119.3) * mm});
            skLineSegment(sketch, "E4.16.0.58", {"start": v(164.72, -114.3) * mm, "end": v(164.72, -119.3) * mm});
            skLineSegment(sketch, "E4.16.0.59", {"start": v(186.92, -114.3) * mm, "end": v(186.92, -119.3) * mm});
            skLineSegment(sketch, "E4.16.0.60", {"start": v(10.12, -114.3) * mm, "end": v(10.12, -119.3) * mm});
            skLineSegment(sketch, "E4.16.0.61", {"start": v(84.92, -114.3) * mm, "end": v(89.92, -114.3) * mm});
            skLineSegment(sketch, "E4.16.0.62", {"start": v(10.12, -114.3) * mm, "end": v(15.12, -114.3) * mm});
            skLineSegment(sketch, "E4.16.0.63", {"start": v(50.92, -114.3) * mm, "end": v(55.92, -114.3) * mm});
            skLineSegment(sketch, "E4.16.0.64", {"start": v(110.32, -114.3) * mm, "end": v(110.32, -119.3) * mm});
            skLineSegment(sketch, "E4.16.0.65", {"start": v(91.72, -119.3) * mm, "end": v(96.72, -119.3) * mm});
            skLineSegment(sketch, "E4.16.0.66", {"start": v(103.52, -114.3) * mm, "end": v(103.52, -119.3) * mm});
            skLineSegment(sketch, "E4.16.0.67", {"start": v(3.32, -114.3) * mm, "end": v(8.32, -114.3) * mm});
            skLineSegment(sketch, "E4.16.0.68", {"start": v(98.52, -119.3) * mm, "end": v(103.52, -119.3) * mm});
            skLineSegment(sketch, "E4.16.0.69", {"start": v(123.92, -114.3) * mm, "end": v(123.92, -119.3) * mm});
            skLineSegment(sketch, "E4.16.0.70", {"start": v(84.92, -119.3) * mm, "end": v(89.92, -119.3) * mm});
            skLineSegment(sketch, "E4.16.0.71", {"start": v(16.92, -114.3) * mm, "end": v(21.92, -114.3) * mm});
            skLineSegment(sketch, "E4.16.0.72", {"start": v(30.52, -114.3) * mm, "end": v(35.52, -114.3) * mm});
            skLineSegment(sketch, "E4.16.0.73", {"start": v(78.12, -114.3) * mm, "end": v(78.12, -119.3) * mm});
            skLineSegment(sketch, "E4.16.0.74", {"start": v(3.32, -114.3) * mm, "end": v(3.32, -119.3) * mm});
            skLineSegment(sketch, "E4.16.0.75", {"start": v(30.52, -114.3) * mm, "end": v(30.52, -119.3) * mm});
            skLineSegment(sketch, "E4.16.0.76", {"start": v(159.72, -114.3) * mm, "end": v(159.72, -119.3) * mm});
            skLineSegment(sketch, "E4.16.0.77", {"start": v(105.32, -114.3) * mm, "end": v(110.32, -114.3) * mm});
            skLineSegment(sketch, "E4.16.0.78", {"start": v(83.12, -114.3) * mm, "end": v(83.12, -119.3) * mm});
            skLineSegment(sketch, "E4.16.0.79", {"start": v(35.52, -114.3) * mm, "end": v(35.52, -119.3) * mm});
            skLineSegment(sketch, "E4.16.0.80", {"start": v(157.92, -114.3) * mm, "end": v(157.92, -119.3) * mm});
            skLineSegment(sketch, "E4.16.0.81", {"start": v(21.92, -114.3) * mm, "end": v(21.92, -119.3) * mm});
            skLineSegment(sketch, "E4.16.0.82", {"start": v(144.32, -114.3) * mm, "end": v(144.32, -119.3) * mm});
            skLineSegment(sketch, "E4.16.0.83", {"start": v(139.32, -114.3) * mm, "end": v(139.32, -119.3) * mm});
            skLineSegment(sketch, "E4.16.0.84", {"start": v(130.72, -114.3) * mm, "end": v(130.72, -119.3) * mm});
            skLineSegment(sketch, "E4.16.0.85", {"start": v(57.72, -114.3) * mm, "end": v(57.72, -119.3) * mm});
            skLineSegment(sketch, "E4.16.0.86", {"start": v(137.52, -114.3) * mm, "end": v(137.52, -119.3) * mm});
            skLineSegment(sketch, "E4.16.0.87", {"start": v(118.92, -114.3) * mm, "end": v(118.92, -119.3) * mm});
            skLineSegment(sketch, "E4.16.0.88", {"start": v(96.72, -114.3) * mm, "end": v(96.72, -119.3) * mm});
            skLineSegment(sketch, "E4.16.0.89", {"start": v(146.12, -119.3) * mm, "end": v(151.12, -119.3) * mm});
            skLineSegment(sketch, "E4.16.0.90", {"start": v(166.52, -119.3) * mm, "end": v(171.52, -119.3) * mm});
            skLineSegment(sketch, "E4.16.0.91", {"start": v(50.92, -114.3) * mm, "end": v(50.92, -119.3) * mm});
            skLineSegment(sketch, "E4.16.0.92", {"start": v(118.92, -114.3) * mm, "end": v(123.92, -114.3) * mm});
            skLineSegment(sketch, "E4.16.0.93", {"start": v(132.52, -114.3) * mm, "end": v(132.52, -119.3) * mm});
            skLineSegment(sketch, "E4.16.0.94", {"start": v(16.92, -114.3) * mm, "end": v(16.92, -119.3) * mm});
            skLineSegment(sketch, "E4.16.0.95", {"start": v(105.32, -114.3) * mm, "end": v(105.32, -119.3) * mm});
            skLineSegment(sketch, "E4.16.0.96", {"start": v(112.12, -119.3) * mm, "end": v(117.12, -119.3) * mm});
            skLineSegment(sketch, "E4.16.0.97", {"start": v(89.92, -114.3) * mm, "end": v(89.92, -119.3) * mm});
            skLineSegment(sketch, "E4.16.0.98", {"start": v(152.92, -114.3) * mm, "end": v(157.92, -114.3) * mm});
            skLineSegment(sketch, "E4.16.0.99", {"start": v(186.92, -114.3) * mm, "end": v(191.92, -114.3) * mm});
            skLineSegment(sketch, "E4.16.0.100", {"start": v(37.32, -119.3) * mm, "end": v(42.32, -119.3) * mm});
            skLineSegment(sketch, "E4.16.0.101", {"start": v(44.12, -119.3) * mm, "end": v(49.12, -119.3) * mm});
            skLineSegment(sketch, "E4.16.0.102", {"start": v(3.32, -119.3) * mm, "end": v(10.12, -119.3) * mm, "construction": true});
            skLineSegment(sketch, "E4.16.0.103", {"start": v(159.72, -114.3) * mm, "end": v(164.72, -114.3) * mm});
            skLineSegment(sketch, "E4.16.0.104", {"start": v(166.52, -114.3) * mm, "end": v(171.52, -114.3) * mm});
            skLineSegment(sketch, "E4.16.0.105", {"start": v(173.32, -114.3) * mm, "end": v(178.32, -114.3) * mm});
            skLineSegment(sketch, "E4.16.0.106", {"start": v(16.92, -119.3) * mm, "end": v(21.92, -119.3) * mm});
            skLineSegment(sketch, "E4.16.0.107", {"start": v(30.52, -119.3) * mm, "end": v(35.52, -119.3) * mm});
            skLineSegment(sketch, "E4.16.0.108", {"start": v(23.72, -119.3) * mm, "end": v(28.72, -119.3) * mm});
            skLineSegment(sketch, "E4.16.0.109", {"start": v(10.12, -119.3) * mm, "end": v(15.12, -119.3) * mm});
            skLineSegment(sketch, "E4.16.0.110", {"start": v(50.92, -119.3) * mm, "end": v(55.92, -119.3) * mm});
            skLineSegment(sketch, "E4.16.0.111", {"start": v(180.12, -114.3) * mm, "end": v(185.12, -114.3) * mm});
            skLineSegment(sketch, "E4.16.0.112", {"start": v(3.32, -119.3) * mm, "end": v(8.32, -119.3) * mm});
            skLineSegment(sketch, "E4.17.0.0", {"start": v(112.17, -121.3) * mm, "end": v(117.17, -121.3) * mm});
            skLineSegment(sketch, "E4.17.0.1", {"start": v(117.17, -121.3) * mm, "end": v(117.17, -126.3) * mm});
            skLineSegment(sketch, "E4.17.0.2", {"start": v(125.77, -121.3) * mm, "end": v(130.77, -121.3) * mm});
            skLineSegment(sketch, "E4.17.0.3", {"start": v(28.77, -121.3) * mm, "end": v(28.77, -126.3) * mm});
            skLineSegment(sketch, "E4.17.0.4", {"start": v(71.37, -121.3) * mm, "end": v(76.37, -121.3) * mm});
            skLineSegment(sketch, "E4.17.0.5", {"start": v(173.37, -121.3) * mm, "end": v(173.37, -126.3) * mm});
            skLineSegment(sketch, "E4.17.0.6", {"start": v(49.17, -121.3) * mm, "end": v(49.17, -126.3) * mm});
            skLineSegment(sketch, "E4.17.0.7", {"start": v(84.97, -121.3) * mm, "end": v(84.97, -126.3) * mm});
            skLineSegment(sketch, "E4.17.0.8", {"start": v(15.17, -121.3) * mm, "end": v(15.17, -126.3) * mm});
            skLineSegment(sketch, "E4.17.0.9", {"start": v(98.57, -121.3) * mm, "end": v(103.57, -121.3) * mm});
            skLineSegment(sketch, "E4.17.0.10", {"start": v(166.57, -121.3) * mm, "end": v(166.57, -126.3) * mm});
            skLineSegment(sketch, "E4.17.0.11", {"start": v(91.77, -121.3) * mm, "end": v(96.77, -121.3) * mm});
            skLineSegment(sketch, "E4.17.0.12", {"start": v(71.37, -126.3) * mm, "end": v(76.37, -126.3) * mm});
            skLineSegment(sketch, "E4.17.0.13", {"start": v(132.57, -126.3) * mm, "end": v(137.57, -126.3) * mm});
            skLineSegment(sketch, "E4.17.0.14", {"start": v(146.17, -121.3) * mm, "end": v(146.17, -126.3) * mm});
            skLineSegment(sketch, "E4.17.0.15", {"start": v(105.37, -126.3) * mm, "end": v(110.37, -126.3) * mm});
            skLineSegment(sketch, "E4.17.0.16", {"start": v(191.97, -121.3) * mm, "end": v(191.97, -126.3) * mm});
            skLineSegment(sketch, "E4.17.0.17", {"start": v(159.77, -126.3) * mm, "end": v(164.77, -126.3) * mm});
            skLineSegment(sketch, "E4.17.0.18", {"start": v(76.37, -121.3) * mm, "end": v(76.37, -126.3) * mm});
            skLineSegment(sketch, "E4.17.0.19", {"start": v(23.77, -121.3) * mm, "end": v(23.77, -126.3) * mm});
            skLineSegment(sketch, "E4.17.0.20", {"start": v(146.17, -121.3) * mm, "end": v(151.17, -121.3) * mm});
            skLineSegment(sketch, "E4.17.0.21", {"start": v(139.37, -126.3) * mm, "end": v(144.37, -126.3) * mm});
            skLineSegment(sketch, "E4.17.0.22", {"start": v(185.17, -121.3) * mm, "end": v(185.17, -126.3) * mm});
            skLineSegment(sketch, "E4.17.0.23", {"start": v(55.97, -121.3) * mm, "end": v(55.97, -126.3) * mm});
            skLineSegment(sketch, "E4.17.0.24", {"start": v(171.57, -121.3) * mm, "end": v(171.57, -126.3) * mm});
            skLineSegment(sketch, "E4.17.0.25", {"start": v(62.77, -121.3) * mm, "end": v(62.77, -126.3) * mm});
            skLineSegment(sketch, "E4.17.0.26", {"start": v(69.57, -121.3) * mm, "end": v(69.57, -126.3) * mm});
            skLineSegment(sketch, "E4.17.0.27", {"start": v(132.57, -121.3) * mm, "end": v(137.57, -121.3) * mm});
            skLineSegment(sketch, "E4.17.0.28", {"start": v(64.57, -121.3) * mm, "end": v(64.57, -126.3) * mm});
            skLineSegment(sketch, "E4.17.0.29", {"start": v(152.97, -126.3) * mm, "end": v(157.97, -126.3) * mm});
            skLineSegment(sketch, "E4.17.0.30", {"start": v(180.17, -126.3) * mm, "end": v(185.17, -126.3) * mm});
            skLineSegment(sketch, "E4.17.0.31", {"start": v(37.37, -121.3) * mm, "end": v(37.37, -126.3) * mm});
            skLineSegment(sketch, "E4.17.0.32", {"start": v(173.37, -126.3) * mm, "end": v(178.37, -126.3) * mm});
            skLineSegment(sketch, "E4.17.0.33", {"start": v(91.77, -121.3) * mm, "end": v(91.77, -126.3) * mm});
            skLineSegment(sketch, "E4.17.0.34", {"start": v(78.17, -121.3) * mm, "end": v(83.17, -121.3) * mm});
            skLineSegment(sketch, "E4.17.0.35", {"start": v(71.37, -121.3) * mm, "end": v(71.37, -126.3) * mm});
            skLineSegment(sketch, "E4.17.0.36", {"start": v(57.77, -126.3) * mm, "end": v(62.77, -126.3) * mm});
            skLineSegment(sketch, "E4.17.0.37", {"start": v(112.17, -121.3) * mm, "end": v(112.17, -126.3) * mm});
            skLineSegment(sketch, "E4.17.0.38", {"start": v(151.17, -121.3) * mm, "end": v(151.17, -126.3) * mm});
            skLineSegment(sketch, "E4.17.0.39", {"start": v(178.37, -121.3) * mm, "end": v(178.37, -126.3) * mm});
            skLineSegment(sketch, "E4.17.0.40", {"start": v(180.17, -121.3) * mm, "end": v(180.17, -126.3) * mm});
            skLineSegment(sketch, "E4.17.0.41", {"start": v(98.57, -121.3) * mm, "end": v(98.57, -126.3) * mm});
            skLineSegment(sketch, "E4.17.0.42", {"start": v(37.37, -121.3) * mm, "end": v(42.37, -121.3) * mm});
            skLineSegment(sketch, "E4.17.0.43", {"start": v(118.97, -126.3) * mm, "end": v(123.97, -126.3) * mm});
            skLineSegment(sketch, "E4.17.0.44", {"start": v(8.37, -121.3) * mm, "end": v(8.37, -126.3) * mm});
            skLineSegment(sketch, "E4.17.0.45", {"start": v(44.17, -121.3) * mm, "end": v(44.17, -126.3) * mm});
            skLineSegment(sketch, "E4.17.0.46", {"start": v(78.17, -126.3) * mm, "end": v(83.17, -126.3) * mm});
            skLineSegment(sketch, "E4.17.0.47", {"start": v(139.37, -121.3) * mm, "end": v(144.37, -121.3) * mm});
            skLineSegment(sketch, "E4.17.0.48", {"start": v(23.77, -121.3) * mm, "end": v(28.77, -121.3) * mm});
            skLineSegment(sketch, "E4.17.0.49", {"start": v(152.97, -121.3) * mm, "end": v(152.97, -126.3) * mm});
            skLineSegment(sketch, "E4.17.0.50", {"start": v(57.77, -121.3) * mm, "end": v(62.77, -121.3) * mm});
            skLineSegment(sketch, "E4.17.0.51", {"start": v(44.17, -121.3) * mm, "end": v(49.17, -121.3) * mm});
            skLineSegment(sketch, "E4.17.0.52", {"start": v(42.37, -121.3) * mm, "end": v(42.37, -126.3) * mm});
            skLineSegment(sketch, "E4.17.0.53", {"start": v(125.77, -126.3) * mm, "end": v(130.77, -126.3) * mm});
            skLineSegment(sketch, "E4.17.0.54", {"start": v(186.97, -126.3) * mm, "end": v(191.97, -126.3) * mm});
            skLineSegment(sketch, "E4.17.0.55", {"start": v(125.77, -121.3) * mm, "end": v(125.77, -126.3) * mm});
            skLineSegment(sketch, "E4.17.0.56", {"start": v(64.57, -121.3) * mm, "end": v(69.57, -121.3) * mm});
            skLineSegment(sketch, "E4.17.0.57", {"start": v(64.57, -126.3) * mm, "end": v(69.57, -126.3) * mm});
            skLineSegment(sketch, "E4.17.0.58", {"start": v(164.77, -121.3) * mm, "end": v(164.77, -126.3) * mm});
            skLineSegment(sketch, "E4.17.0.59", {"start": v(186.97, -121.3) * mm, "end": v(186.97, -126.3) * mm});
            skLineSegment(sketch, "E4.17.0.60", {"start": v(10.17, -121.3) * mm, "end": v(10.17, -126.3) * mm});
            skLineSegment(sketch, "E4.17.0.61", {"start": v(84.97, -121.3) * mm, "end": v(89.97, -121.3) * mm});
            skLineSegment(sketch, "E4.17.0.62", {"start": v(10.17, -121.3) * mm, "end": v(15.17, -121.3) * mm});
            skLineSegment(sketch, "E4.17.0.63", {"start": v(50.97, -121.3) * mm, "end": v(55.97, -121.3) * mm});
            skLineSegment(sketch, "E4.17.0.64", {"start": v(110.37, -121.3) * mm, "end": v(110.37, -126.3) * mm});
            skLineSegment(sketch, "E4.17.0.65", {"start": v(91.77, -126.3) * mm, "end": v(96.77, -126.3) * mm});
            skLineSegment(sketch, "E4.17.0.66", {"start": v(103.57, -121.3) * mm, "end": v(103.57, -126.3) * mm});
            skLineSegment(sketch, "E4.17.0.67", {"start": v(3.37, -121.3) * mm, "end": v(8.37, -121.3) * mm});
            skLineSegment(sketch, "E4.17.0.68", {"start": v(98.57, -126.3) * mm, "end": v(103.57, -126.3) * mm});
            skLineSegment(sketch, "E4.17.0.69", {"start": v(123.97, -121.3) * mm, "end": v(123.97, -126.3) * mm});
            skLineSegment(sketch, "E4.17.0.70", {"start": v(84.97, -126.3) * mm, "end": v(89.97, -126.3) * mm});
            skLineSegment(sketch, "E4.17.0.71", {"start": v(16.97, -121.3) * mm, "end": v(21.97, -121.3) * mm});
            skLineSegment(sketch, "E4.17.0.72", {"start": v(30.57, -121.3) * mm, "end": v(35.57, -121.3) * mm});
            skLineSegment(sketch, "E4.17.0.73", {"start": v(78.17, -121.3) * mm, "end": v(78.17, -126.3) * mm});
            skLineSegment(sketch, "E4.17.0.74", {"start": v(3.37, -121.3) * mm, "end": v(3.37, -126.3) * mm});
            skLineSegment(sketch, "E4.17.0.75", {"start": v(30.57, -121.3) * mm, "end": v(30.57, -126.3) * mm});
            skLineSegment(sketch, "E4.17.0.76", {"start": v(159.77, -121.3) * mm, "end": v(159.77, -126.3) * mm});
            skLineSegment(sketch, "E4.17.0.77", {"start": v(105.37, -121.3) * mm, "end": v(110.37, -121.3) * mm});
            skLineSegment(sketch, "E4.17.0.78", {"start": v(83.17, -121.3) * mm, "end": v(83.17, -126.3) * mm});
            skLineSegment(sketch, "E4.17.0.79", {"start": v(35.57, -121.3) * mm, "end": v(35.57, -126.3) * mm});
            skLineSegment(sketch, "E4.17.0.80", {"start": v(157.97, -121.3) * mm, "end": v(157.97, -126.3) * mm});
            skLineSegment(sketch, "E4.17.0.81", {"start": v(21.97, -121.3) * mm, "end": v(21.97, -126.3) * mm});
            skLineSegment(sketch, "E4.17.0.82", {"start": v(144.37, -121.3) * mm, "end": v(144.37, -126.3) * mm});
            skLineSegment(sketch, "E4.17.0.83", {"start": v(139.37, -121.3) * mm, "end": v(139.37, -126.3) * mm});
            skLineSegment(sketch, "E4.17.0.84", {"start": v(130.77, -121.3) * mm, "end": v(130.77, -126.3) * mm});
            skLineSegment(sketch, "E4.17.0.85", {"start": v(57.77, -121.3) * mm, "end": v(57.77, -126.3) * mm});
            skLineSegment(sketch, "E4.17.0.86", {"start": v(137.57, -121.3) * mm, "end": v(137.57, -126.3) * mm});
            skLineSegment(sketch, "E4.17.0.87", {"start": v(118.97, -121.3) * mm, "end": v(118.97, -126.3) * mm});
            skLineSegment(sketch, "E4.17.0.88", {"start": v(96.77, -121.3) * mm, "end": v(96.77, -126.3) * mm});
            skLineSegment(sketch, "E4.17.0.89", {"start": v(146.17, -126.3) * mm, "end": v(151.17, -126.3) * mm});
            skLineSegment(sketch, "E4.17.0.90", {"start": v(166.57, -126.3) * mm, "end": v(171.57, -126.3) * mm});
            skLineSegment(sketch, "E4.17.0.91", {"start": v(50.97, -121.3) * mm, "end": v(50.97, -126.3) * mm});
            skLineSegment(sketch, "E4.17.0.92", {"start": v(118.97, -121.3) * mm, "end": v(123.97, -121.3) * mm});
            skLineSegment(sketch, "E4.17.0.93", {"start": v(132.57, -121.3) * mm, "end": v(132.57, -126.3) * mm});
            skLineSegment(sketch, "E4.17.0.94", {"start": v(16.97, -121.3) * mm, "end": v(16.97, -126.3) * mm});
            skLineSegment(sketch, "E4.17.0.95", {"start": v(105.37, -121.3) * mm, "end": v(105.37, -126.3) * mm});
            skLineSegment(sketch, "E4.17.0.96", {"start": v(112.17, -126.3) * mm, "end": v(117.17, -126.3) * mm});
            skLineSegment(sketch, "E4.17.0.97", {"start": v(89.97, -121.3) * mm, "end": v(89.97, -126.3) * mm});
            skLineSegment(sketch, "E4.17.0.98", {"start": v(152.97, -121.3) * mm, "end": v(157.97, -121.3) * mm});
            skLineSegment(sketch, "E4.17.0.99", {"start": v(186.97, -121.3) * mm, "end": v(191.97, -121.3) * mm});
            skLineSegment(sketch, "E4.17.0.100", {"start": v(37.37, -126.3) * mm, "end": v(42.37, -126.3) * mm});
            skLineSegment(sketch, "E4.17.0.101", {"start": v(44.17, -126.3) * mm, "end": v(49.17, -126.3) * mm});
            skLineSegment(sketch, "E4.17.0.102", {"start": v(3.37, -126.3) * mm, "end": v(10.17, -126.3) * mm, "construction": true});
            skLineSegment(sketch, "E4.17.0.103", {"start": v(159.77, -121.3) * mm, "end": v(164.77, -121.3) * mm});
            skLineSegment(sketch, "E4.17.0.104", {"start": v(166.57, -121.3) * mm, "end": v(171.57, -121.3) * mm});
            skLineSegment(sketch, "E4.17.0.105", {"start": v(173.37, -121.3) * mm, "end": v(178.37, -121.3) * mm});
            skLineSegment(sketch, "E4.17.0.106", {"start": v(16.97, -126.3) * mm, "end": v(21.97, -126.3) * mm});
            skLineSegment(sketch, "E4.17.0.107", {"start": v(30.57, -126.3) * mm, "end": v(35.57, -126.3) * mm});
            skLineSegment(sketch, "E4.17.0.108", {"start": v(23.77, -126.3) * mm, "end": v(28.77, -126.3) * mm});
            skLineSegment(sketch, "E4.17.0.109", {"start": v(10.17, -126.3) * mm, "end": v(15.17, -126.3) * mm});
            skLineSegment(sketch, "E4.17.0.110", {"start": v(50.97, -126.3) * mm, "end": v(55.97, -126.3) * mm});
            skLineSegment(sketch, "E4.17.0.111", {"start": v(180.17, -121.3) * mm, "end": v(185.17, -121.3) * mm});
            skLineSegment(sketch, "E4.17.0.112", {"start": v(3.37, -126.3) * mm, "end": v(8.37, -126.3) * mm});
            skLineSegment(sketch, "E4.18.0.0", {"start": v(112.21, -128.3) * mm, "end": v(117.21, -128.3) * mm});
            skLineSegment(sketch, "E4.18.0.1", {"start": v(117.21, -128.3) * mm, "end": v(117.21, -133.3) * mm});
            skLineSegment(sketch, "E4.18.0.2", {"start": v(125.81, -128.3) * mm, "end": v(130.81, -128.3) * mm});
            skLineSegment(sketch, "E4.18.0.3", {"start": v(28.81, -128.3) * mm, "end": v(28.81, -133.3) * mm});
            skLineSegment(sketch, "E4.18.0.4", {"start": v(71.41, -128.3) * mm, "end": v(76.41, -128.3) * mm});
            skLineSegment(sketch, "E4.18.0.5", {"start": v(173.41, -128.3) * mm, "end": v(173.41, -133.3) * mm});
            skLineSegment(sketch, "E4.18.0.6", {"start": v(49.21, -128.3) * mm, "end": v(49.21, -133.3) * mm});
            skLineSegment(sketch, "E4.18.0.7", {"start": v(85.01, -128.3) * mm, "end": v(85.01, -133.3) * mm});
            skLineSegment(sketch, "E4.18.0.8", {"start": v(15.21, -128.3) * mm, "end": v(15.21, -133.3) * mm});
            skLineSegment(sketch, "E4.18.0.9", {"start": v(98.61, -128.3) * mm, "end": v(103.61, -128.3) * mm});
            skLineSegment(sketch, "E4.18.0.10", {"start": v(166.61, -128.3) * mm, "end": v(166.61, -133.3) * mm});
            skLineSegment(sketch, "E4.18.0.11", {"start": v(91.81, -128.3) * mm, "end": v(96.81, -128.3) * mm});
            skLineSegment(sketch, "E4.18.0.12", {"start": v(71.41, -133.3) * mm, "end": v(76.41, -133.3) * mm});
            skLineSegment(sketch, "E4.18.0.13", {"start": v(132.61, -133.3) * mm, "end": v(137.61, -133.3) * mm});
            skLineSegment(sketch, "E4.18.0.14", {"start": v(146.21, -128.3) * mm, "end": v(146.21, -133.3) * mm});
            skLineSegment(sketch, "E4.18.0.15", {"start": v(105.41, -133.3) * mm, "end": v(110.41, -133.3) * mm});
            skLineSegment(sketch, "E4.18.0.16", {"start": v(192.01, -128.3) * mm, "end": v(192.01, -133.3) * mm});
            skLineSegment(sketch, "E4.18.0.17", {"start": v(159.81, -133.3) * mm, "end": v(164.81, -133.3) * mm});
            skLineSegment(sketch, "E4.18.0.18", {"start": v(76.41, -128.3) * mm, "end": v(76.41, -133.3) * mm});
            skLineSegment(sketch, "E4.18.0.19", {"start": v(23.81, -128.3) * mm, "end": v(23.81, -133.3) * mm});
            skLineSegment(sketch, "E4.18.0.20", {"start": v(146.21, -128.3) * mm, "end": v(151.21, -128.3) * mm});
            skLineSegment(sketch, "E4.18.0.21", {"start": v(139.41, -133.3) * mm, "end": v(144.41, -133.3) * mm});
            skLineSegment(sketch, "E4.18.0.22", {"start": v(185.21, -128.3) * mm, "end": v(185.21, -133.3) * mm});
            skLineSegment(sketch, "E4.18.0.23", {"start": v(56.01, -128.3) * mm, "end": v(56.01, -133.3) * mm});
            skLineSegment(sketch, "E4.18.0.24", {"start": v(171.61, -128.3) * mm, "end": v(171.61, -133.3) * mm});
            skLineSegment(sketch, "E4.18.0.25", {"start": v(62.81, -128.3) * mm, "end": v(62.81, -133.3) * mm});
            skLineSegment(sketch, "E4.18.0.26", {"start": v(69.61, -128.3) * mm, "end": v(69.61, -133.3) * mm});
            skLineSegment(sketch, "E4.18.0.27", {"start": v(132.61, -128.3) * mm, "end": v(137.61, -128.3) * mm});
            skLineSegment(sketch, "E4.18.0.28", {"start": v(64.61, -128.3) * mm, "end": v(64.61, -133.3) * mm});
            skLineSegment(sketch, "E4.18.0.29", {"start": v(153.01, -133.3) * mm, "end": v(158.01, -133.3) * mm});
            skLineSegment(sketch, "E4.18.0.30", {"start": v(180.21, -133.3) * mm, "end": v(185.21, -133.3) * mm});
            skLineSegment(sketch, "E4.18.0.31", {"start": v(37.41, -128.3) * mm, "end": v(37.41, -133.3) * mm});
            skLineSegment(sketch, "E4.18.0.32", {"start": v(173.41, -133.3) * mm, "end": v(178.41, -133.3) * mm});
            skLineSegment(sketch, "E4.18.0.33", {"start": v(91.81, -128.3) * mm, "end": v(91.81, -133.3) * mm});
            skLineSegment(sketch, "E4.18.0.34", {"start": v(78.21, -128.3) * mm, "end": v(83.21, -128.3) * mm});
            skLineSegment(sketch, "E4.18.0.35", {"start": v(71.41, -128.3) * mm, "end": v(71.41, -133.3) * mm});
            skLineSegment(sketch, "E4.18.0.36", {"start": v(57.81, -133.3) * mm, "end": v(62.81, -133.3) * mm});
            skLineSegment(sketch, "E4.18.0.37", {"start": v(112.21, -128.3) * mm, "end": v(112.21, -133.3) * mm});
            skLineSegment(sketch, "E4.18.0.38", {"start": v(151.21, -128.3) * mm, "end": v(151.21, -133.3) * mm});
            skLineSegment(sketch, "E4.18.0.39", {"start": v(178.41, -128.3) * mm, "end": v(178.41, -133.3) * mm});
            skLineSegment(sketch, "E4.18.0.40", {"start": v(180.21, -128.3) * mm, "end": v(180.21, -133.3) * mm});
            skLineSegment(sketch, "E4.18.0.41", {"start": v(98.61, -128.3) * mm, "end": v(98.61, -133.3) * mm});
            skLineSegment(sketch, "E4.18.0.42", {"start": v(37.41, -128.3) * mm, "end": v(42.41, -128.3) * mm});
            skLineSegment(sketch, "E4.18.0.43", {"start": v(119.01, -133.3) * mm, "end": v(124.01, -133.3) * mm});
            skLineSegment(sketch, "E4.18.0.44", {"start": v(8.41, -128.3) * mm, "end": v(8.41, -133.3) * mm});
            skLineSegment(sketch, "E4.18.0.45", {"start": v(44.21, -128.3) * mm, "end": v(44.21, -133.3) * mm});
            skLineSegment(sketch, "E4.18.0.46", {"start": v(78.21, -133.3) * mm, "end": v(83.21, -133.3) * mm});
            skLineSegment(sketch, "E4.18.0.47", {"start": v(139.41, -128.3) * mm, "end": v(144.41, -128.3) * mm});
            skLineSegment(sketch, "E4.18.0.48", {"start": v(23.81, -128.3) * mm, "end": v(28.81, -128.3) * mm});
            skLineSegment(sketch, "E4.18.0.49", {"start": v(153.01, -128.3) * mm, "end": v(153.01, -133.3) * mm});
            skLineSegment(sketch, "E4.18.0.50", {"start": v(57.81, -128.3) * mm, "end": v(62.81, -128.3) * mm});
            skLineSegment(sketch, "E4.18.0.51", {"start": v(44.21, -128.3) * mm, "end": v(49.21, -128.3) * mm});
            skLineSegment(sketch, "E4.18.0.52", {"start": v(42.41, -128.3) * mm, "end": v(42.41, -133.3) * mm});
            skLineSegment(sketch, "E4.18.0.53", {"start": v(125.81, -133.3) * mm, "end": v(130.81, -133.3) * mm});
            skLineSegment(sketch, "E4.18.0.54", {"start": v(187.01, -133.3) * mm, "end": v(192.01, -133.3) * mm});
            skLineSegment(sketch, "E4.18.0.55", {"start": v(125.81, -128.3) * mm, "end": v(125.81, -133.3) * mm});
            skLineSegment(sketch, "E4.18.0.56", {"start": v(64.61, -128.3) * mm, "end": v(69.61, -128.3) * mm});
            skLineSegment(sketch, "E4.18.0.57", {"start": v(64.61, -133.3) * mm, "end": v(69.61, -133.3) * mm});
            skLineSegment(sketch, "E4.18.0.58", {"start": v(164.81, -128.3) * mm, "end": v(164.81, -133.3) * mm});
            skLineSegment(sketch, "E4.18.0.59", {"start": v(187.01, -128.3) * mm, "end": v(187.01, -133.3) * mm});
            skLineSegment(sketch, "E4.18.0.60", {"start": v(10.21, -128.3) * mm, "end": v(10.21, -133.3) * mm});
            skLineSegment(sketch, "E4.18.0.61", {"start": v(85.01, -128.3) * mm, "end": v(90.01, -128.3) * mm});
            skLineSegment(sketch, "E4.18.0.62", {"start": v(10.21, -128.3) * mm, "end": v(15.21, -128.3) * mm});
            skLineSegment(sketch, "E4.18.0.63", {"start": v(51.01, -128.3) * mm, "end": v(56.01, -128.3) * mm});
            skLineSegment(sketch, "E4.18.0.64", {"start": v(110.41, -128.3) * mm, "end": v(110.41, -133.3) * mm});
            skLineSegment(sketch, "E4.18.0.65", {"start": v(91.81, -133.3) * mm, "end": v(96.81, -133.3) * mm});
            skLineSegment(sketch, "E4.18.0.66", {"start": v(103.61, -128.3) * mm, "end": v(103.61, -133.3) * mm});
            skLineSegment(sketch, "E4.18.0.67", {"start": v(3.41, -128.3) * mm, "end": v(8.41, -128.3) * mm});
            skLineSegment(sketch, "E4.18.0.68", {"start": v(98.61, -133.3) * mm, "end": v(103.61, -133.3) * mm});
            skLineSegment(sketch, "E4.18.0.69", {"start": v(124.01, -128.3) * mm, "end": v(124.01, -133.3) * mm});
            skLineSegment(sketch, "E4.18.0.70", {"start": v(85.01, -133.3) * mm, "end": v(90.01, -133.3) * mm});
            skLineSegment(sketch, "E4.18.0.71", {"start": v(17.01, -128.3) * mm, "end": v(22.01, -128.3) * mm});
            skLineSegment(sketch, "E4.18.0.72", {"start": v(30.61, -128.3) * mm, "end": v(35.61, -128.3) * mm});
            skLineSegment(sketch, "E4.18.0.73", {"start": v(78.21, -128.3) * mm, "end": v(78.21, -133.3) * mm});
            skLineSegment(sketch, "E4.18.0.74", {"start": v(3.41, -128.3) * mm, "end": v(3.41, -133.3) * mm});
            skLineSegment(sketch, "E4.18.0.75", {"start": v(30.61, -128.3) * mm, "end": v(30.61, -133.3) * mm});
            skLineSegment(sketch, "E4.18.0.76", {"start": v(159.81, -128.3) * mm, "end": v(159.81, -133.3) * mm});
            skLineSegment(sketch, "E4.18.0.77", {"start": v(105.41, -128.3) * mm, "end": v(110.41, -128.3) * mm});
            skLineSegment(sketch, "E4.18.0.78", {"start": v(83.21, -128.3) * mm, "end": v(83.21, -133.3) * mm});
            skLineSegment(sketch, "E4.18.0.79", {"start": v(35.61, -128.3) * mm, "end": v(35.61, -133.3) * mm});
            skLineSegment(sketch, "E4.18.0.80", {"start": v(158.01, -128.3) * mm, "end": v(158.01, -133.3) * mm});
            skLineSegment(sketch, "E4.18.0.81", {"start": v(22.01, -128.3) * mm, "end": v(22.01, -133.3) * mm});
            skLineSegment(sketch, "E4.18.0.82", {"start": v(144.41, -128.3) * mm, "end": v(144.41, -133.3) * mm});
            skLineSegment(sketch, "E4.18.0.83", {"start": v(139.41, -128.3) * mm, "end": v(139.41, -133.3) * mm});
            skLineSegment(sketch, "E4.18.0.84", {"start": v(130.81, -128.3) * mm, "end": v(130.81, -133.3) * mm});
            skLineSegment(sketch, "E4.18.0.85", {"start": v(57.81, -128.3) * mm, "end": v(57.81, -133.3) * mm});
            skLineSegment(sketch, "E4.18.0.86", {"start": v(137.61, -128.3) * mm, "end": v(137.61, -133.3) * mm});
            skLineSegment(sketch, "E4.18.0.87", {"start": v(119.01, -128.3) * mm, "end": v(119.01, -133.3) * mm});
            skLineSegment(sketch, "E4.18.0.88", {"start": v(96.81, -128.3) * mm, "end": v(96.81, -133.3) * mm});
            skLineSegment(sketch, "E4.18.0.89", {"start": v(146.21, -133.3) * mm, "end": v(151.21, -133.3) * mm});
            skLineSegment(sketch, "E4.18.0.90", {"start": v(166.61, -133.3) * mm, "end": v(171.61, -133.3) * mm});
            skLineSegment(sketch, "E4.18.0.91", {"start": v(51.01, -128.3) * mm, "end": v(51.01, -133.3) * mm});
            skLineSegment(sketch, "E4.18.0.92", {"start": v(119.01, -128.3) * mm, "end": v(124.01, -128.3) * mm});
            skLineSegment(sketch, "E4.18.0.93", {"start": v(132.61, -128.3) * mm, "end": v(132.61, -133.3) * mm});
            skLineSegment(sketch, "E4.18.0.94", {"start": v(17.01, -128.3) * mm, "end": v(17.01, -133.3) * mm});
            skLineSegment(sketch, "E4.18.0.95", {"start": v(105.41, -128.3) * mm, "end": v(105.41, -133.3) * mm});
            skLineSegment(sketch, "E4.18.0.96", {"start": v(112.21, -133.3) * mm, "end": v(117.21, -133.3) * mm});
            skLineSegment(sketch, "E4.18.0.97", {"start": v(90.01, -128.3) * mm, "end": v(90.01, -133.3) * mm});
            skLineSegment(sketch, "E4.18.0.98", {"start": v(153.01, -128.3) * mm, "end": v(158.01, -128.3) * mm});
            skLineSegment(sketch, "E4.18.0.99", {"start": v(187.01, -128.3) * mm, "end": v(192.01, -128.3) * mm});
            skLineSegment(sketch, "E4.18.0.100", {"start": v(37.41, -133.3) * mm, "end": v(42.41, -133.3) * mm});
            skLineSegment(sketch, "E4.18.0.101", {"start": v(44.21, -133.3) * mm, "end": v(49.21, -133.3) * mm});
            skLineSegment(sketch, "E4.18.0.102", {"start": v(3.41, -133.3) * mm, "end": v(10.21, -133.3) * mm, "construction": true});
            skLineSegment(sketch, "E4.18.0.103", {"start": v(159.81, -128.3) * mm, "end": v(164.81, -128.3) * mm});
            skLineSegment(sketch, "E4.18.0.104", {"start": v(166.61, -128.3) * mm, "end": v(171.61, -128.3) * mm});
            skLineSegment(sketch, "E4.18.0.105", {"start": v(173.41, -128.3) * mm, "end": v(178.41, -128.3) * mm});
            skLineSegment(sketch, "E4.18.0.106", {"start": v(17.01, -133.3) * mm, "end": v(22.01, -133.3) * mm});
            skLineSegment(sketch, "E4.18.0.107", {"start": v(30.61, -133.3) * mm, "end": v(35.61, -133.3) * mm});
            skLineSegment(sketch, "E4.18.0.108", {"start": v(23.81, -133.3) * mm, "end": v(28.81, -133.3) * mm});
            skLineSegment(sketch, "E4.18.0.109", {"start": v(10.21, -133.3) * mm, "end": v(15.21, -133.3) * mm});
            skLineSegment(sketch, "E4.18.0.110", {"start": v(51.01, -133.3) * mm, "end": v(56.01, -133.3) * mm});
            skLineSegment(sketch, "E4.18.0.111", {"start": v(180.21, -128.3) * mm, "end": v(185.21, -128.3) * mm});
            skLineSegment(sketch, "E4.18.0.112", {"start": v(3.41, -133.3) * mm, "end": v(8.41, -133.3) * mm});
            skLineSegment(sketch, "E4.19.0.0", {"start": v(112.26, -135.3) * mm, "end": v(117.26, -135.3) * mm});
            skLineSegment(sketch, "E4.19.0.1", {"start": v(117.26, -135.3) * mm, "end": v(117.26, -140.3) * mm});
            skLineSegment(sketch, "E4.19.0.2", {"start": v(125.86, -135.3) * mm, "end": v(130.86, -135.3) * mm});
            skLineSegment(sketch, "E4.19.0.3", {"start": v(28.86, -135.3) * mm, "end": v(28.86, -140.3) * mm});
            skLineSegment(sketch, "E4.19.0.4", {"start": v(71.46, -135.3) * mm, "end": v(76.46, -135.3) * mm});
            skLineSegment(sketch, "E4.19.0.5", {"start": v(173.46, -135.3) * mm, "end": v(173.46, -140.3) * mm});
            skLineSegment(sketch, "E4.19.0.6", {"start": v(49.26, -135.3) * mm, "end": v(49.26, -140.3) * mm});
            skLineSegment(sketch, "E4.19.0.7", {"start": v(85.06, -135.3) * mm, "end": v(85.06, -140.3) * mm});
            skLineSegment(sketch, "E4.19.0.8", {"start": v(15.26, -135.3) * mm, "end": v(15.26, -140.3) * mm});
            skLineSegment(sketch, "E4.19.0.9", {"start": v(98.66, -135.3) * mm, "end": v(103.66, -135.3) * mm});
            skLineSegment(sketch, "E4.19.0.10", {"start": v(166.66, -135.3) * mm, "end": v(166.66, -140.3) * mm});
            skLineSegment(sketch, "E4.19.0.11", {"start": v(91.86, -135.3) * mm, "end": v(96.86, -135.3) * mm});
            skLineSegment(sketch, "E4.19.0.12", {"start": v(71.46, -140.3) * mm, "end": v(76.46, -140.3) * mm});
            skLineSegment(sketch, "E4.19.0.13", {"start": v(132.66, -140.3) * mm, "end": v(137.66, -140.3) * mm});
            skLineSegment(sketch, "E4.19.0.14", {"start": v(146.26, -135.3) * mm, "end": v(146.26, -140.3) * mm});
            skLineSegment(sketch, "E4.19.0.15", {"start": v(105.46, -140.3) * mm, "end": v(110.46, -140.3) * mm});
            skLineSegment(sketch, "E4.19.0.16", {"start": v(192.06, -135.3) * mm, "end": v(192.06, -140.3) * mm});
            skLineSegment(sketch, "E4.19.0.17", {"start": v(159.86, -140.3) * mm, "end": v(164.86, -140.3) * mm});
            skLineSegment(sketch, "E4.19.0.18", {"start": v(76.46, -135.3) * mm, "end": v(76.46, -140.3) * mm});
            skLineSegment(sketch, "E4.19.0.19", {"start": v(23.86, -135.3) * mm, "end": v(23.86, -140.3) * mm});
            skLineSegment(sketch, "E4.19.0.20", {"start": v(146.26, -135.3) * mm, "end": v(151.26, -135.3) * mm});
            skLineSegment(sketch, "E4.19.0.21", {"start": v(139.46, -140.3) * mm, "end": v(144.46, -140.3) * mm});
            skLineSegment(sketch, "E4.19.0.22", {"start": v(185.26, -135.3) * mm, "end": v(185.26, -140.3) * mm});
            skLineSegment(sketch, "E4.19.0.23", {"start": v(56.06, -135.3) * mm, "end": v(56.06, -140.3) * mm});
            skLineSegment(sketch, "E4.19.0.24", {"start": v(171.66, -135.3) * mm, "end": v(171.66, -140.3) * mm});
            skLineSegment(sketch, "E4.19.0.25", {"start": v(62.86, -135.3) * mm, "end": v(62.86, -140.3) * mm});
            skLineSegment(sketch, "E4.19.0.26", {"start": v(69.66, -135.3) * mm, "end": v(69.66, -140.3) * mm});
            skLineSegment(sketch, "E4.19.0.27", {"start": v(132.66, -135.3) * mm, "end": v(137.66, -135.3) * mm});
            skLineSegment(sketch, "E4.19.0.28", {"start": v(64.66, -135.3) * mm, "end": v(64.66, -140.3) * mm});
            skLineSegment(sketch, "E4.19.0.29", {"start": v(153.06, -140.3) * mm, "end": v(158.06, -140.3) * mm});
            skLineSegment(sketch, "E4.19.0.30", {"start": v(180.26, -140.3) * mm, "end": v(185.26, -140.3) * mm});
            skLineSegment(sketch, "E4.19.0.31", {"start": v(37.46, -135.3) * mm, "end": v(37.46, -140.3) * mm});
            skLineSegment(sketch, "E4.19.0.32", {"start": v(173.46, -140.3) * mm, "end": v(178.46, -140.3) * mm});
            skLineSegment(sketch, "E4.19.0.33", {"start": v(91.86, -135.3) * mm, "end": v(91.86, -140.3) * mm});
            skLineSegment(sketch, "E4.19.0.34", {"start": v(78.26, -135.3) * mm, "end": v(83.26, -135.3) * mm});
            skLineSegment(sketch, "E4.19.0.35", {"start": v(71.46, -135.3) * mm, "end": v(71.46, -140.3) * mm});
            skLineSegment(sketch, "E4.19.0.36", {"start": v(57.86, -140.3) * mm, "end": v(62.86, -140.3) * mm});
            skLineSegment(sketch, "E4.19.0.37", {"start": v(112.26, -135.3) * mm, "end": v(112.26, -140.3) * mm});
            skLineSegment(sketch, "E4.19.0.38", {"start": v(151.26, -135.3) * mm, "end": v(151.26, -140.3) * mm});
            skLineSegment(sketch, "E4.19.0.39", {"start": v(178.46, -135.3) * mm, "end": v(178.46, -140.3) * mm});
            skLineSegment(sketch, "E4.19.0.40", {"start": v(180.26, -135.3) * mm, "end": v(180.26, -140.3) * mm});
            skLineSegment(sketch, "E4.19.0.41", {"start": v(98.66, -135.3) * mm, "end": v(98.66, -140.3) * mm});
            skLineSegment(sketch, "E4.19.0.42", {"start": v(37.46, -135.3) * mm, "end": v(42.46, -135.3) * mm});
            skLineSegment(sketch, "E4.19.0.43", {"start": v(119.06, -140.3) * mm, "end": v(124.06, -140.3) * mm});
            skLineSegment(sketch, "E4.19.0.44", {"start": v(8.46, -135.3) * mm, "end": v(8.46, -140.3) * mm});
            skLineSegment(sketch, "E4.19.0.45", {"start": v(44.26, -135.3) * mm, "end": v(44.26, -140.3) * mm});
            skLineSegment(sketch, "E4.19.0.46", {"start": v(78.26, -140.3) * mm, "end": v(83.26, -140.3) * mm});
            skLineSegment(sketch, "E4.19.0.47", {"start": v(139.46, -135.3) * mm, "end": v(144.46, -135.3) * mm});
            skLineSegment(sketch, "E4.19.0.48", {"start": v(23.86, -135.3) * mm, "end": v(28.86, -135.3) * mm});
            skLineSegment(sketch, "E4.19.0.49", {"start": v(153.06, -135.3) * mm, "end": v(153.06, -140.3) * mm});
            skLineSegment(sketch, "E4.19.0.50", {"start": v(57.86, -135.3) * mm, "end": v(62.86, -135.3) * mm});
            skLineSegment(sketch, "E4.19.0.51", {"start": v(44.26, -135.3) * mm, "end": v(49.26, -135.3) * mm});
            skLineSegment(sketch, "E4.19.0.52", {"start": v(42.46, -135.3) * mm, "end": v(42.46, -140.3) * mm});
            skLineSegment(sketch, "E4.19.0.53", {"start": v(125.86, -140.3) * mm, "end": v(130.86, -140.3) * mm});
            skLineSegment(sketch, "E4.19.0.54", {"start": v(187.06, -140.3) * mm, "end": v(192.06, -140.3) * mm});
            skLineSegment(sketch, "E4.19.0.55", {"start": v(125.86, -135.3) * mm, "end": v(125.86, -140.3) * mm});
            skLineSegment(sketch, "E4.19.0.56", {"start": v(64.66, -135.3) * mm, "end": v(69.66, -135.3) * mm});
            skLineSegment(sketch, "E4.19.0.57", {"start": v(64.66, -140.3) * mm, "end": v(69.66, -140.3) * mm});
            skLineSegment(sketch, "E4.19.0.58", {"start": v(164.86, -135.3) * mm, "end": v(164.86, -140.3) * mm});
            skLineSegment(sketch, "E4.19.0.59", {"start": v(187.06, -135.3) * mm, "end": v(187.06, -140.3) * mm});
            skLineSegment(sketch, "E4.19.0.60", {"start": v(10.26, -135.3) * mm, "end": v(10.26, -140.3) * mm});
            skLineSegment(sketch, "E4.19.0.61", {"start": v(85.06, -135.3) * mm, "end": v(90.06, -135.3) * mm});
            skLineSegment(sketch, "E4.19.0.62", {"start": v(10.26, -135.3) * mm, "end": v(15.26, -135.3) * mm});
            skLineSegment(sketch, "E4.19.0.63", {"start": v(51.06, -135.3) * mm, "end": v(56.06, -135.3) * mm});
            skLineSegment(sketch, "E4.19.0.64", {"start": v(110.46, -135.3) * mm, "end": v(110.46, -140.3) * mm});
            skLineSegment(sketch, "E4.19.0.65", {"start": v(91.86, -140.3) * mm, "end": v(96.86, -140.3) * mm});
            skLineSegment(sketch, "E4.19.0.66", {"start": v(103.66, -135.3) * mm, "end": v(103.66, -140.3) * mm});
            skLineSegment(sketch, "E4.19.0.67", {"start": v(3.46, -135.3) * mm, "end": v(8.46, -135.3) * mm});
            skLineSegment(sketch, "E4.19.0.68", {"start": v(98.66, -140.3) * mm, "end": v(103.66, -140.3) * mm});
            skLineSegment(sketch, "E4.19.0.69", {"start": v(124.06, -135.3) * mm, "end": v(124.06, -140.3) * mm});
            skLineSegment(sketch, "E4.19.0.70", {"start": v(85.06, -140.3) * mm, "end": v(90.06, -140.3) * mm});
            skLineSegment(sketch, "E4.19.0.71", {"start": v(17.06, -135.3) * mm, "end": v(22.06, -135.3) * mm});
            skLineSegment(sketch, "E4.19.0.72", {"start": v(30.66, -135.3) * mm, "end": v(35.66, -135.3) * mm});
            skLineSegment(sketch, "E4.19.0.73", {"start": v(78.26, -135.3) * mm, "end": v(78.26, -140.3) * mm});
            skLineSegment(sketch, "E4.19.0.74", {"start": v(3.46, -135.3) * mm, "end": v(3.46, -140.3) * mm});
            skLineSegment(sketch, "E4.19.0.75", {"start": v(30.66, -135.3) * mm, "end": v(30.66, -140.3) * mm});
            skLineSegment(sketch, "E4.19.0.76", {"start": v(159.86, -135.3) * mm, "end": v(159.86, -140.3) * mm});
            skLineSegment(sketch, "E4.19.0.77", {"start": v(105.46, -135.3) * mm, "end": v(110.46, -135.3) * mm});
            skLineSegment(sketch, "E4.19.0.78", {"start": v(83.26, -135.3) * mm, "end": v(83.26, -140.3) * mm});
            skLineSegment(sketch, "E4.19.0.79", {"start": v(35.66, -135.3) * mm, "end": v(35.66, -140.3) * mm});
            skLineSegment(sketch, "E4.19.0.80", {"start": v(158.06, -135.3) * mm, "end": v(158.06, -140.3) * mm});
            skLineSegment(sketch, "E4.19.0.81", {"start": v(22.06, -135.3) * mm, "end": v(22.06, -140.3) * mm});
            skLineSegment(sketch, "E4.19.0.82", {"start": v(144.46, -135.3) * mm, "end": v(144.46, -140.3) * mm});
            skLineSegment(sketch, "E4.19.0.83", {"start": v(139.46, -135.3) * mm, "end": v(139.46, -140.3) * mm});
            skLineSegment(sketch, "E4.19.0.84", {"start": v(130.86, -135.3) * mm, "end": v(130.86, -140.3) * mm});
            skLineSegment(sketch, "E4.19.0.85", {"start": v(57.86, -135.3) * mm, "end": v(57.86, -140.3) * mm});
            skLineSegment(sketch, "E4.19.0.86", {"start": v(137.66, -135.3) * mm, "end": v(137.66, -140.3) * mm});
            skLineSegment(sketch, "E4.19.0.87", {"start": v(119.06, -135.3) * mm, "end": v(119.06, -140.3) * mm});
            skLineSegment(sketch, "E4.19.0.88", {"start": v(96.86, -135.3) * mm, "end": v(96.86, -140.3) * mm});
            skLineSegment(sketch, "E4.19.0.89", {"start": v(146.26, -140.3) * mm, "end": v(151.26, -140.3) * mm});
            skLineSegment(sketch, "E4.19.0.90", {"start": v(166.66, -140.3) * mm, "end": v(171.66, -140.3) * mm});
            skLineSegment(sketch, "E4.19.0.91", {"start": v(51.06, -135.3) * mm, "end": v(51.06, -140.3) * mm});
            skLineSegment(sketch, "E4.19.0.92", {"start": v(119.06, -135.3) * mm, "end": v(124.06, -135.3) * mm});
            skLineSegment(sketch, "E4.19.0.93", {"start": v(132.66, -135.3) * mm, "end": v(132.66, -140.3) * mm});
            skLineSegment(sketch, "E4.19.0.94", {"start": v(17.06, -135.3) * mm, "end": v(17.06, -140.3) * mm});
            skLineSegment(sketch, "E4.19.0.95", {"start": v(105.46, -135.3) * mm, "end": v(105.46, -140.3) * mm});
            skLineSegment(sketch, "E4.19.0.96", {"start": v(112.26, -140.3) * mm, "end": v(117.26, -140.3) * mm});
            skLineSegment(sketch, "E4.19.0.97", {"start": v(90.06, -135.3) * mm, "end": v(90.06, -140.3) * mm});
            skLineSegment(sketch, "E4.19.0.98", {"start": v(153.06, -135.3) * mm, "end": v(158.06, -135.3) * mm});
            skLineSegment(sketch, "E4.19.0.99", {"start": v(187.06, -135.3) * mm, "end": v(192.06, -135.3) * mm});
            skLineSegment(sketch, "E4.19.0.100", {"start": v(37.46, -140.3) * mm, "end": v(42.46, -140.3) * mm});
            skLineSegment(sketch, "E4.19.0.101", {"start": v(44.26, -140.3) * mm, "end": v(49.26, -140.3) * mm});
            skLineSegment(sketch, "E4.19.0.102", {"start": v(3.46, -140.3) * mm, "end": v(10.26, -140.3) * mm, "construction": true});
            skLineSegment(sketch, "E4.19.0.103", {"start": v(159.86, -135.3) * mm, "end": v(164.86, -135.3) * mm});
            skLineSegment(sketch, "E4.19.0.104", {"start": v(166.66, -135.3) * mm, "end": v(171.66, -135.3) * mm});
            skLineSegment(sketch, "E4.19.0.105", {"start": v(173.46, -135.3) * mm, "end": v(178.46, -135.3) * mm});
            skLineSegment(sketch, "E4.19.0.106", {"start": v(17.06, -140.3) * mm, "end": v(22.06, -140.3) * mm});
            skLineSegment(sketch, "E4.19.0.107", {"start": v(30.66, -140.3) * mm, "end": v(35.66, -140.3) * mm});
            skLineSegment(sketch, "E4.19.0.108", {"start": v(23.86, -140.3) * mm, "end": v(28.86, -140.3) * mm});
            skLineSegment(sketch, "E4.19.0.109", {"start": v(10.26, -140.3) * mm, "end": v(15.26, -140.3) * mm});
            skLineSegment(sketch, "E4.19.0.110", {"start": v(51.06, -140.3) * mm, "end": v(56.06, -140.3) * mm});
            skLineSegment(sketch, "E4.19.0.111", {"start": v(180.26, -135.3) * mm, "end": v(185.26, -135.3) * mm});
            skLineSegment(sketch, "E4.19.0.112", {"start": v(3.46, -140.3) * mm, "end": v(8.46, -140.3) * mm});
            skLineSegment(sketch, "E4.direction1", {"start": v(2.58, -7.3) * mm, "end": v(2.63, -14.3) * mm, "construction": true});
            skSolve(sketch);
        }
        {
            var Q0;
            Q0 = qSketchRegion(id + "F2", true);
            extrude(context, id + "F3", {"entities" : qUnion([Q0]), "operationType" : NewBodyOperationType.REMOVE, "oppositeDirection" : true, "depth" : 25 * mm, "offsetDistance" : 25 * mm});
        }
    });
